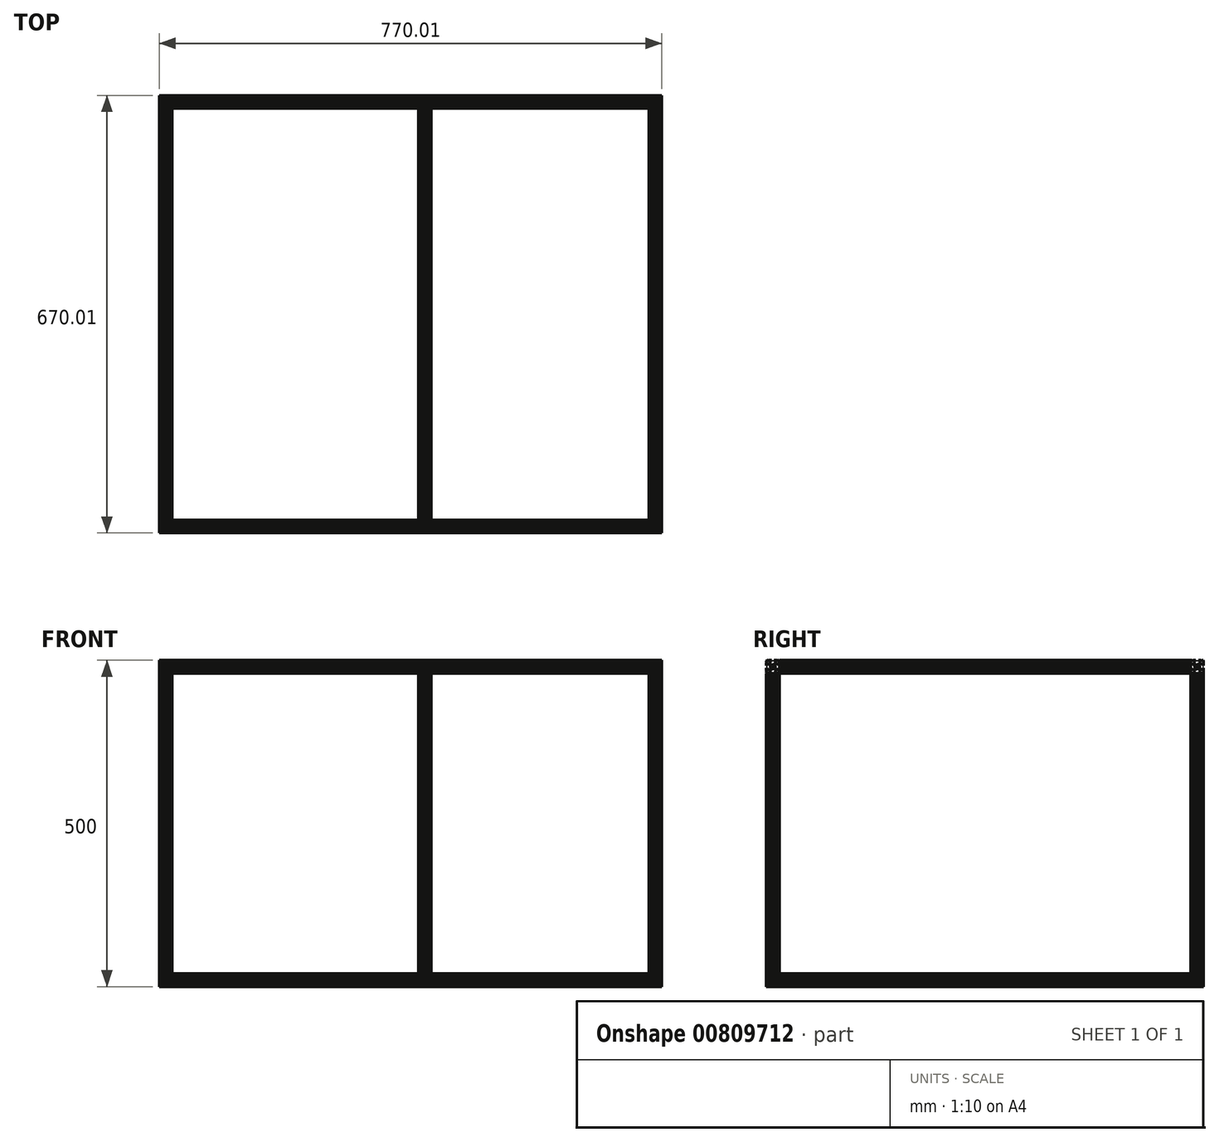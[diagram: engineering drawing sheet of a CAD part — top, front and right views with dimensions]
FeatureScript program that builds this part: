
annotation { "Feature Type Name" : "Feature", "Feature Type Description" : "" }
export const myFeature = defineFeature(function(context is Context, id is Id, definition is map)
    precondition{}
    {
        {
            var Q0;
            Q0=qCreatedBy(makeId("Top.planeOp"),FACE);
            var sketch = newSketch(context, id + "F0", { "sketchPlane" : qUnion([Q0])});
            skLineSegment(sketch, "E0", {"start": v(25.7, -17.22) * mm, "end": v(25.7, -25.12) * mm});
            skLineSegment(sketch, "E1", {"start": v(22.1, -21.63) * mm, "end": v(30.9, -21.63) * mm});
            skLineSegment(sketch, "E2", {"start": v(25.7, -40.02) * mm, "end": v(25.7, -32.12) * mm});
            skLineSegment(sketch, "E3", {"start": v(22.1, -35.63) * mm, "end": v(30.9, -35.63) * mm});
            skLineSegment(sketch, "E4", {"start": v(28.7, -30.77) * mm, "end": v(27.2, -30.77) * mm});
            skLineSegment(sketch, "E5", {"start": v(27.2, -32.77) * mm, "end": v(23.2, -32.77) * mm});
            skLineSegment(sketch, "E6", {"start": v(27.2, -32.77) * mm, "end": v(27.2, -30.77) * mm});
            skLineSegment(sketch, "E7", {"start": v(28.7, -26.48) * mm, "end": v(27.2, -26.48) * mm});
            skLineSegment(sketch, "E8", {"start": v(27.2, -24.48) * mm, "end": v(23.2, -24.48) * mm});
            skLineSegment(sketch, "E9", {"start": v(27.2, -24.48) * mm, "end": v(27.2, -26.48) * mm});
            skLineSegment(sketch, "E10", {"start": v(23.2, -24.48) * mm, "end": v(23.2, -26.12) * mm});
            skLineSegment(sketch, "E11", {"start": v(23.2, -26.12) * mm, "end": v(21.9, -26.12) * mm});
            skLineSegment(sketch, "E12", {"start": v(23.2, -32.77) * mm, "end": v(21.9, -26.12) * mm});
            skLineSegment(sketch, "E13", {"start": v(27.34, -20.94) * mm, "end": v(26.38, -19.97) * mm});
            skLineSegment(sketch, "E14", {"start": v(26.38, -19.97) * mm, "end": v(25, -19.97) * mm});
            skLineSegment(sketch, "E15", {"start": v(25, -19.97) * mm, "end": v(24.04, -20.94) * mm});
            skLineSegment(sketch, "E16", {"start": v(24.04, -20.94) * mm, "end": v(24.04, -22.3) * mm});
            skLineSegment(sketch, "E17", {"start": v(24.04, -22.3) * mm, "end": v(25, -23.28) * mm});
            skLineSegment(sketch, "E18", {"start": v(25, -23.28) * mm, "end": v(26.38, -23.28) * mm});
            skLineSegment(sketch, "E19", {"start": v(26.38, -23.28) * mm, "end": v(27.34, -22.3) * mm});
            skLineSegment(sketch, "E20", {"start": v(27.34, -22.3) * mm, "end": v(27.34, -20.94) * mm});
            skLineSegment(sketch, "E21", {"start": v(27.34, -34.94) * mm, "end": v(26.38, -33.98) * mm});
            skLineSegment(sketch, "E22", {"start": v(26.38, -33.98) * mm, "end": v(25, -33.98) * mm});
            skLineSegment(sketch, "E23", {"start": v(25, -33.98) * mm, "end": v(24.04, -34.94) * mm});
            skLineSegment(sketch, "E24", {"start": v(24.04, -34.94) * mm, "end": v(24.04, -36.3) * mm});
            skLineSegment(sketch, "E25", {"start": v(24.04, -36.3) * mm, "end": v(25, -37.28) * mm});
            skLineSegment(sketch, "E26", {"start": v(25, -37.28) * mm, "end": v(26.38, -37.28) * mm});
            skLineSegment(sketch, "E27", {"start": v(26.38, -37.28) * mm, "end": v(27.34, -36.3) * mm});
            skLineSegment(sketch, "E28", {"start": v(27.34, -36.3) * mm, "end": v(27.34, -34.94) * mm});
            skLineSegment(sketch, "E29", {"start": v(27.7, -18.62) * mm, "end": v(28.7, -19.62) * mm});
            skLineSegment(sketch, "E30", {"start": v(28.7, -37.62) * mm, "end": v(27.7, -38.62) * mm});
            skLineSegment(sketch, "E31", {"start": v(25.7, -18.83) * mm, "end": v(26.44, -18.83) * mm});
            skLineSegment(sketch, "E32", {"start": v(26.44, -18.83) * mm, "end": v(26.44, -18.62) * mm});
            skLineSegment(sketch, "E33", {"start": v(25.7, -18.83) * mm, "end": v(24.94, -18.83) * mm});
            skLineSegment(sketch, "E34", {"start": v(24.94, -18.83) * mm, "end": v(24.94, -18.62) * mm});
            skLineSegment(sketch, "E35", {"start": v(27.7, -18.62) * mm, "end": v(26.44, -18.62) * mm});
            skLineSegment(sketch, "E36", {"start": v(28.5, -21.63) * mm, "end": v(28.5, -22.38) * mm});
            skLineSegment(sketch, "E37", {"start": v(28.5, -22.38) * mm, "end": v(28.7, -22.38) * mm});
            skLineSegment(sketch, "E38", {"start": v(28.5, -21.63) * mm, "end": v(28.5, -20.88) * mm});
            skLineSegment(sketch, "E39", {"start": v(28.5, -20.88) * mm, "end": v(28.7, -20.88) * mm});
            skLineSegment(sketch, "E40", {"start": v(28.5, -35.63) * mm, "end": v(28.5, -34.88) * mm});
            skLineSegment(sketch, "E41", {"start": v(28.5, -34.88) * mm, "end": v(28.7, -34.88) * mm});
            skLineSegment(sketch, "E42", {"start": v(28.5, -35.63) * mm, "end": v(28.5, -36.38) * mm});
            skLineSegment(sketch, "E43", {"start": v(28.5, -36.38) * mm, "end": v(28.7, -36.38) * mm});
            skLineSegment(sketch, "E44", {"start": v(25.7, -38.43) * mm, "end": v(26.44, -38.43) * mm});
            skLineSegment(sketch, "E45", {"start": v(26.44, -38.43) * mm, "end": v(26.44, -38.62) * mm});
            skLineSegment(sketch, "E46", {"start": v(25.7, -38.43) * mm, "end": v(24.94, -38.43) * mm});
            skLineSegment(sketch, "E47", {"start": v(24.94, -38.43) * mm, "end": v(24.94, -38.62) * mm});
            skLineSegment(sketch, "E48", {"start": v(28.7, -19.62) * mm, "end": v(28.7, -20.88) * mm});
            skLineSegment(sketch, "E49", {"start": v(28.7, -22.38) * mm, "end": v(28.7, -26.48) * mm});
            skLineSegment(sketch, "E50", {"start": v(27.7, -38.62) * mm, "end": v(26.44, -38.62) * mm});
            skLineSegment(sketch, "E51", {"start": v(28.7, -37.62) * mm, "end": v(28.7, -36.38) * mm});
            skLineSegment(sketch, "E52", {"start": v(28.7, -34.88) * mm, "end": v(28.7, -30.77) * mm});
            skLineSegment(sketch, "E53", {"start": v(18.7, -13.92) * mm, "end": v(18.7, -42.92) * mm});
            skLineSegment(sketch, "E54", {"start": v(20.84, -18.62) * mm, "end": v(20.84, -20.12) * mm});
            skLineSegment(sketch, "E55", {"start": v(22.84, -20.12) * mm, "end": v(22.84, -24.12) * mm});
            skLineSegment(sketch, "E56", {"start": v(22.84, -20.12) * mm, "end": v(20.84, -20.12) * mm});
            skLineSegment(sketch, "E57", {"start": v(16.54, -18.62) * mm, "end": v(16.54, -20.12) * mm});
            skLineSegment(sketch, "E58", {"start": v(14.54, -20.12) * mm, "end": v(14.54, -24.12) * mm});
            skLineSegment(sketch, "E59", {"start": v(14.54, -20.12) * mm, "end": v(16.54, -20.12) * mm});
            skLineSegment(sketch, "E60", {"start": v(14.54, -24.12) * mm, "end": v(16.2, -24.12) * mm});
            skLineSegment(sketch, "E61", {"start": v(16.2, -24.12) * mm, "end": v(16.2, -25.42) * mm});
            skLineSegment(sketch, "E62", {"start": v(22.84, -24.12) * mm, "end": v(16.2, -25.42) * mm});
            skLineSegment(sketch, "E63", {"start": v(16.54, -38.62) * mm, "end": v(16.54, -37.12) * mm});
            skLineSegment(sketch, "E64", {"start": v(14.54, -37.12) * mm, "end": v(14.54, -33.12) * mm});
            skLineSegment(sketch, "E65", {"start": v(14.54, -37.12) * mm, "end": v(16.54, -37.12) * mm});
            skLineSegment(sketch, "E66", {"start": v(20.84, -38.62) * mm, "end": v(20.84, -37.12) * mm});
            skLineSegment(sketch, "E67", {"start": v(22.84, -37.12) * mm, "end": v(22.84, -33.12) * mm});
            skLineSegment(sketch, "E68", {"start": v(22.84, -37.12) * mm, "end": v(20.84, -37.12) * mm});
            skLineSegment(sketch, "E69", {"start": v(22.84, -33.12) * mm, "end": v(21.2, -33.12) * mm});
            skLineSegment(sketch, "E70", {"start": v(21.2, -33.12) * mm, "end": v(21.2, -31.83) * mm});
            skLineSegment(sketch, "E71", {"start": v(14.54, -33.12) * mm, "end": v(21.2, -31.83) * mm});
            skLineSegment(sketch, "E72", {"start": v(24.94, -18.62) * mm, "end": v(20.84, -18.62) * mm});
            skLineSegment(sketch, "E73", {"start": v(24.94, -38.62) * mm, "end": v(20.84, -38.62) * mm});
            skLineSegment(sketch, "E74", {"start": v(6.1, -28.62) * mm, "end": v(31.6, -28.62) * mm});
            skLineSegment(sketch, "E75", {"start": v(11.7, -17.22) * mm, "end": v(11.7, -25.12) * mm});
            skLineSegment(sketch, "E76", {"start": v(15.3, -21.63) * mm, "end": v(6.5, -21.63) * mm});
            skLineSegment(sketch, "E77", {"start": v(10.04, -20.94) * mm, "end": v(11, -19.97) * mm});
            skLineSegment(sketch, "E78", {"start": v(11, -19.97) * mm, "end": v(12.38, -19.97) * mm});
            skLineSegment(sketch, "E79", {"start": v(12.38, -19.97) * mm, "end": v(13.34, -20.94) * mm});
            skLineSegment(sketch, "E80", {"start": v(13.34, -20.94) * mm, "end": v(13.34, -22.3) * mm});
            skLineSegment(sketch, "E81", {"start": v(13.34, -22.3) * mm, "end": v(12.38, -23.28) * mm});
            skLineSegment(sketch, "E82", {"start": v(12.38, -23.28) * mm, "end": v(11, -23.28) * mm});
            skLineSegment(sketch, "E83", {"start": v(11, -23.28) * mm, "end": v(10.04, -22.3) * mm});
            skLineSegment(sketch, "E84", {"start": v(10.04, -22.3) * mm, "end": v(10.04, -20.94) * mm});
            skLineSegment(sketch, "E85", {"start": v(9.7, -18.62) * mm, "end": v(8.7, -19.62) * mm});
            skLineSegment(sketch, "E86", {"start": v(11.7, -18.83) * mm, "end": v(10.94, -18.83) * mm});
            skLineSegment(sketch, "E87", {"start": v(10.94, -18.83) * mm, "end": v(10.94, -18.62) * mm});
            skLineSegment(sketch, "E88", {"start": v(11.7, -18.83) * mm, "end": v(12.44, -18.83) * mm});
            skLineSegment(sketch, "E89", {"start": v(12.44, -18.83) * mm, "end": v(12.44, -18.62) * mm});
            skLineSegment(sketch, "E90", {"start": v(9.7, -18.62) * mm, "end": v(10.94, -18.62) * mm});
            skLineSegment(sketch, "E91", {"start": v(8.9, -21.63) * mm, "end": v(8.9, -22.38) * mm});
            skLineSegment(sketch, "E92", {"start": v(8.9, -22.38) * mm, "end": v(8.7, -22.38) * mm});
            skLineSegment(sketch, "E93", {"start": v(8.9, -21.63) * mm, "end": v(8.9, -20.88) * mm});
            skLineSegment(sketch, "E94", {"start": v(8.9, -20.88) * mm, "end": v(8.7, -20.88) * mm});
            skLineSegment(sketch, "E95", {"start": v(8.7, -19.62) * mm, "end": v(8.7, -20.88) * mm});
            skLineSegment(sketch, "E96", {"start": v(8.7, -22.38) * mm, "end": v(8.7, -26.48) * mm});
            skLineSegment(sketch, "E97", {"start": v(12.44, -18.62) * mm, "end": v(16.54, -18.62) * mm});
            skLineSegment(sketch, "E98", {"start": v(11.7, -40.02) * mm, "end": v(11.7, -32.12) * mm});
            skLineSegment(sketch, "E99", {"start": v(15.3, -35.63) * mm, "end": v(6.5, -35.63) * mm});
            skLineSegment(sketch, "E100", {"start": v(10.04, -34.94) * mm, "end": v(11, -33.98) * mm});
            skLineSegment(sketch, "E101", {"start": v(11, -33.98) * mm, "end": v(12.38, -33.98) * mm});
            skLineSegment(sketch, "E102", {"start": v(12.38, -33.98) * mm, "end": v(13.34, -34.94) * mm});
            skLineSegment(sketch, "E103", {"start": v(13.34, -34.94) * mm, "end": v(13.34, -36.3) * mm});
            skLineSegment(sketch, "E104", {"start": v(13.34, -36.3) * mm, "end": v(12.38, -37.28) * mm});
            skLineSegment(sketch, "E105", {"start": v(12.38, -37.28) * mm, "end": v(11, -37.28) * mm});
            skLineSegment(sketch, "E106", {"start": v(11, -37.28) * mm, "end": v(10.04, -36.3) * mm});
            skLineSegment(sketch, "E107", {"start": v(10.04, -36.3) * mm, "end": v(10.04, -34.94) * mm});
            skLineSegment(sketch, "E108", {"start": v(8.7, -37.62) * mm, "end": v(9.7, -38.62) * mm});
            skLineSegment(sketch, "E109", {"start": v(8.9, -35.63) * mm, "end": v(8.9, -34.88) * mm});
            skLineSegment(sketch, "E110", {"start": v(8.9, -34.88) * mm, "end": v(8.7, -34.88) * mm});
            skLineSegment(sketch, "E111", {"start": v(8.9, -35.63) * mm, "end": v(8.9, -36.38) * mm});
            skLineSegment(sketch, "E112", {"start": v(8.9, -36.38) * mm, "end": v(8.7, -36.38) * mm});
            skLineSegment(sketch, "E113", {"start": v(11.7, -38.43) * mm, "end": v(10.94, -38.43) * mm});
            skLineSegment(sketch, "E114", {"start": v(10.94, -38.43) * mm, "end": v(10.94, -38.62) * mm});
            skLineSegment(sketch, "E115", {"start": v(11.7, -38.43) * mm, "end": v(12.44, -38.43) * mm});
            skLineSegment(sketch, "E116", {"start": v(12.44, -38.43) * mm, "end": v(12.44, -38.62) * mm});
            skLineSegment(sketch, "E117", {"start": v(9.7, -38.62) * mm, "end": v(10.94, -38.62) * mm});
            skLineSegment(sketch, "E118", {"start": v(8.7, -37.62) * mm, "end": v(8.7, -36.38) * mm});
            skLineSegment(sketch, "E119", {"start": v(8.7, -34.88) * mm, "end": v(8.7, -30.77) * mm});
            skLineSegment(sketch, "E120", {"start": v(12.44, -38.62) * mm, "end": v(16.54, -38.62) * mm});
            skLineSegment(sketch, "E121", {"start": v(8.7, -26.48) * mm, "end": v(10.2, -26.48) * mm});
            skLineSegment(sketch, "E122", {"start": v(10.2, -24.48) * mm, "end": v(14.2, -24.48) * mm});
            skLineSegment(sketch, "E123", {"start": v(10.2, -24.48) * mm, "end": v(10.2, -26.48) * mm});
            skLineSegment(sketch, "E124", {"start": v(8.7, -30.77) * mm, "end": v(10.2, -30.77) * mm});
            skLineSegment(sketch, "E125", {"start": v(10.2, -32.77) * mm, "end": v(14.2, -32.77) * mm});
            skLineSegment(sketch, "E126", {"start": v(10.2, -32.77) * mm, "end": v(10.2, -30.77) * mm});
            skLineSegment(sketch, "E127", {"start": v(14.2, -32.77) * mm, "end": v(14.2, -31.12) * mm});
            skLineSegment(sketch, "E128", {"start": v(14.2, -31.12) * mm, "end": v(15.5, -31.12) * mm});
            skLineSegment(sketch, "E129", {"start": v(14.2, -24.48) * mm, "end": v(15.5, -31.12) * mm});
            skCircle(sketch, "E130", {"center": v(18.7, -28.62) * mm, "radius": 1.6 * mm});
            skSolve(sketch);
        }
        {
            var Q0;
            {var subQ21=sQuery(id+"F0.wireOp",EDGE,"E10");Q0=makeQuery(id+"F0.imprint","IMPRINT",FACE,{"disambiguationData":[TD([[makeQuery(id+"F0.imprint","IMPRINT",EDGE,{"derivedFrom":subQ21}),-1.0]])]});}
            var Q1;
            {var subQ9=sQuery(id+"F0.wireOp",EDGE,"E23");Q1=makeQuery(id+"F0.imprint","IMPRINT",FACE,{"disambiguationData":[TD([[makeQuery(id+"F0.imprint","IMPRINT",EDGE,{"derivedFrom":subQ9}),-1.0]])]});}
            var Q2;
            {var subQ21=sQuery(id+"F0.wireOp",EDGE,"E60");Q2=makeQuery(id+"F0.imprint","IMPRINT",FACE,{"disambiguationData":[TD([[makeQuery(id+"F0.imprint","IMPRINT",EDGE,{"derivedFrom":subQ21}),-1.0]])]});}
            var Q3;
            {var subQ1=sQuery(id+"F0.wireOp",EDGE,"E102");Q3=makeQuery(id+"F0.imprint","IMPRINT",FACE,{"disambiguationData":[TD([[makeQuery(id+"F0.imprint","IMPRINT",EDGE,{"derivedFrom":subQ1}),1.0]])]});}
            var Q4;
            {var subQ0=sQuery(id+"F0.wireOp",EDGE,"E74");var subQ1=sQuery(id+"F0.wireOp",EDGE,"E53");var subQ2=makeQuery(id+"F0.imprint","INTERSECT",VERTEX,{"derivedFrom":[subQ1,subQ0]});Q4=makeQuery(id+"F0.imprint","IMPRINT",FACE,{"disambiguationData":[TD([[makeQuery(id+"F0.imprint","IMPRINT",EDGE,{"disambiguationData":[TD([[subQ2,-1.0]])],"derivedFrom":subQ1}),-1.0]])]});}
            var Q5;
            {var subQ0=sQuery(id+"F0.wireOp",EDGE,"E74");var subQ1=sQuery(id+"F0.wireOp",EDGE,"E53");var subQ2=makeQuery(id+"F0.imprint","INTERSECT",VERTEX,{"derivedFrom":[subQ1,subQ0]});Q5=makeQuery(id+"F0.imprint","IMPRINT",FACE,{"disambiguationData":[TD([[makeQuery(id+"F0.imprint","IMPRINT",EDGE,{"disambiguationData":[TD([[subQ2,-1.0]])],"derivedFrom":subQ1}),1.0]])]});}
            var Q6;
            {var subQ0=sQuery(id+"F0.wireOp",EDGE,"E130");var subQ1=sQuery(id+"F0.wireOp",EDGE,"E53");var subQ2=makeQuery(id+"F0.imprint","INTERSECT",VERTEX,{"disambiguationData":[OD(0.0)],"derivedFrom":[subQ1,subQ0]});Q6=makeQuery(id+"F0.imprint","IMPRINT",FACE,{"disambiguationData":[TD([[makeQuery(id+"F0.imprint","IMPRINT",EDGE,{"disambiguationData":[TD([[subQ2,-1.0]])],"derivedFrom":subQ1}),1.0]])]});}
            var Q7;
            {var subQ0=sQuery(id+"F0.wireOp",EDGE,"E130");var subQ1=sQuery(id+"F0.wireOp",EDGE,"E53");var subQ2=makeQuery(id+"F0.imprint","INTERSECT",VERTEX,{"disambiguationData":[OD(0.0)],"derivedFrom":[subQ1,subQ0]});Q7=makeQuery(id+"F0.imprint","IMPRINT",FACE,{"disambiguationData":[TD([[makeQuery(id+"F0.imprint","IMPRINT",EDGE,{"disambiguationData":[TD([[subQ2,-1.0]])],"derivedFrom":subQ1}),-1.0]])]});}
            var Q8;
            {var subQ0=sQuery(id+"F0.wireOp",EDGE,"E102");Q8=makeQuery(id+"F0.imprint","IMPRINT",FACE,{"disambiguationData":[TD([[makeQuery(id+"F0.imprint","IMPRINT",EDGE,{"derivedFrom":subQ0}),-1.0]])]});}
            var Q9;
            {var subQ0=sQuery(id+"F0.wireOp",EDGE,"E104");Q9=makeQuery(id+"F0.imprint","IMPRINT",FACE,{"disambiguationData":[TD([[makeQuery(id+"F0.imprint","IMPRINT",EDGE,{"derivedFrom":subQ0}),-1.0]])]});}
            var Q10;
            {var subQ1=sQuery(id+"F0.wireOp",EDGE,"E100");Q10=makeQuery(id+"F0.imprint","IMPRINT",FACE,{"disambiguationData":[TD([[makeQuery(id+"F0.imprint","IMPRINT",EDGE,{"derivedFrom":subQ1}),-1.0]])]});}
            var Q11;
            {var subQ0=sQuery(id+"F0.wireOp",EDGE,"E106");Q11=makeQuery(id+"F0.imprint","IMPRINT",FACE,{"disambiguationData":[TD([[makeQuery(id+"F0.imprint","IMPRINT",EDGE,{"derivedFrom":subQ0}),-1.0]])]});}
            var Q12;
            Q12=makeQuery(id+"F0.imprint","IMPRINT",FACE,{"disambiguationData":[TD([[makeQuery(id+"F0.imprint","IMPRINT",EDGE,{"derivedFrom":sQuery(id+"F0.wireOp",EDGE,"E57")}),-1.0]])]});
            var Q13;
            Q13=makeQuery(id+"F0.imprint","IMPRINT",FACE,{"disambiguationData":[TD([[makeQuery(id+"F0.imprint","IMPRINT",EDGE,{"derivedFrom":sQuery(id+"F0.wireOp",EDGE,"E63")}),1.0]])]});
            var Q14;
            {var subQ0=sQuery(id+"F0.wireOp",EDGE,"E79");Q14=makeQuery(id+"F0.imprint","IMPRINT",FACE,{"disambiguationData":[TD([[makeQuery(id+"F0.imprint","IMPRINT",EDGE,{"derivedFrom":subQ0}),-1.0]])]});}
            var Q15;
            Q15=makeQuery(id+"F0.imprint","IMPRINT",FACE,{"disambiguationData":[TD([[makeQuery(id+"F0.imprint","IMPRINT",EDGE,{"derivedFrom":sQuery(id+"F0.wireOp",EDGE,"E4")}),1.0]])]});
            var Q16;
            {var subQ3=sQuery(id+"F0.wireOp",EDGE,"E15");Q16=makeQuery(id+"F0.imprint","IMPRINT",FACE,{"disambiguationData":[TD([[makeQuery(id+"F0.imprint","IMPRINT",EDGE,{"derivedFrom":subQ3}),-1.0]])]});}
            var Q17;
            {var subQ0=sQuery(id+"F0.wireOp",EDGE,"E15");Q17=makeQuery(id+"F0.imprint","IMPRINT",FACE,{"disambiguationData":[TD([[makeQuery(id+"F0.imprint","IMPRINT",EDGE,{"derivedFrom":subQ0}),1.0]])]});}
            var Q18;
            Q18=makeQuery(id+"F0.imprint","IMPRINT",FACE,{"disambiguationData":[TD([[makeQuery(id+"F0.imprint","IMPRINT",EDGE,{"derivedFrom":sQuery(id+"F0.wireOp",EDGE,"E7")}),-1.0]])]});
            var Q19;
            {var subQ5=sQuery(id+"F0.wireOp",EDGE,"E25");Q19=makeQuery(id+"F0.imprint","IMPRINT",FACE,{"disambiguationData":[TD([[makeQuery(id+"F0.imprint","IMPRINT",EDGE,{"derivedFrom":subQ5}),-1.0]])]});}
            var Q20;
            {var subQ0=sQuery(id+"F0.wireOp",EDGE,"E25");Q20=makeQuery(id+"F0.imprint","IMPRINT",FACE,{"disambiguationData":[TD([[makeQuery(id+"F0.imprint","IMPRINT",EDGE,{"derivedFrom":subQ0}),1.0]])]});}
            var Q21;
            {var subQ0=sQuery(id+"F0.wireOp",EDGE,"E27");Q21=makeQuery(id+"F0.imprint","IMPRINT",FACE,{"disambiguationData":[TD([[makeQuery(id+"F0.imprint","IMPRINT",EDGE,{"derivedFrom":subQ0}),1.0]])]});}
            var Q22;
            {var subQ1=sQuery(id+"F0.wireOp",EDGE,"E21");Q22=makeQuery(id+"F0.imprint","IMPRINT",FACE,{"disambiguationData":[TD([[makeQuery(id+"F0.imprint","IMPRINT",EDGE,{"derivedFrom":subQ1}),1.0]])]});}
            var Q23;
            {var subQ0=sQuery(id+"F0.wireOp",EDGE,"E83");Q23=makeQuery(id+"F0.imprint","IMPRINT",FACE,{"disambiguationData":[TD([[makeQuery(id+"F0.imprint","IMPRINT",EDGE,{"derivedFrom":subQ0}),-1.0]])]});}
            var Q24;
            {var subQ8=sQuery(id+"F0.wireOp",EDGE,"E100");Q24=makeQuery(id+"F0.imprint","IMPRINT",FACE,{"disambiguationData":[TD([[makeQuery(id+"F0.imprint","IMPRINT",EDGE,{"derivedFrom":subQ8}),1.0]])]});}
            var Q25;
            {var subQ8=sQuery(id+"F0.wireOp",EDGE,"E83");Q25=makeQuery(id+"F0.imprint","IMPRINT",FACE,{"disambiguationData":[TD([[makeQuery(id+"F0.imprint","IMPRINT",EDGE,{"derivedFrom":subQ8}),1.0]])]});}
            var Q26;
            {var subQ6=sQuery(id+"F0.wireOp",EDGE,"E106");Q26=makeQuery(id+"F0.imprint","IMPRINT",FACE,{"disambiguationData":[TD([[makeQuery(id+"F0.imprint","IMPRINT",EDGE,{"derivedFrom":subQ6}),1.0]])]});}
            var Q27;
            {var subQ8=sQuery(id+"F0.wireOp",EDGE,"E77");Q27=makeQuery(id+"F0.imprint","IMPRINT",FACE,{"disambiguationData":[TD([[makeQuery(id+"F0.imprint","IMPRINT",EDGE,{"derivedFrom":subQ8}),1.0]])]});}
            var Q28;
            {var subQ1=sQuery(id+"F0.wireOp",EDGE,"E77");Q28=makeQuery(id+"F0.imprint","IMPRINT",FACE,{"disambiguationData":[TD([[makeQuery(id+"F0.imprint","IMPRINT",EDGE,{"derivedFrom":subQ1}),-1.0]])]});}
            var Q29;
            {var subQ2=sQuery(id+"F0.wireOp",EDGE,"E13");Q29=makeQuery(id+"F0.imprint","IMPRINT",FACE,{"disambiguationData":[TD([[makeQuery(id+"F0.imprint","IMPRINT",EDGE,{"derivedFrom":subQ2}),-1.0]])]});}
            var Q30;
            {var subQ1=sQuery(id+"F0.wireOp",EDGE,"E13");Q30=makeQuery(id+"F0.imprint","IMPRINT",FACE,{"disambiguationData":[TD([[makeQuery(id+"F0.imprint","IMPRINT",EDGE,{"derivedFrom":subQ1}),1.0]])]});}
            var Q31;
            {var subQ0=sQuery(id+"F0.wireOp",EDGE,"E17");Q31=makeQuery(id+"F0.imprint","IMPRINT",FACE,{"disambiguationData":[TD([[makeQuery(id+"F0.imprint","IMPRINT",EDGE,{"derivedFrom":subQ0}),1.0]])]});}
            var Q32;
            {var subQ3=sQuery(id+"F0.wireOp",EDGE,"E27");Q32=makeQuery(id+"F0.imprint","IMPRINT",FACE,{"disambiguationData":[TD([[makeQuery(id+"F0.imprint","IMPRINT",EDGE,{"derivedFrom":subQ3}),-1.0]])]});}
            var Q33;
            {var subQ0=sQuery(id+"F0.wireOp",EDGE,"E23");Q33=makeQuery(id+"F0.imprint","IMPRINT",FACE,{"disambiguationData":[TD([[makeQuery(id+"F0.imprint","IMPRINT",EDGE,{"derivedFrom":subQ0}),1.0]])]});}
            var Q34;
            {var subQ0=sQuery(id+"F0.wireOp",EDGE,"E81");Q34=makeQuery(id+"F0.imprint","IMPRINT",FACE,{"disambiguationData":[TD([[makeQuery(id+"F0.imprint","IMPRINT",EDGE,{"derivedFrom":subQ0}),-1.0]])]});}
            var Q35;
            {var subQ0=sQuery(id+"F0.wireOp",EDGE,"E19");Q35=makeQuery(id+"F0.imprint","IMPRINT",FACE,{"disambiguationData":[TD([[makeQuery(id+"F0.imprint","IMPRINT",EDGE,{"derivedFrom":subQ0}),1.0]])]});}
            extrude(context, id + "F1", {"entities" : qUnion([Q0, Q1, Q2, Q3, Q4, Q5, Q6, Q7, Q8, Q9, Q10, Q11, Q12, Q13, Q14, Q15, Q16, Q17, Q18, Q19, Q20, Q21, Q22, Q23, Q24, Q25, Q26, Q27, Q28, Q29, Q30, Q31, Q32, Q33, Q34, Q35]), "depth" : 480 * mm, "offsetDistance" : 25 * mm});
        }
        {
            var Q0;
            Q0=makeQuery(id+"F1.opExtrude","SWEPT_BODY",BODY,{"disambiguationData":[OSD([sQuery(id+"F0.wireOp",EDGE,"E4"),sQuery(id+"F0.wireOp",EDGE,"E5"),sQuery(id+"F0.wireOp",EDGE,"E6"),sQuery(id+"F0.wireOp",EDGE,"E7"),sQuery(id+"F0.wireOp",EDGE,"E8"),sQuery(id+"F0.wireOp",EDGE,"E9"),sQuery(id+"F0.wireOp",EDGE,"E10"),sQuery(id+"F0.wireOp",EDGE,"E11"),sQuery(id+"F0.wireOp",EDGE,"E12"),sQuery(id+"F0.wireOp",EDGE,"E29"),sQuery(id+"F0.wireOp",EDGE,"E30"),sQuery(id+"F0.wireOp",EDGE,"E31"),sQuery(id+"F0.wireOp",EDGE,"E32"),sQuery(id+"F0.wireOp",EDGE,"E33"),sQuery(id+"F0.wireOp",EDGE,"E34"),sQuery(id+"F0.wireOp",EDGE,"E35"),sQuery(id+"F0.wireOp",EDGE,"E36"),sQuery(id+"F0.wireOp",EDGE,"E37"),sQuery(id+"F0.wireOp",EDGE,"E38"),sQuery(id+"F0.wireOp",EDGE,"E39"),sQuery(id+"F0.wireOp",EDGE,"E40"),sQuery(id+"F0.wireOp",EDGE,"E41"),sQuery(id+"F0.wireOp",EDGE,"E42"),sQuery(id+"F0.wireOp",EDGE,"E43"),sQuery(id+"F0.wireOp",EDGE,"E44"),sQuery(id+"F0.wireOp",EDGE,"E45"),sQuery(id+"F0.wireOp",EDGE,"E46"),sQuery(id+"F0.wireOp",EDGE,"E47"),sQuery(id+"F0.wireOp",EDGE,"E48"),sQuery(id+"F0.wireOp",EDGE,"E49"),sQuery(id+"F0.wireOp",EDGE,"E50"),sQuery(id+"F0.wireOp",EDGE,"E51"),sQuery(id+"F0.wireOp",EDGE,"E52"),sQuery(id+"F0.wireOp",EDGE,"E54"),sQuery(id+"F0.wireOp",EDGE,"E55"),sQuery(id+"F0.wireOp",EDGE,"E56"),sQuery(id+"F0.wireOp",EDGE,"E57"),sQuery(id+"F0.wireOp",EDGE,"E58"),sQuery(id+"F0.wireOp",EDGE,"E59"),sQuery(id+"F0.wireOp",EDGE,"E60"),sQuery(id+"F0.wireOp",EDGE,"E61"),sQuery(id+"F0.wireOp",EDGE,"E62"),sQuery(id+"F0.wireOp",EDGE,"E63"),sQuery(id+"F0.wireOp",EDGE,"E64"),sQuery(id+"F0.wireOp",EDGE,"E65"),sQuery(id+"F0.wireOp",EDGE,"E66"),sQuery(id+"F0.wireOp",EDGE,"E67"),sQuery(id+"F0.wireOp",EDGE,"E68"),sQuery(id+"F0.wireOp",EDGE,"E69"),sQuery(id+"F0.wireOp",EDGE,"E70"),sQuery(id+"F0.wireOp",EDGE,"E71"),sQuery(id+"F0.wireOp",EDGE,"E72"),sQuery(id+"F0.wireOp",EDGE,"E73"),sQuery(id+"F0.wireOp",EDGE,"E85"),sQuery(id+"F0.wireOp",EDGE,"E86"),sQuery(id+"F0.wireOp",EDGE,"E87"),sQuery(id+"F0.wireOp",EDGE,"E88"),sQuery(id+"F0.wireOp",EDGE,"E89"),sQuery(id+"F0.wireOp",EDGE,"E90"),sQuery(id+"F0.wireOp",EDGE,"E91"),sQuery(id+"F0.wireOp",EDGE,"E92"),sQuery(id+"F0.wireOp",EDGE,"E93"),sQuery(id+"F0.wireOp",EDGE,"E94"),sQuery(id+"F0.wireOp",EDGE,"E95"),sQuery(id+"F0.wireOp",EDGE,"E96"),sQuery(id+"F0.wireOp",EDGE,"E97"),sQuery(id+"F0.wireOp",EDGE,"E108"),sQuery(id+"F0.wireOp",EDGE,"E109"),sQuery(id+"F0.wireOp",EDGE,"E110"),sQuery(id+"F0.wireOp",EDGE,"E111"),sQuery(id+"F0.wireOp",EDGE,"E112"),sQuery(id+"F0.wireOp",EDGE,"E113"),sQuery(id+"F0.wireOp",EDGE,"E114"),sQuery(id+"F0.wireOp",EDGE,"E115"),sQuery(id+"F0.wireOp",EDGE,"E116"),sQuery(id+"F0.wireOp",EDGE,"E117"),sQuery(id+"F0.wireOp",EDGE,"E118"),sQuery(id+"F0.wireOp",EDGE,"E119"),sQuery(id+"F0.wireOp",EDGE,"E120"),sQuery(id+"F0.wireOp",EDGE,"E121"),sQuery(id+"F0.wireOp",EDGE,"E122"),sQuery(id+"F0.wireOp",EDGE,"E123"),sQuery(id+"F0.wireOp",EDGE,"E124"),sQuery(id+"F0.wireOp",EDGE,"E125"),sQuery(id+"F0.wireOp",EDGE,"E126"),sQuery(id+"F0.wireOp",EDGE,"E127"),sQuery(id+"F0.wireOp",EDGE,"E128"),sQuery(id+"F0.wireOp",EDGE,"E129")])]});
            transform(context, id + "F2", {"entities" : qUnion([Q0]), "transformType" : TransformType.TRANSLATION_3D, "dx" : 0 * mm, "dy" : 650 * mm, "dz" : 0 * mm, "makeCopy" : true});
        }
        {
            var Q0;
            Q0=makeQuery(id+"F1.opExtrude","SWEPT_BODY",BODY,{"disambiguationData":[OSD([sQuery(id+"F0.wireOp",EDGE,"E4"),sQuery(id+"F0.wireOp",EDGE,"E5"),sQuery(id+"F0.wireOp",EDGE,"E6"),sQuery(id+"F0.wireOp",EDGE,"E7"),sQuery(id+"F0.wireOp",EDGE,"E8"),sQuery(id+"F0.wireOp",EDGE,"E9"),sQuery(id+"F0.wireOp",EDGE,"E10"),sQuery(id+"F0.wireOp",EDGE,"E11"),sQuery(id+"F0.wireOp",EDGE,"E12"),sQuery(id+"F0.wireOp",EDGE,"E29"),sQuery(id+"F0.wireOp",EDGE,"E30"),sQuery(id+"F0.wireOp",EDGE,"E31"),sQuery(id+"F0.wireOp",EDGE,"E32"),sQuery(id+"F0.wireOp",EDGE,"E33"),sQuery(id+"F0.wireOp",EDGE,"E34"),sQuery(id+"F0.wireOp",EDGE,"E35"),sQuery(id+"F0.wireOp",EDGE,"E36"),sQuery(id+"F0.wireOp",EDGE,"E37"),sQuery(id+"F0.wireOp",EDGE,"E38"),sQuery(id+"F0.wireOp",EDGE,"E39"),sQuery(id+"F0.wireOp",EDGE,"E40"),sQuery(id+"F0.wireOp",EDGE,"E41"),sQuery(id+"F0.wireOp",EDGE,"E42"),sQuery(id+"F0.wireOp",EDGE,"E43"),sQuery(id+"F0.wireOp",EDGE,"E44"),sQuery(id+"F0.wireOp",EDGE,"E45"),sQuery(id+"F0.wireOp",EDGE,"E46"),sQuery(id+"F0.wireOp",EDGE,"E47"),sQuery(id+"F0.wireOp",EDGE,"E48"),sQuery(id+"F0.wireOp",EDGE,"E49"),sQuery(id+"F0.wireOp",EDGE,"E50"),sQuery(id+"F0.wireOp",EDGE,"E51"),sQuery(id+"F0.wireOp",EDGE,"E52"),sQuery(id+"F0.wireOp",EDGE,"E54"),sQuery(id+"F0.wireOp",EDGE,"E55"),sQuery(id+"F0.wireOp",EDGE,"E56"),sQuery(id+"F0.wireOp",EDGE,"E57"),sQuery(id+"F0.wireOp",EDGE,"E58"),sQuery(id+"F0.wireOp",EDGE,"E59"),sQuery(id+"F0.wireOp",EDGE,"E60"),sQuery(id+"F0.wireOp",EDGE,"E61"),sQuery(id+"F0.wireOp",EDGE,"E62"),sQuery(id+"F0.wireOp",EDGE,"E63"),sQuery(id+"F0.wireOp",EDGE,"E64"),sQuery(id+"F0.wireOp",EDGE,"E65"),sQuery(id+"F0.wireOp",EDGE,"E66"),sQuery(id+"F0.wireOp",EDGE,"E67"),sQuery(id+"F0.wireOp",EDGE,"E68"),sQuery(id+"F0.wireOp",EDGE,"E69"),sQuery(id+"F0.wireOp",EDGE,"E70"),sQuery(id+"F0.wireOp",EDGE,"E71"),sQuery(id+"F0.wireOp",EDGE,"E72"),sQuery(id+"F0.wireOp",EDGE,"E73"),sQuery(id+"F0.wireOp",EDGE,"E85"),sQuery(id+"F0.wireOp",EDGE,"E86"),sQuery(id+"F0.wireOp",EDGE,"E87"),sQuery(id+"F0.wireOp",EDGE,"E88"),sQuery(id+"F0.wireOp",EDGE,"E89"),sQuery(id+"F0.wireOp",EDGE,"E90"),sQuery(id+"F0.wireOp",EDGE,"E91"),sQuery(id+"F0.wireOp",EDGE,"E92"),sQuery(id+"F0.wireOp",EDGE,"E93"),sQuery(id+"F0.wireOp",EDGE,"E94"),sQuery(id+"F0.wireOp",EDGE,"E95"),sQuery(id+"F0.wireOp",EDGE,"E96"),sQuery(id+"F0.wireOp",EDGE,"E97"),sQuery(id+"F0.wireOp",EDGE,"E108"),sQuery(id+"F0.wireOp",EDGE,"E109"),sQuery(id+"F0.wireOp",EDGE,"E110"),sQuery(id+"F0.wireOp",EDGE,"E111"),sQuery(id+"F0.wireOp",EDGE,"E112"),sQuery(id+"F0.wireOp",EDGE,"E113"),sQuery(id+"F0.wireOp",EDGE,"E114"),sQuery(id+"F0.wireOp",EDGE,"E115"),sQuery(id+"F0.wireOp",EDGE,"E116"),sQuery(id+"F0.wireOp",EDGE,"E117"),sQuery(id+"F0.wireOp",EDGE,"E118"),sQuery(id+"F0.wireOp",EDGE,"E119"),sQuery(id+"F0.wireOp",EDGE,"E120"),sQuery(id+"F0.wireOp",EDGE,"E121"),sQuery(id+"F0.wireOp",EDGE,"E122"),sQuery(id+"F0.wireOp",EDGE,"E123"),sQuery(id+"F0.wireOp",EDGE,"E124"),sQuery(id+"F0.wireOp",EDGE,"E125"),sQuery(id+"F0.wireOp",EDGE,"E126"),sQuery(id+"F0.wireOp",EDGE,"E127"),sQuery(id+"F0.wireOp",EDGE,"E128"),sQuery(id+"F0.wireOp",EDGE,"E129")])]});
            var Q1;
            Q1=makeQuery(id+"F2.opPattern","COPY",BODY,{"derivedFrom":makeQuery(id+"F1.opExtrude","SWEPT_BODY",BODY,{"disambiguationData":[OSD([sQuery(id+"F0.wireOp",EDGE,"E4"),sQuery(id+"F0.wireOp",EDGE,"E5"),sQuery(id+"F0.wireOp",EDGE,"E6"),sQuery(id+"F0.wireOp",EDGE,"E7"),sQuery(id+"F0.wireOp",EDGE,"E8"),sQuery(id+"F0.wireOp",EDGE,"E9"),sQuery(id+"F0.wireOp",EDGE,"E10"),sQuery(id+"F0.wireOp",EDGE,"E11"),sQuery(id+"F0.wireOp",EDGE,"E12"),sQuery(id+"F0.wireOp",EDGE,"E29"),sQuery(id+"F0.wireOp",EDGE,"E30"),sQuery(id+"F0.wireOp",EDGE,"E31"),sQuery(id+"F0.wireOp",EDGE,"E32"),sQuery(id+"F0.wireOp",EDGE,"E33"),sQuery(id+"F0.wireOp",EDGE,"E34"),sQuery(id+"F0.wireOp",EDGE,"E35"),sQuery(id+"F0.wireOp",EDGE,"E36"),sQuery(id+"F0.wireOp",EDGE,"E37"),sQuery(id+"F0.wireOp",EDGE,"E38"),sQuery(id+"F0.wireOp",EDGE,"E39"),sQuery(id+"F0.wireOp",EDGE,"E40"),sQuery(id+"F0.wireOp",EDGE,"E41"),sQuery(id+"F0.wireOp",EDGE,"E42"),sQuery(id+"F0.wireOp",EDGE,"E43"),sQuery(id+"F0.wireOp",EDGE,"E44"),sQuery(id+"F0.wireOp",EDGE,"E45"),sQuery(id+"F0.wireOp",EDGE,"E46"),sQuery(id+"F0.wireOp",EDGE,"E47"),sQuery(id+"F0.wireOp",EDGE,"E48"),sQuery(id+"F0.wireOp",EDGE,"E49"),sQuery(id+"F0.wireOp",EDGE,"E50"),sQuery(id+"F0.wireOp",EDGE,"E51"),sQuery(id+"F0.wireOp",EDGE,"E52"),sQuery(id+"F0.wireOp",EDGE,"E54"),sQuery(id+"F0.wireOp",EDGE,"E55"),sQuery(id+"F0.wireOp",EDGE,"E56"),sQuery(id+"F0.wireOp",EDGE,"E57"),sQuery(id+"F0.wireOp",EDGE,"E58"),sQuery(id+"F0.wireOp",EDGE,"E59"),sQuery(id+"F0.wireOp",EDGE,"E60"),sQuery(id+"F0.wireOp",EDGE,"E61"),sQuery(id+"F0.wireOp",EDGE,"E62"),sQuery(id+"F0.wireOp",EDGE,"E63"),sQuery(id+"F0.wireOp",EDGE,"E64"),sQuery(id+"F0.wireOp",EDGE,"E65"),sQuery(id+"F0.wireOp",EDGE,"E66"),sQuery(id+"F0.wireOp",EDGE,"E67"),sQuery(id+"F0.wireOp",EDGE,"E68"),sQuery(id+"F0.wireOp",EDGE,"E69"),sQuery(id+"F0.wireOp",EDGE,"E70"),sQuery(id+"F0.wireOp",EDGE,"E71"),sQuery(id+"F0.wireOp",EDGE,"E72"),sQuery(id+"F0.wireOp",EDGE,"E73"),sQuery(id+"F0.wireOp",EDGE,"E85"),sQuery(id+"F0.wireOp",EDGE,"E86"),sQuery(id+"F0.wireOp",EDGE,"E87"),sQuery(id+"F0.wireOp",EDGE,"E88"),sQuery(id+"F0.wireOp",EDGE,"E89"),sQuery(id+"F0.wireOp",EDGE,"E90"),sQuery(id+"F0.wireOp",EDGE,"E91"),sQuery(id+"F0.wireOp",EDGE,"E92"),sQuery(id+"F0.wireOp",EDGE,"E93"),sQuery(id+"F0.wireOp",EDGE,"E94"),sQuery(id+"F0.wireOp",EDGE,"E95"),sQuery(id+"F0.wireOp",EDGE,"E96"),sQuery(id+"F0.wireOp",EDGE,"E97"),sQuery(id+"F0.wireOp",EDGE,"E108"),sQuery(id+"F0.wireOp",EDGE,"E109"),sQuery(id+"F0.wireOp",EDGE,"E110"),sQuery(id+"F0.wireOp",EDGE,"E111"),sQuery(id+"F0.wireOp",EDGE,"E112"),sQuery(id+"F0.wireOp",EDGE,"E113"),sQuery(id+"F0.wireOp",EDGE,"E114"),sQuery(id+"F0.wireOp",EDGE,"E115"),sQuery(id+"F0.wireOp",EDGE,"E116"),sQuery(id+"F0.wireOp",EDGE,"E117"),sQuery(id+"F0.wireOp",EDGE,"E118"),sQuery(id+"F0.wireOp",EDGE,"E119"),sQuery(id+"F0.wireOp",EDGE,"E120"),sQuery(id+"F0.wireOp",EDGE,"E121"),sQuery(id+"F0.wireOp",EDGE,"E122"),sQuery(id+"F0.wireOp",EDGE,"E123"),sQuery(id+"F0.wireOp",EDGE,"E124"),sQuery(id+"F0.wireOp",EDGE,"E125"),sQuery(id+"F0.wireOp",EDGE,"E126"),sQuery(id+"F0.wireOp",EDGE,"E127"),sQuery(id+"F0.wireOp",EDGE,"E128"),sQuery(id+"F0.wireOp",EDGE,"E129")])]}),"instanceName":"1"});
            transform(context, id + "F3", {"entities" : qUnion([Q0, Q1]), "transformType" : TransformType.TRANSLATION_3D, "dx" : -750 * mm, "dy" : 0 * mm, "dz" : 0 * mm, "makeCopy" : true});
        }
        {
            var Q0;
            Q0=qCreatedBy(makeId("Right.planeOp"),FACE);
            cPlane(context, id + "F4", {"entities" : qUnion([Q0]), "cplaneType" : CPlaneType.OFFSET, "offset" : 8.7 * mm, "width" : 150 * mm, "height" : 150 * mm});
        }
        {
            var Q0;
            Q0=qCreatedBy(id+"F4.planeOp",FACE);
            var sketch = newSketch(context, id + "F5", { "sketchPlane" : qUnion([Q0])});
            skLineSegment(sketch, "E131", {"start": v(25.7, -17.22) * mm, "end": v(25.7, -25.12) * mm});
            skLineSegment(sketch, "E132", {"start": v(22.1, -21.63) * mm, "end": v(30.9, -21.63) * mm});
            skLineSegment(sketch, "E133", {"start": v(25.7, -40.02) * mm, "end": v(25.7, -32.12) * mm});
            skLineSegment(sketch, "E134", {"start": v(22.1, -35.63) * mm, "end": v(30.9, -35.63) * mm});
            skLineSegment(sketch, "E135", {"start": v(28.7, -30.77) * mm, "end": v(27.2, -30.77) * mm});
            skLineSegment(sketch, "E136", {"start": v(27.2, -32.77) * mm, "end": v(23.2, -32.77) * mm});
            skLineSegment(sketch, "E137", {"start": v(27.2, -32.77) * mm, "end": v(27.2, -30.77) * mm});
            skLineSegment(sketch, "E138", {"start": v(28.7, -26.48) * mm, "end": v(27.2, -26.48) * mm});
            skLineSegment(sketch, "E139", {"start": v(27.2, -24.48) * mm, "end": v(23.2, -24.48) * mm});
            skLineSegment(sketch, "E140", {"start": v(27.2, -24.48) * mm, "end": v(27.2, -26.48) * mm});
            skLineSegment(sketch, "E141", {"start": v(23.2, -24.48) * mm, "end": v(23.2, -26.12) * mm});
            skLineSegment(sketch, "E142", {"start": v(23.2, -26.12) * mm, "end": v(21.9, -26.12) * mm});
            skLineSegment(sketch, "E143", {"start": v(23.2, -32.77) * mm, "end": v(21.9, -26.12) * mm});
            skLineSegment(sketch, "E144", {"start": v(27.34, -20.94) * mm, "end": v(26.38, -19.97) * mm});
            skLineSegment(sketch, "E145", {"start": v(26.38, -19.97) * mm, "end": v(25, -19.97) * mm});
            skLineSegment(sketch, "E146", {"start": v(25, -19.97) * mm, "end": v(24.04, -20.94) * mm});
            skLineSegment(sketch, "E147", {"start": v(24.04, -20.94) * mm, "end": v(24.04, -22.3) * mm});
            skLineSegment(sketch, "E148", {"start": v(24.04, -22.3) * mm, "end": v(25, -23.28) * mm});
            skLineSegment(sketch, "E149", {"start": v(25, -23.28) * mm, "end": v(26.38, -23.28) * mm});
            skLineSegment(sketch, "E150", {"start": v(26.38, -23.28) * mm, "end": v(27.34, -22.3) * mm});
            skLineSegment(sketch, "E151", {"start": v(27.34, -22.3) * mm, "end": v(27.34, -20.94) * mm});
            skLineSegment(sketch, "E152", {"start": v(27.34, -34.94) * mm, "end": v(26.38, -33.98) * mm});
            skLineSegment(sketch, "E153", {"start": v(26.38, -33.98) * mm, "end": v(25, -33.98) * mm});
            skLineSegment(sketch, "E154", {"start": v(25, -33.98) * mm, "end": v(24.04, -34.94) * mm});
            skLineSegment(sketch, "E155", {"start": v(24.04, -34.94) * mm, "end": v(24.04, -36.3) * mm});
            skLineSegment(sketch, "E156", {"start": v(24.04, -36.3) * mm, "end": v(25, -37.28) * mm});
            skLineSegment(sketch, "E157", {"start": v(25, -37.28) * mm, "end": v(26.38, -37.28) * mm});
            skLineSegment(sketch, "E158", {"start": v(26.38, -37.28) * mm, "end": v(27.34, -36.3) * mm});
            skLineSegment(sketch, "E159", {"start": v(27.34, -36.3) * mm, "end": v(27.34, -34.94) * mm});
            skLineSegment(sketch, "E160", {"start": v(27.7, -18.62) * mm, "end": v(28.7, -19.62) * mm});
            skLineSegment(sketch, "E161", {"start": v(28.7, -37.62) * mm, "end": v(27.7, -38.62) * mm});
            skLineSegment(sketch, "E162", {"start": v(25.7, -18.83) * mm, "end": v(26.44, -18.83) * mm});
            skLineSegment(sketch, "E163", {"start": v(26.44, -18.83) * mm, "end": v(26.44, -18.62) * mm});
            skLineSegment(sketch, "E164", {"start": v(25.7, -18.83) * mm, "end": v(24.94, -18.83) * mm});
            skLineSegment(sketch, "E165", {"start": v(24.94, -18.83) * mm, "end": v(24.94, -18.62) * mm});
            skLineSegment(sketch, "E166", {"start": v(27.7, -18.62) * mm, "end": v(26.44, -18.62) * mm});
            skLineSegment(sketch, "E167", {"start": v(28.5, -21.63) * mm, "end": v(28.5, -22.38) * mm});
            skLineSegment(sketch, "E168", {"start": v(28.5, -22.38) * mm, "end": v(28.7, -22.38) * mm});
            skLineSegment(sketch, "E169", {"start": v(28.5, -21.63) * mm, "end": v(28.5, -20.88) * mm});
            skLineSegment(sketch, "E170", {"start": v(28.5, -20.88) * mm, "end": v(28.7, -20.88) * mm});
            skLineSegment(sketch, "E171", {"start": v(28.5, -35.63) * mm, "end": v(28.5, -34.88) * mm});
            skLineSegment(sketch, "E172", {"start": v(28.5, -34.88) * mm, "end": v(28.7, -34.88) * mm});
            skLineSegment(sketch, "E173", {"start": v(28.5, -35.63) * mm, "end": v(28.5, -36.38) * mm});
            skLineSegment(sketch, "E174", {"start": v(28.5, -36.38) * mm, "end": v(28.7, -36.38) * mm});
            skLineSegment(sketch, "E175", {"start": v(25.7, -38.43) * mm, "end": v(26.44, -38.43) * mm});
            skLineSegment(sketch, "E176", {"start": v(26.44, -38.43) * mm, "end": v(26.44, -38.62) * mm});
            skLineSegment(sketch, "E177", {"start": v(25.7, -38.43) * mm, "end": v(24.94, -38.43) * mm});
            skLineSegment(sketch, "E178", {"start": v(24.94, -38.43) * mm, "end": v(24.94, -38.62) * mm});
            skLineSegment(sketch, "E179", {"start": v(28.7, -19.62) * mm, "end": v(28.7, -20.88) * mm});
            skLineSegment(sketch, "E180", {"start": v(28.7, -22.38) * mm, "end": v(28.7, -26.48) * mm});
            skLineSegment(sketch, "E181", {"start": v(27.7, -38.62) * mm, "end": v(26.44, -38.62) * mm});
            skLineSegment(sketch, "E182", {"start": v(28.7, -37.62) * mm, "end": v(28.7, -36.38) * mm});
            skLineSegment(sketch, "E183", {"start": v(28.7, -34.88) * mm, "end": v(28.7, -30.77) * mm});
            skLineSegment(sketch, "E184", {"start": v(18.7, -13.92) * mm, "end": v(18.7, -42.92) * mm});
            skLineSegment(sketch, "E185", {"start": v(20.84, -18.62) * mm, "end": v(20.84, -20.12) * mm});
            skLineSegment(sketch, "E186", {"start": v(22.84, -20.12) * mm, "end": v(22.84, -24.12) * mm});
            skLineSegment(sketch, "E187", {"start": v(22.84, -20.12) * mm, "end": v(20.84, -20.12) * mm});
            skLineSegment(sketch, "E188", {"start": v(16.54, -18.62) * mm, "end": v(16.54, -20.12) * mm});
            skLineSegment(sketch, "E189", {"start": v(14.54, -20.12) * mm, "end": v(14.54, -24.12) * mm});
            skLineSegment(sketch, "E190", {"start": v(14.54, -20.12) * mm, "end": v(16.54, -20.12) * mm});
            skLineSegment(sketch, "E191", {"start": v(14.54, -24.12) * mm, "end": v(16.2, -24.12) * mm});
            skLineSegment(sketch, "E192", {"start": v(16.2, -24.12) * mm, "end": v(16.2, -25.42) * mm});
            skLineSegment(sketch, "E193", {"start": v(22.84, -24.12) * mm, "end": v(16.2, -25.42) * mm});
            skLineSegment(sketch, "E194", {"start": v(16.54, -38.62) * mm, "end": v(16.54, -37.12) * mm});
            skLineSegment(sketch, "E195", {"start": v(14.54, -37.12) * mm, "end": v(14.54, -33.12) * mm});
            skLineSegment(sketch, "E196", {"start": v(14.54, -37.12) * mm, "end": v(16.54, -37.12) * mm});
            skLineSegment(sketch, "E197", {"start": v(20.84, -38.62) * mm, "end": v(20.84, -37.12) * mm});
            skLineSegment(sketch, "E198", {"start": v(22.84, -37.12) * mm, "end": v(22.84, -33.12) * mm});
            skLineSegment(sketch, "E199", {"start": v(22.84, -37.12) * mm, "end": v(20.84, -37.12) * mm});
            skLineSegment(sketch, "E200", {"start": v(22.84, -33.12) * mm, "end": v(21.2, -33.12) * mm});
            skLineSegment(sketch, "E201", {"start": v(21.2, -33.12) * mm, "end": v(21.2, -31.83) * mm});
            skLineSegment(sketch, "E202", {"start": v(14.54, -33.12) * mm, "end": v(21.2, -31.83) * mm});
            skLineSegment(sketch, "E203", {"start": v(24.94, -18.62) * mm, "end": v(20.84, -18.62) * mm});
            skLineSegment(sketch, "E204", {"start": v(24.94, -38.62) * mm, "end": v(20.84, -38.62) * mm});
            skLineSegment(sketch, "E205", {"start": v(6.1, -28.62) * mm, "end": v(31.6, -28.62) * mm});
            skLineSegment(sketch, "E206", {"start": v(11.7, -17.22) * mm, "end": v(11.7, -25.12) * mm});
            skLineSegment(sketch, "E207", {"start": v(15.3, -21.63) * mm, "end": v(6.5, -21.63) * mm});
            skLineSegment(sketch, "E208", {"start": v(10.04, -20.94) * mm, "end": v(11, -19.97) * mm});
            skLineSegment(sketch, "E209", {"start": v(11, -19.97) * mm, "end": v(12.38, -19.97) * mm});
            skLineSegment(sketch, "E210", {"start": v(12.38, -19.97) * mm, "end": v(13.34, -20.94) * mm});
            skLineSegment(sketch, "E211", {"start": v(13.34, -20.94) * mm, "end": v(13.34, -22.3) * mm});
            skLineSegment(sketch, "E212", {"start": v(13.34, -22.3) * mm, "end": v(12.38, -23.28) * mm});
            skLineSegment(sketch, "E213", {"start": v(12.38, -23.28) * mm, "end": v(11, -23.28) * mm});
            skLineSegment(sketch, "E214", {"start": v(11, -23.28) * mm, "end": v(10.04, -22.3) * mm});
            skLineSegment(sketch, "E215", {"start": v(10.04, -22.3) * mm, "end": v(10.04, -20.94) * mm});
            skLineSegment(sketch, "E216", {"start": v(9.7, -18.62) * mm, "end": v(8.7, -19.62) * mm});
            skLineSegment(sketch, "E217", {"start": v(11.7, -18.83) * mm, "end": v(10.94, -18.83) * mm});
            skLineSegment(sketch, "E218", {"start": v(10.94, -18.83) * mm, "end": v(10.94, -18.62) * mm});
            skLineSegment(sketch, "E219", {"start": v(11.7, -18.83) * mm, "end": v(12.44, -18.83) * mm});
            skLineSegment(sketch, "E220", {"start": v(12.44, -18.83) * mm, "end": v(12.44, -18.62) * mm});
            skLineSegment(sketch, "E221", {"start": v(9.7, -18.62) * mm, "end": v(10.94, -18.62) * mm});
            skLineSegment(sketch, "E222", {"start": v(8.9, -21.63) * mm, "end": v(8.9, -22.38) * mm});
            skLineSegment(sketch, "E223", {"start": v(8.9, -22.38) * mm, "end": v(8.7, -22.38) * mm});
            skLineSegment(sketch, "E224", {"start": v(8.9, -21.63) * mm, "end": v(8.9, -20.88) * mm});
            skLineSegment(sketch, "E225", {"start": v(8.9, -20.88) * mm, "end": v(8.7, -20.88) * mm});
            skLineSegment(sketch, "E226", {"start": v(8.7, -19.62) * mm, "end": v(8.7, -20.88) * mm});
            skLineSegment(sketch, "E227", {"start": v(8.7, -22.38) * mm, "end": v(8.7, -26.48) * mm});
            skLineSegment(sketch, "E228", {"start": v(12.44, -18.62) * mm, "end": v(16.54, -18.62) * mm});
            skLineSegment(sketch, "E229", {"start": v(11.7, -40.02) * mm, "end": v(11.7, -32.12) * mm});
            skLineSegment(sketch, "E230", {"start": v(15.3, -35.63) * mm, "end": v(6.5, -35.63) * mm});
            skLineSegment(sketch, "E231", {"start": v(10.04, -34.94) * mm, "end": v(11, -33.98) * mm});
            skLineSegment(sketch, "E232", {"start": v(11, -33.98) * mm, "end": v(12.38, -33.98) * mm});
            skLineSegment(sketch, "E233", {"start": v(12.38, -33.98) * mm, "end": v(13.34, -34.94) * mm});
            skLineSegment(sketch, "E234", {"start": v(13.34, -34.94) * mm, "end": v(13.34, -36.3) * mm});
            skLineSegment(sketch, "E235", {"start": v(13.34, -36.3) * mm, "end": v(12.38, -37.28) * mm});
            skLineSegment(sketch, "E236", {"start": v(12.38, -37.28) * mm, "end": v(11, -37.28) * mm});
            skLineSegment(sketch, "E237", {"start": v(11, -37.28) * mm, "end": v(10.04, -36.3) * mm});
            skLineSegment(sketch, "E238", {"start": v(10.04, -36.3) * mm, "end": v(10.04, -34.94) * mm});
            skLineSegment(sketch, "E239", {"start": v(8.7, -37.62) * mm, "end": v(9.7, -38.62) * mm});
            skLineSegment(sketch, "E240", {"start": v(8.9, -35.63) * mm, "end": v(8.9, -34.88) * mm});
            skLineSegment(sketch, "E241", {"start": v(8.9, -34.88) * mm, "end": v(8.7, -34.88) * mm});
            skLineSegment(sketch, "E242", {"start": v(8.9, -35.63) * mm, "end": v(8.9, -36.38) * mm});
            skLineSegment(sketch, "E243", {"start": v(8.9, -36.38) * mm, "end": v(8.7, -36.38) * mm});
            skLineSegment(sketch, "E244", {"start": v(11.7, -38.43) * mm, "end": v(10.94, -38.43) * mm});
            skLineSegment(sketch, "E245", {"start": v(10.94, -38.43) * mm, "end": v(10.94, -38.62) * mm});
            skLineSegment(sketch, "E246", {"start": v(11.7, -38.43) * mm, "end": v(12.44, -38.43) * mm});
            skLineSegment(sketch, "E247", {"start": v(12.44, -38.43) * mm, "end": v(12.44, -38.62) * mm});
            skLineSegment(sketch, "E248", {"start": v(9.7, -38.62) * mm, "end": v(10.94, -38.62) * mm});
            skLineSegment(sketch, "E249", {"start": v(8.7, -37.62) * mm, "end": v(8.7, -36.38) * mm});
            skLineSegment(sketch, "E250", {"start": v(8.7, -34.88) * mm, "end": v(8.7, -30.77) * mm});
            skLineSegment(sketch, "E251", {"start": v(12.44, -38.62) * mm, "end": v(16.54, -38.62) * mm});
            skLineSegment(sketch, "E252", {"start": v(8.7, -26.48) * mm, "end": v(10.2, -26.48) * mm});
            skLineSegment(sketch, "E253", {"start": v(10.2, -24.48) * mm, "end": v(14.2, -24.48) * mm});
            skLineSegment(sketch, "E254", {"start": v(10.2, -24.48) * mm, "end": v(10.2, -26.48) * mm});
            skLineSegment(sketch, "E255", {"start": v(8.7, -30.77) * mm, "end": v(10.2, -30.77) * mm});
            skLineSegment(sketch, "E256", {"start": v(10.2, -32.77) * mm, "end": v(14.2, -32.77) * mm});
            skLineSegment(sketch, "E257", {"start": v(10.2, -32.77) * mm, "end": v(10.2, -30.77) * mm});
            skLineSegment(sketch, "E258", {"start": v(14.2, -32.77) * mm, "end": v(14.2, -31.12) * mm});
            skLineSegment(sketch, "E259", {"start": v(14.2, -31.12) * mm, "end": v(15.5, -31.12) * mm});
            skLineSegment(sketch, "E260", {"start": v(14.2, -24.48) * mm, "end": v(15.5, -31.12) * mm});
            skCircle(sketch, "E261", {"center": v(18.7, -28.62) * mm, "radius": 1.6 * mm});
            skSolve(sketch);
        }
        {
            var Q0;
            {var subQ21=sQuery(id+"F5.wireOp",EDGE,"E141");Q0=makeQuery(id+"F5.imprint","IMPRINT",FACE,{"disambiguationData":[TD([[makeQuery(id+"F5.imprint","IMPRINT",EDGE,{"derivedFrom":subQ21}),-1.0]])]});}
            var Q1;
            {var subQ9=sQuery(id+"F5.wireOp",EDGE,"E154");Q1=makeQuery(id+"F5.imprint","IMPRINT",FACE,{"disambiguationData":[TD([[makeQuery(id+"F5.imprint","IMPRINT",EDGE,{"derivedFrom":subQ9}),-1.0]])]});}
            var Q2;
            {var subQ21=sQuery(id+"F5.wireOp",EDGE,"E191");Q2=makeQuery(id+"F5.imprint","IMPRINT",FACE,{"disambiguationData":[TD([[makeQuery(id+"F5.imprint","IMPRINT",EDGE,{"derivedFrom":subQ21}),-1.0]])]});}
            var Q3;
            {var subQ1=sQuery(id+"F5.wireOp",EDGE,"E233");Q3=makeQuery(id+"F5.imprint","IMPRINT",FACE,{"disambiguationData":[TD([[makeQuery(id+"F5.imprint","IMPRINT",EDGE,{"derivedFrom":subQ1}),1.0]])]});}
            var Q4;
            Q4=makeQuery(id+"F5.imprint","IMPRINT",FACE,{"disambiguationData":[TD([[makeQuery(id+"F5.imprint","IMPRINT",EDGE,{"derivedFrom":sQuery(id+"F5.wireOp",EDGE,"E194")}),1.0]])]});
            var Q5;
            {var subQ0=sQuery(id+"F5.wireOp",EDGE,"E261");var subQ1=sQuery(id+"F5.wireOp",EDGE,"E184");var subQ2=makeQuery(id+"F5.imprint","INTERSECT",VERTEX,{"disambiguationData":[OD(0.0)],"derivedFrom":[subQ1,subQ0]});Q5=makeQuery(id+"F5.imprint","IMPRINT",FACE,{"disambiguationData":[TD([[makeQuery(id+"F5.imprint","IMPRINT",EDGE,{"disambiguationData":[TD([[subQ2,-1.0]])],"derivedFrom":subQ1}),1.0]])]});}
            var Q6;
            {var subQ0=sQuery(id+"F5.wireOp",EDGE,"E205");var subQ1=sQuery(id+"F5.wireOp",EDGE,"E184");var subQ2=makeQuery(id+"F5.imprint","INTERSECT",VERTEX,{"derivedFrom":[subQ1,subQ0]});Q6=makeQuery(id+"F5.imprint","IMPRINT",FACE,{"disambiguationData":[TD([[makeQuery(id+"F5.imprint","IMPRINT",EDGE,{"disambiguationData":[TD([[subQ2,-1.0]])],"derivedFrom":subQ1}),-1.0]])]});}
            var Q7;
            {var subQ0=sQuery(id+"F5.wireOp",EDGE,"E205");var subQ1=sQuery(id+"F5.wireOp",EDGE,"E184");var subQ2=makeQuery(id+"F5.imprint","INTERSECT",VERTEX,{"derivedFrom":[subQ1,subQ0]});Q7=makeQuery(id+"F5.imprint","IMPRINT",FACE,{"disambiguationData":[TD([[makeQuery(id+"F5.imprint","IMPRINT",EDGE,{"disambiguationData":[TD([[subQ2,-1.0]])],"derivedFrom":subQ1}),1.0]])]});}
            var Q8;
            Q8=makeQuery(id+"F5.imprint","IMPRINT",FACE,{"disambiguationData":[TD([[makeQuery(id+"F5.imprint","IMPRINT",EDGE,{"derivedFrom":sQuery(id+"F5.wireOp",EDGE,"E188")}),-1.0]])]});
            var Q9;
            {var subQ0=sQuery(id+"F5.wireOp",EDGE,"E261");var subQ1=sQuery(id+"F5.wireOp",EDGE,"E184");var subQ2=makeQuery(id+"F5.imprint","INTERSECT",VERTEX,{"disambiguationData":[OD(0.0)],"derivedFrom":[subQ1,subQ0]});Q9=makeQuery(id+"F5.imprint","IMPRINT",FACE,{"disambiguationData":[TD([[makeQuery(id+"F5.imprint","IMPRINT",EDGE,{"disambiguationData":[TD([[subQ2,-1.0]])],"derivedFrom":subQ1}),-1.0]])]});}
            var Q10;
            {var subQ3=sQuery(id+"F5.wireOp",EDGE,"E146");Q10=makeQuery(id+"F5.imprint","IMPRINT",FACE,{"disambiguationData":[TD([[makeQuery(id+"F5.imprint","IMPRINT",EDGE,{"derivedFrom":subQ3}),-1.0]])]});}
            var Q11;
            {var subQ5=sQuery(id+"F5.wireOp",EDGE,"E156");Q11=makeQuery(id+"F5.imprint","IMPRINT",FACE,{"disambiguationData":[TD([[makeQuery(id+"F5.imprint","IMPRINT",EDGE,{"derivedFrom":subQ5}),-1.0]])]});}
            var Q12;
            {var subQ8=sQuery(id+"F5.wireOp",EDGE,"E208");Q12=makeQuery(id+"F5.imprint","IMPRINT",FACE,{"disambiguationData":[TD([[makeQuery(id+"F5.imprint","IMPRINT",EDGE,{"derivedFrom":subQ8}),1.0]])]});}
            var Q13;
            {var subQ0=sQuery(id+"F5.wireOp",EDGE,"E210");Q13=makeQuery(id+"F5.imprint","IMPRINT",FACE,{"disambiguationData":[TD([[makeQuery(id+"F5.imprint","IMPRINT",EDGE,{"derivedFrom":subQ0}),-1.0]])]});}
            var Q14;
            {var subQ1=sQuery(id+"F5.wireOp",EDGE,"E208");Q14=makeQuery(id+"F5.imprint","IMPRINT",FACE,{"disambiguationData":[TD([[makeQuery(id+"F5.imprint","IMPRINT",EDGE,{"derivedFrom":subQ1}),-1.0]])]});}
            var Q15;
            {var subQ0=sQuery(id+"F5.wireOp",EDGE,"E212");Q15=makeQuery(id+"F5.imprint","IMPRINT",FACE,{"disambiguationData":[TD([[makeQuery(id+"F5.imprint","IMPRINT",EDGE,{"derivedFrom":subQ0}),-1.0]])]});}
            var Q16;
            {var subQ0=sQuery(id+"F5.wireOp",EDGE,"E214");Q16=makeQuery(id+"F5.imprint","IMPRINT",FACE,{"disambiguationData":[TD([[makeQuery(id+"F5.imprint","IMPRINT",EDGE,{"derivedFrom":subQ0}),-1.0]])]});}
            var Q17;
            {var subQ8=sQuery(id+"F5.wireOp",EDGE,"E214");Q17=makeQuery(id+"F5.imprint","IMPRINT",FACE,{"disambiguationData":[TD([[makeQuery(id+"F5.imprint","IMPRINT",EDGE,{"derivedFrom":subQ8}),1.0]])]});}
            var Q18;
            {var subQ8=sQuery(id+"F5.wireOp",EDGE,"E231");Q18=makeQuery(id+"F5.imprint","IMPRINT",FACE,{"disambiguationData":[TD([[makeQuery(id+"F5.imprint","IMPRINT",EDGE,{"derivedFrom":subQ8}),1.0]])]});}
            var Q19;
            {var subQ0=sQuery(id+"F5.wireOp",EDGE,"E233");Q19=makeQuery(id+"F5.imprint","IMPRINT",FACE,{"disambiguationData":[TD([[makeQuery(id+"F5.imprint","IMPRINT",EDGE,{"derivedFrom":subQ0}),-1.0]])]});}
            var Q20;
            Q20=makeQuery(id+"F5.imprint","IMPRINT",FACE,{"disambiguationData":[TD([[makeQuery(id+"F5.imprint","IMPRINT",EDGE,{"derivedFrom":sQuery(id+"F5.wireOp",EDGE,"E135")}),1.0]])]});
            var Q21;
            {var subQ2=sQuery(id+"F5.wireOp",EDGE,"E144");Q21=makeQuery(id+"F5.imprint","IMPRINT",FACE,{"disambiguationData":[TD([[makeQuery(id+"F5.imprint","IMPRINT",EDGE,{"derivedFrom":subQ2}),-1.0]])]});}
            var Q22;
            {var subQ0=sQuery(id+"F5.wireOp",EDGE,"E146");Q22=makeQuery(id+"F5.imprint","IMPRINT",FACE,{"disambiguationData":[TD([[makeQuery(id+"F5.imprint","IMPRINT",EDGE,{"derivedFrom":subQ0}),1.0]])]});}
            var Q23;
            {var subQ0=sQuery(id+"F5.wireOp",EDGE,"E235");Q23=makeQuery(id+"F5.imprint","IMPRINT",FACE,{"disambiguationData":[TD([[makeQuery(id+"F5.imprint","IMPRINT",EDGE,{"derivedFrom":subQ0}),-1.0]])]});}
            var Q24;
            {var subQ1=sQuery(id+"F5.wireOp",EDGE,"E144");Q24=makeQuery(id+"F5.imprint","IMPRINT",FACE,{"disambiguationData":[TD([[makeQuery(id+"F5.imprint","IMPRINT",EDGE,{"derivedFrom":subQ1}),1.0]])]});}
            var Q25;
            {var subQ0=sQuery(id+"F5.wireOp",EDGE,"E148");Q25=makeQuery(id+"F5.imprint","IMPRINT",FACE,{"disambiguationData":[TD([[makeQuery(id+"F5.imprint","IMPRINT",EDGE,{"derivedFrom":subQ0}),1.0]])]});}
            var Q26;
            {var subQ0=sQuery(id+"F5.wireOp",EDGE,"E150");Q26=makeQuery(id+"F5.imprint","IMPRINT",FACE,{"disambiguationData":[TD([[makeQuery(id+"F5.imprint","IMPRINT",EDGE,{"derivedFrom":subQ0}),1.0]])]});}
            var Q27;
            Q27=makeQuery(id+"F5.imprint","IMPRINT",FACE,{"disambiguationData":[TD([[makeQuery(id+"F5.imprint","IMPRINT",EDGE,{"derivedFrom":sQuery(id+"F5.wireOp",EDGE,"E138")}),-1.0]])]});
            var Q28;
            {var subQ3=sQuery(id+"F5.wireOp",EDGE,"E158");Q28=makeQuery(id+"F5.imprint","IMPRINT",FACE,{"disambiguationData":[TD([[makeQuery(id+"F5.imprint","IMPRINT",EDGE,{"derivedFrom":subQ3}),-1.0]])]});}
            var Q29;
            {var subQ0=sQuery(id+"F5.wireOp",EDGE,"E156");Q29=makeQuery(id+"F5.imprint","IMPRINT",FACE,{"disambiguationData":[TD([[makeQuery(id+"F5.imprint","IMPRINT",EDGE,{"derivedFrom":subQ0}),1.0]])]});}
            var Q30;
            {var subQ1=sQuery(id+"F5.wireOp",EDGE,"E231");Q30=makeQuery(id+"F5.imprint","IMPRINT",FACE,{"disambiguationData":[TD([[makeQuery(id+"F5.imprint","IMPRINT",EDGE,{"derivedFrom":subQ1}),-1.0]])]});}
            var Q31;
            {var subQ0=sQuery(id+"F5.wireOp",EDGE,"E158");Q31=makeQuery(id+"F5.imprint","IMPRINT",FACE,{"disambiguationData":[TD([[makeQuery(id+"F5.imprint","IMPRINT",EDGE,{"derivedFrom":subQ0}),1.0]])]});}
            var Q32;
            {var subQ0=sQuery(id+"F5.wireOp",EDGE,"E154");Q32=makeQuery(id+"F5.imprint","IMPRINT",FACE,{"disambiguationData":[TD([[makeQuery(id+"F5.imprint","IMPRINT",EDGE,{"derivedFrom":subQ0}),1.0]])]});}
            var Q33;
            {var subQ1=sQuery(id+"F5.wireOp",EDGE,"E152");Q33=makeQuery(id+"F5.imprint","IMPRINT",FACE,{"disambiguationData":[TD([[makeQuery(id+"F5.imprint","IMPRINT",EDGE,{"derivedFrom":subQ1}),1.0]])]});}
            var Q34;
            {var subQ0=sQuery(id+"F5.wireOp",EDGE,"E237");Q34=makeQuery(id+"F5.imprint","IMPRINT",FACE,{"disambiguationData":[TD([[makeQuery(id+"F5.imprint","IMPRINT",EDGE,{"derivedFrom":subQ0}),-1.0]])]});}
            var Q35;
            {var subQ6=sQuery(id+"F5.wireOp",EDGE,"E237");Q35=makeQuery(id+"F5.imprint","IMPRINT",FACE,{"disambiguationData":[TD([[makeQuery(id+"F5.imprint","IMPRINT",EDGE,{"derivedFrom":subQ6}),1.0]])]});}
            extrude(context, id + "F6", {"entities" : qUnion([Q0, Q1, Q2, Q3, Q4, Q5, Q6, Q7, Q8, Q9, Q10, Q11, Q12, Q13, Q14, Q15, Q16, Q17, Q18, Q19, Q20, Q21, Q22, Q23, Q24, Q25, Q26, Q27, Q28, Q29, Q30, Q31, Q32, Q33, Q34, Q35]), "oppositeDirection" : true, "depth" : 730 * mm, "offsetDistance" : 25 * mm});
        }
        {
            var Q0;
            Q0=makeQuery(id+"F6.opExtrude","SWEPT_BODY",BODY,{"disambiguationData":[OSD([sQuery(id+"F5.wireOp",EDGE,"E135"),sQuery(id+"F5.wireOp",EDGE,"E136"),sQuery(id+"F5.wireOp",EDGE,"E137"),sQuery(id+"F5.wireOp",EDGE,"E138"),sQuery(id+"F5.wireOp",EDGE,"E139"),sQuery(id+"F5.wireOp",EDGE,"E140"),sQuery(id+"F5.wireOp",EDGE,"E141"),sQuery(id+"F5.wireOp",EDGE,"E142"),sQuery(id+"F5.wireOp",EDGE,"E143"),sQuery(id+"F5.wireOp",EDGE,"E160"),sQuery(id+"F5.wireOp",EDGE,"E161"),sQuery(id+"F5.wireOp",EDGE,"E162"),sQuery(id+"F5.wireOp",EDGE,"E163"),sQuery(id+"F5.wireOp",EDGE,"E164"),sQuery(id+"F5.wireOp",EDGE,"E165"),sQuery(id+"F5.wireOp",EDGE,"E166"),sQuery(id+"F5.wireOp",EDGE,"E167"),sQuery(id+"F5.wireOp",EDGE,"E168"),sQuery(id+"F5.wireOp",EDGE,"E169"),sQuery(id+"F5.wireOp",EDGE,"E170"),sQuery(id+"F5.wireOp",EDGE,"E171"),sQuery(id+"F5.wireOp",EDGE,"E172"),sQuery(id+"F5.wireOp",EDGE,"E173"),sQuery(id+"F5.wireOp",EDGE,"E174"),sQuery(id+"F5.wireOp",EDGE,"E175"),sQuery(id+"F5.wireOp",EDGE,"E176"),sQuery(id+"F5.wireOp",EDGE,"E177"),sQuery(id+"F5.wireOp",EDGE,"E178"),sQuery(id+"F5.wireOp",EDGE,"E179"),sQuery(id+"F5.wireOp",EDGE,"E180"),sQuery(id+"F5.wireOp",EDGE,"E181"),sQuery(id+"F5.wireOp",EDGE,"E182"),sQuery(id+"F5.wireOp",EDGE,"E183"),sQuery(id+"F5.wireOp",EDGE,"E185"),sQuery(id+"F5.wireOp",EDGE,"E186"),sQuery(id+"F5.wireOp",EDGE,"E187"),sQuery(id+"F5.wireOp",EDGE,"E188"),sQuery(id+"F5.wireOp",EDGE,"E189"),sQuery(id+"F5.wireOp",EDGE,"E190"),sQuery(id+"F5.wireOp",EDGE,"E191"),sQuery(id+"F5.wireOp",EDGE,"E192"),sQuery(id+"F5.wireOp",EDGE,"E193"),sQuery(id+"F5.wireOp",EDGE,"E194"),sQuery(id+"F5.wireOp",EDGE,"E195"),sQuery(id+"F5.wireOp",EDGE,"E196"),sQuery(id+"F5.wireOp",EDGE,"E197"),sQuery(id+"F5.wireOp",EDGE,"E198"),sQuery(id+"F5.wireOp",EDGE,"E199"),sQuery(id+"F5.wireOp",EDGE,"E200"),sQuery(id+"F5.wireOp",EDGE,"E201"),sQuery(id+"F5.wireOp",EDGE,"E202"),sQuery(id+"F5.wireOp",EDGE,"E203"),sQuery(id+"F5.wireOp",EDGE,"E204"),sQuery(id+"F5.wireOp",EDGE,"E216"),sQuery(id+"F5.wireOp",EDGE,"E217"),sQuery(id+"F5.wireOp",EDGE,"E218"),sQuery(id+"F5.wireOp",EDGE,"E219"),sQuery(id+"F5.wireOp",EDGE,"E220"),sQuery(id+"F5.wireOp",EDGE,"E221"),sQuery(id+"F5.wireOp",EDGE,"E222"),sQuery(id+"F5.wireOp",EDGE,"E223"),sQuery(id+"F5.wireOp",EDGE,"E224"),sQuery(id+"F5.wireOp",EDGE,"E225"),sQuery(id+"F5.wireOp",EDGE,"E226"),sQuery(id+"F5.wireOp",EDGE,"E227"),sQuery(id+"F5.wireOp",EDGE,"E228"),sQuery(id+"F5.wireOp",EDGE,"E239"),sQuery(id+"F5.wireOp",EDGE,"E240"),sQuery(id+"F5.wireOp",EDGE,"E241"),sQuery(id+"F5.wireOp",EDGE,"E242"),sQuery(id+"F5.wireOp",EDGE,"E243"),sQuery(id+"F5.wireOp",EDGE,"E244"),sQuery(id+"F5.wireOp",EDGE,"E245"),sQuery(id+"F5.wireOp",EDGE,"E246"),sQuery(id+"F5.wireOp",EDGE,"E247"),sQuery(id+"F5.wireOp",EDGE,"E248"),sQuery(id+"F5.wireOp",EDGE,"E249"),sQuery(id+"F5.wireOp",EDGE,"E250"),sQuery(id+"F5.wireOp",EDGE,"E251"),sQuery(id+"F5.wireOp",EDGE,"E252"),sQuery(id+"F5.wireOp",EDGE,"E253"),sQuery(id+"F5.wireOp",EDGE,"E254"),sQuery(id+"F5.wireOp",EDGE,"E255"),sQuery(id+"F5.wireOp",EDGE,"E256"),sQuery(id+"F5.wireOp",EDGE,"E257"),sQuery(id+"F5.wireOp",EDGE,"E258"),sQuery(id+"F5.wireOp",EDGE,"E259"),sQuery(id+"F5.wireOp",EDGE,"E260")])]});
            transform(context, id + "F7", {"entities" : qUnion([Q0]), "transformType" : TransformType.TRANSLATION_3D, "dx" : 0 * mm, "dy" : -47.3 * mm, "dz" : 38.65 * mm, "makeCopy" : false});
        }
        {
            var Q0;
            Q0=makeQuery(id+"F6.opExtrude","SWEPT_BODY",BODY,{"disambiguationData":[OSD([sQuery(id+"F5.wireOp",EDGE,"E135"),sQuery(id+"F5.wireOp",EDGE,"E136"),sQuery(id+"F5.wireOp",EDGE,"E137"),sQuery(id+"F5.wireOp",EDGE,"E138"),sQuery(id+"F5.wireOp",EDGE,"E139"),sQuery(id+"F5.wireOp",EDGE,"E140"),sQuery(id+"F5.wireOp",EDGE,"E141"),sQuery(id+"F5.wireOp",EDGE,"E142"),sQuery(id+"F5.wireOp",EDGE,"E143"),sQuery(id+"F5.wireOp",EDGE,"E160"),sQuery(id+"F5.wireOp",EDGE,"E161"),sQuery(id+"F5.wireOp",EDGE,"E162"),sQuery(id+"F5.wireOp",EDGE,"E163"),sQuery(id+"F5.wireOp",EDGE,"E164"),sQuery(id+"F5.wireOp",EDGE,"E165"),sQuery(id+"F5.wireOp",EDGE,"E166"),sQuery(id+"F5.wireOp",EDGE,"E167"),sQuery(id+"F5.wireOp",EDGE,"E168"),sQuery(id+"F5.wireOp",EDGE,"E169"),sQuery(id+"F5.wireOp",EDGE,"E170"),sQuery(id+"F5.wireOp",EDGE,"E171"),sQuery(id+"F5.wireOp",EDGE,"E172"),sQuery(id+"F5.wireOp",EDGE,"E173"),sQuery(id+"F5.wireOp",EDGE,"E174"),sQuery(id+"F5.wireOp",EDGE,"E175"),sQuery(id+"F5.wireOp",EDGE,"E176"),sQuery(id+"F5.wireOp",EDGE,"E177"),sQuery(id+"F5.wireOp",EDGE,"E178"),sQuery(id+"F5.wireOp",EDGE,"E179"),sQuery(id+"F5.wireOp",EDGE,"E180"),sQuery(id+"F5.wireOp",EDGE,"E181"),sQuery(id+"F5.wireOp",EDGE,"E182"),sQuery(id+"F5.wireOp",EDGE,"E183"),sQuery(id+"F5.wireOp",EDGE,"E185"),sQuery(id+"F5.wireOp",EDGE,"E186"),sQuery(id+"F5.wireOp",EDGE,"E187"),sQuery(id+"F5.wireOp",EDGE,"E188"),sQuery(id+"F5.wireOp",EDGE,"E189"),sQuery(id+"F5.wireOp",EDGE,"E190"),sQuery(id+"F5.wireOp",EDGE,"E191"),sQuery(id+"F5.wireOp",EDGE,"E192"),sQuery(id+"F5.wireOp",EDGE,"E193"),sQuery(id+"F5.wireOp",EDGE,"E194"),sQuery(id+"F5.wireOp",EDGE,"E195"),sQuery(id+"F5.wireOp",EDGE,"E196"),sQuery(id+"F5.wireOp",EDGE,"E197"),sQuery(id+"F5.wireOp",EDGE,"E198"),sQuery(id+"F5.wireOp",EDGE,"E199"),sQuery(id+"F5.wireOp",EDGE,"E200"),sQuery(id+"F5.wireOp",EDGE,"E201"),sQuery(id+"F5.wireOp",EDGE,"E202"),sQuery(id+"F5.wireOp",EDGE,"E203"),sQuery(id+"F5.wireOp",EDGE,"E204"),sQuery(id+"F5.wireOp",EDGE,"E216"),sQuery(id+"F5.wireOp",EDGE,"E217"),sQuery(id+"F5.wireOp",EDGE,"E218"),sQuery(id+"F5.wireOp",EDGE,"E219"),sQuery(id+"F5.wireOp",EDGE,"E220"),sQuery(id+"F5.wireOp",EDGE,"E221"),sQuery(id+"F5.wireOp",EDGE,"E222"),sQuery(id+"F5.wireOp",EDGE,"E223"),sQuery(id+"F5.wireOp",EDGE,"E224"),sQuery(id+"F5.wireOp",EDGE,"E225"),sQuery(id+"F5.wireOp",EDGE,"E226"),sQuery(id+"F5.wireOp",EDGE,"E227"),sQuery(id+"F5.wireOp",EDGE,"E228"),sQuery(id+"F5.wireOp",EDGE,"E239"),sQuery(id+"F5.wireOp",EDGE,"E240"),sQuery(id+"F5.wireOp",EDGE,"E241"),sQuery(id+"F5.wireOp",EDGE,"E242"),sQuery(id+"F5.wireOp",EDGE,"E243"),sQuery(id+"F5.wireOp",EDGE,"E244"),sQuery(id+"F5.wireOp",EDGE,"E245"),sQuery(id+"F5.wireOp",EDGE,"E246"),sQuery(id+"F5.wireOp",EDGE,"E247"),sQuery(id+"F5.wireOp",EDGE,"E248"),sQuery(id+"F5.wireOp",EDGE,"E249"),sQuery(id+"F5.wireOp",EDGE,"E250"),sQuery(id+"F5.wireOp",EDGE,"E251"),sQuery(id+"F5.wireOp",EDGE,"E252"),sQuery(id+"F5.wireOp",EDGE,"E253"),sQuery(id+"F5.wireOp",EDGE,"E254"),sQuery(id+"F5.wireOp",EDGE,"E255"),sQuery(id+"F5.wireOp",EDGE,"E256"),sQuery(id+"F5.wireOp",EDGE,"E257"),sQuery(id+"F5.wireOp",EDGE,"E258"),sQuery(id+"F5.wireOp",EDGE,"E259"),sQuery(id+"F5.wireOp",EDGE,"E260")])]});
            transform(context, id + "F8", {"entities" : qUnion([Q0]), "transformType" : TransformType.TRANSLATION_3D, "dx" : 0 * mm, "dy" : 650 * mm, "dz" : 0 * mm, "makeCopy" : true});
        }
        {
            var Q0;
            Q0=qCreatedBy(id+"F4.planeOp",FACE);
            var sketch = newSketch(context, id + "F9", { "sketchPlane" : qUnion([Q0])});
            skLineSegment(sketch, "E262", {"start": v(25.7, -17.22) * mm, "end": v(25.7, -25.12) * mm});
            skLineSegment(sketch, "E263", {"start": v(22.1, -21.63) * mm, "end": v(30.9, -21.63) * mm});
            skLineSegment(sketch, "E264", {"start": v(25.7, -40.02) * mm, "end": v(25.7, -32.12) * mm});
            skLineSegment(sketch, "E265", {"start": v(22.1, -35.63) * mm, "end": v(30.9, -35.63) * mm});
            skLineSegment(sketch, "E266", {"start": v(28.7, -30.77) * mm, "end": v(27.2, -30.77) * mm});
            skLineSegment(sketch, "E267", {"start": v(27.2, -32.77) * mm, "end": v(23.2, -32.77) * mm});
            skLineSegment(sketch, "E268", {"start": v(27.2, -32.77) * mm, "end": v(27.2, -30.77) * mm});
            skLineSegment(sketch, "E269", {"start": v(28.7, -26.48) * mm, "end": v(27.2, -26.48) * mm});
            skLineSegment(sketch, "E270", {"start": v(27.2, -24.48) * mm, "end": v(23.2, -24.48) * mm});
            skLineSegment(sketch, "E271", {"start": v(27.2, -24.48) * mm, "end": v(27.2, -26.48) * mm});
            skLineSegment(sketch, "E272", {"start": v(23.2, -24.48) * mm, "end": v(23.2, -26.12) * mm});
            skLineSegment(sketch, "E273", {"start": v(23.2, -26.12) * mm, "end": v(21.9, -26.12) * mm});
            skLineSegment(sketch, "E274", {"start": v(23.2, -32.77) * mm, "end": v(21.9, -26.12) * mm});
            skLineSegment(sketch, "E275", {"start": v(27.34, -20.94) * mm, "end": v(26.38, -19.97) * mm});
            skLineSegment(sketch, "E276", {"start": v(26.38, -19.97) * mm, "end": v(25, -19.97) * mm});
            skLineSegment(sketch, "E277", {"start": v(25, -19.97) * mm, "end": v(24.04, -20.94) * mm});
            skLineSegment(sketch, "E278", {"start": v(24.04, -20.94) * mm, "end": v(24.04, -22.3) * mm});
            skLineSegment(sketch, "E279", {"start": v(24.04, -22.3) * mm, "end": v(25, -23.28) * mm});
            skLineSegment(sketch, "E280", {"start": v(25, -23.28) * mm, "end": v(26.38, -23.28) * mm});
            skLineSegment(sketch, "E281", {"start": v(26.38, -23.28) * mm, "end": v(27.34, -22.3) * mm});
            skLineSegment(sketch, "E282", {"start": v(27.34, -22.3) * mm, "end": v(27.34, -20.94) * mm});
            skLineSegment(sketch, "E283", {"start": v(27.34, -34.94) * mm, "end": v(26.38, -33.98) * mm});
            skLineSegment(sketch, "E284", {"start": v(26.38, -33.98) * mm, "end": v(25, -33.98) * mm});
            skLineSegment(sketch, "E285", {"start": v(25, -33.98) * mm, "end": v(24.04, -34.94) * mm});
            skLineSegment(sketch, "E286", {"start": v(24.04, -34.94) * mm, "end": v(24.04, -36.3) * mm});
            skLineSegment(sketch, "E287", {"start": v(24.04, -36.3) * mm, "end": v(25, -37.28) * mm});
            skLineSegment(sketch, "E288", {"start": v(25, -37.28) * mm, "end": v(26.38, -37.28) * mm});
            skLineSegment(sketch, "E289", {"start": v(26.38, -37.28) * mm, "end": v(27.34, -36.3) * mm});
            skLineSegment(sketch, "E290", {"start": v(27.34, -36.3) * mm, "end": v(27.34, -34.94) * mm});
            skLineSegment(sketch, "E291", {"start": v(27.7, -18.62) * mm, "end": v(28.7, -19.62) * mm});
            skLineSegment(sketch, "E292", {"start": v(28.7, -37.62) * mm, "end": v(27.7, -38.62) * mm});
            skLineSegment(sketch, "E293", {"start": v(25.7, -18.83) * mm, "end": v(26.44, -18.83) * mm});
            skLineSegment(sketch, "E294", {"start": v(26.44, -18.83) * mm, "end": v(26.44, -18.62) * mm});
            skLineSegment(sketch, "E295", {"start": v(25.7, -18.83) * mm, "end": v(24.94, -18.83) * mm});
            skLineSegment(sketch, "E296", {"start": v(24.94, -18.83) * mm, "end": v(24.94, -18.62) * mm});
            skLineSegment(sketch, "E297", {"start": v(27.7, -18.62) * mm, "end": v(26.44, -18.62) * mm});
            skLineSegment(sketch, "E298", {"start": v(28.5, -21.63) * mm, "end": v(28.5, -22.38) * mm});
            skLineSegment(sketch, "E299", {"start": v(28.5, -22.38) * mm, "end": v(28.7, -22.38) * mm});
            skLineSegment(sketch, "E300", {"start": v(28.5, -21.63) * mm, "end": v(28.5, -20.88) * mm});
            skLineSegment(sketch, "E301", {"start": v(28.5, -20.88) * mm, "end": v(28.7, -20.88) * mm});
            skLineSegment(sketch, "E302", {"start": v(28.5, -35.63) * mm, "end": v(28.5, -34.88) * mm});
            skLineSegment(sketch, "E303", {"start": v(28.5, -34.88) * mm, "end": v(28.7, -34.88) * mm});
            skLineSegment(sketch, "E304", {"start": v(28.5, -35.63) * mm, "end": v(28.5, -36.38) * mm});
            skLineSegment(sketch, "E305", {"start": v(28.5, -36.38) * mm, "end": v(28.7, -36.38) * mm});
            skLineSegment(sketch, "E306", {"start": v(25.7, -38.43) * mm, "end": v(26.44, -38.43) * mm});
            skLineSegment(sketch, "E307", {"start": v(26.44, -38.43) * mm, "end": v(26.44, -38.62) * mm});
            skLineSegment(sketch, "E308", {"start": v(25.7, -38.43) * mm, "end": v(24.94, -38.43) * mm});
            skLineSegment(sketch, "E309", {"start": v(24.94, -38.43) * mm, "end": v(24.94, -38.62) * mm});
            skLineSegment(sketch, "E310", {"start": v(28.7, -19.62) * mm, "end": v(28.7, -20.88) * mm});
            skLineSegment(sketch, "E311", {"start": v(28.7, -22.38) * mm, "end": v(28.7, -26.48) * mm});
            skLineSegment(sketch, "E312", {"start": v(27.7, -38.62) * mm, "end": v(26.44, -38.62) * mm});
            skLineSegment(sketch, "E313", {"start": v(28.7, -37.62) * mm, "end": v(28.7, -36.38) * mm});
            skLineSegment(sketch, "E314", {"start": v(28.7, -34.88) * mm, "end": v(28.7, -30.77) * mm});
            skLineSegment(sketch, "E315", {"start": v(18.7, -13.92) * mm, "end": v(18.7, -42.92) * mm});
            skLineSegment(sketch, "E316", {"start": v(20.84, -18.62) * mm, "end": v(20.84, -20.12) * mm});
            skLineSegment(sketch, "E317", {"start": v(22.84, -20.12) * mm, "end": v(22.84, -24.12) * mm});
            skLineSegment(sketch, "E318", {"start": v(22.84, -20.12) * mm, "end": v(20.84, -20.12) * mm});
            skLineSegment(sketch, "E319", {"start": v(16.54, -18.62) * mm, "end": v(16.54, -20.12) * mm});
            skLineSegment(sketch, "E320", {"start": v(14.54, -20.12) * mm, "end": v(14.54, -24.12) * mm});
            skLineSegment(sketch, "E321", {"start": v(14.54, -20.12) * mm, "end": v(16.54, -20.12) * mm});
            skLineSegment(sketch, "E322", {"start": v(14.54, -24.12) * mm, "end": v(16.2, -24.12) * mm});
            skLineSegment(sketch, "E323", {"start": v(16.2, -24.12) * mm, "end": v(16.2, -25.42) * mm});
            skLineSegment(sketch, "E324", {"start": v(22.84, -24.12) * mm, "end": v(16.2, -25.42) * mm});
            skLineSegment(sketch, "E325", {"start": v(16.54, -38.62) * mm, "end": v(16.54, -37.12) * mm});
            skLineSegment(sketch, "E326", {"start": v(14.54, -37.12) * mm, "end": v(14.54, -33.12) * mm});
            skLineSegment(sketch, "E327", {"start": v(14.54, -37.12) * mm, "end": v(16.54, -37.12) * mm});
            skLineSegment(sketch, "E328", {"start": v(20.84, -38.62) * mm, "end": v(20.84, -37.12) * mm});
            skLineSegment(sketch, "E329", {"start": v(22.84, -37.12) * mm, "end": v(22.84, -33.12) * mm});
            skLineSegment(sketch, "E330", {"start": v(22.84, -37.12) * mm, "end": v(20.84, -37.12) * mm});
            skLineSegment(sketch, "E331", {"start": v(22.84, -33.12) * mm, "end": v(21.2, -33.12) * mm});
            skLineSegment(sketch, "E332", {"start": v(21.2, -33.12) * mm, "end": v(21.2, -31.83) * mm});
            skLineSegment(sketch, "E333", {"start": v(14.54, -33.12) * mm, "end": v(21.2, -31.83) * mm});
            skLineSegment(sketch, "E334", {"start": v(24.94, -18.62) * mm, "end": v(20.84, -18.62) * mm});
            skLineSegment(sketch, "E335", {"start": v(24.94, -38.62) * mm, "end": v(20.84, -38.62) * mm});
            skLineSegment(sketch, "E336", {"start": v(6.1, -28.62) * mm, "end": v(31.6, -28.62) * mm});
            skLineSegment(sketch, "E337", {"start": v(11.7, -17.22) * mm, "end": v(11.7, -25.12) * mm});
            skLineSegment(sketch, "E338", {"start": v(15.3, -21.63) * mm, "end": v(6.5, -21.63) * mm});
            skLineSegment(sketch, "E339", {"start": v(10.04, -20.94) * mm, "end": v(11, -19.97) * mm});
            skLineSegment(sketch, "E340", {"start": v(11, -19.97) * mm, "end": v(12.38, -19.97) * mm});
            skLineSegment(sketch, "E341", {"start": v(12.38, -19.97) * mm, "end": v(13.34, -20.94) * mm});
            skLineSegment(sketch, "E342", {"start": v(13.34, -20.94) * mm, "end": v(13.34, -22.3) * mm});
            skLineSegment(sketch, "E343", {"start": v(13.34, -22.3) * mm, "end": v(12.38, -23.28) * mm});
            skLineSegment(sketch, "E344", {"start": v(12.38, -23.28) * mm, "end": v(11, -23.28) * mm});
            skLineSegment(sketch, "E345", {"start": v(11, -23.28) * mm, "end": v(10.04, -22.3) * mm});
            skLineSegment(sketch, "E346", {"start": v(10.04, -22.3) * mm, "end": v(10.04, -20.94) * mm});
            skLineSegment(sketch, "E347", {"start": v(9.7, -18.62) * mm, "end": v(8.7, -19.62) * mm});
            skLineSegment(sketch, "E348", {"start": v(11.7, -18.83) * mm, "end": v(10.94, -18.83) * mm});
            skLineSegment(sketch, "E349", {"start": v(10.94, -18.83) * mm, "end": v(10.94, -18.62) * mm});
            skLineSegment(sketch, "E350", {"start": v(11.7, -18.83) * mm, "end": v(12.44, -18.83) * mm});
            skLineSegment(sketch, "E351", {"start": v(12.44, -18.83) * mm, "end": v(12.44, -18.62) * mm});
            skLineSegment(sketch, "E352", {"start": v(9.7, -18.62) * mm, "end": v(10.94, -18.62) * mm});
            skLineSegment(sketch, "E353", {"start": v(8.9, -21.63) * mm, "end": v(8.9, -22.38) * mm});
            skLineSegment(sketch, "E354", {"start": v(8.9, -22.38) * mm, "end": v(8.7, -22.38) * mm});
            skLineSegment(sketch, "E355", {"start": v(8.9, -21.63) * mm, "end": v(8.9, -20.88) * mm});
            skLineSegment(sketch, "E356", {"start": v(8.9, -20.88) * mm, "end": v(8.7, -20.88) * mm});
            skLineSegment(sketch, "E357", {"start": v(8.7, -19.62) * mm, "end": v(8.7, -20.88) * mm});
            skLineSegment(sketch, "E358", {"start": v(8.7, -22.38) * mm, "end": v(8.7, -26.48) * mm});
            skLineSegment(sketch, "E359", {"start": v(12.44, -18.62) * mm, "end": v(16.54, -18.62) * mm});
            skLineSegment(sketch, "E360", {"start": v(11.7, -40.02) * mm, "end": v(11.7, -32.12) * mm});
            skLineSegment(sketch, "E361", {"start": v(15.3, -35.63) * mm, "end": v(6.5, -35.63) * mm});
            skLineSegment(sketch, "E362", {"start": v(10.04, -34.94) * mm, "end": v(11, -33.98) * mm});
            skLineSegment(sketch, "E363", {"start": v(11, -33.98) * mm, "end": v(12.38, -33.98) * mm});
            skLineSegment(sketch, "E364", {"start": v(12.38, -33.98) * mm, "end": v(13.34, -34.94) * mm});
            skLineSegment(sketch, "E365", {"start": v(13.34, -34.94) * mm, "end": v(13.34, -36.3) * mm});
            skLineSegment(sketch, "E366", {"start": v(13.34, -36.3) * mm, "end": v(12.38, -37.28) * mm});
            skLineSegment(sketch, "E367", {"start": v(12.38, -37.28) * mm, "end": v(11, -37.28) * mm});
            skLineSegment(sketch, "E368", {"start": v(11, -37.28) * mm, "end": v(10.04, -36.3) * mm});
            skLineSegment(sketch, "E369", {"start": v(10.04, -36.3) * mm, "end": v(10.04, -34.94) * mm});
            skLineSegment(sketch, "E370", {"start": v(8.7, -37.62) * mm, "end": v(9.7, -38.62) * mm});
            skLineSegment(sketch, "E371", {"start": v(8.9, -35.63) * mm, "end": v(8.9, -34.88) * mm});
            skLineSegment(sketch, "E372", {"start": v(8.9, -34.88) * mm, "end": v(8.7, -34.88) * mm});
            skLineSegment(sketch, "E373", {"start": v(8.9, -35.63) * mm, "end": v(8.9, -36.38) * mm});
            skLineSegment(sketch, "E374", {"start": v(8.9, -36.38) * mm, "end": v(8.7, -36.38) * mm});
            skLineSegment(sketch, "E375", {"start": v(11.7, -38.43) * mm, "end": v(10.94, -38.43) * mm});
            skLineSegment(sketch, "E376", {"start": v(10.94, -38.43) * mm, "end": v(10.94, -38.62) * mm});
            skLineSegment(sketch, "E377", {"start": v(11.7, -38.43) * mm, "end": v(12.44, -38.43) * mm});
            skLineSegment(sketch, "E378", {"start": v(12.44, -38.43) * mm, "end": v(12.44, -38.62) * mm});
            skLineSegment(sketch, "E379", {"start": v(9.7, -38.62) * mm, "end": v(10.94, -38.62) * mm});
            skLineSegment(sketch, "E380", {"start": v(8.7, -37.62) * mm, "end": v(8.7, -36.38) * mm});
            skLineSegment(sketch, "E381", {"start": v(8.7, -34.88) * mm, "end": v(8.7, -30.77) * mm});
            skLineSegment(sketch, "E382", {"start": v(12.44, -38.62) * mm, "end": v(16.54, -38.62) * mm});
            skLineSegment(sketch, "E383", {"start": v(8.7, -26.48) * mm, "end": v(10.2, -26.48) * mm});
            skLineSegment(sketch, "E384", {"start": v(10.2, -24.48) * mm, "end": v(14.2, -24.48) * mm});
            skLineSegment(sketch, "E385", {"start": v(10.2, -24.48) * mm, "end": v(10.2, -26.48) * mm});
            skLineSegment(sketch, "E386", {"start": v(8.7, -30.77) * mm, "end": v(10.2, -30.77) * mm});
            skLineSegment(sketch, "E387", {"start": v(10.2, -32.77) * mm, "end": v(14.2, -32.77) * mm});
            skLineSegment(sketch, "E388", {"start": v(10.2, -32.77) * mm, "end": v(10.2, -30.77) * mm});
            skLineSegment(sketch, "E389", {"start": v(14.2, -32.77) * mm, "end": v(14.2, -31.12) * mm});
            skLineSegment(sketch, "E390", {"start": v(14.2, -31.12) * mm, "end": v(15.5, -31.12) * mm});
            skLineSegment(sketch, "E391", {"start": v(14.2, -24.48) * mm, "end": v(15.5, -31.12) * mm});
            skCircle(sketch, "E392", {"center": v(18.7, -28.62) * mm, "radius": 1.6 * mm});
            skSolve(sketch);
        }
        {
            var Q0;
            {var subQ21=sQuery(id+"F9.wireOp",EDGE,"E272");Q0=makeQuery(id+"F9.imprint","IMPRINT",FACE,{"disambiguationData":[TD([[makeQuery(id+"F9.imprint","IMPRINT",EDGE,{"derivedFrom":subQ21}),-1.0]])]});}
            var Q1;
            {var subQ9=sQuery(id+"F9.wireOp",EDGE,"E285");Q1=makeQuery(id+"F9.imprint","IMPRINT",FACE,{"disambiguationData":[TD([[makeQuery(id+"F9.imprint","IMPRINT",EDGE,{"derivedFrom":subQ9}),-1.0]])]});}
            var Q2;
            {var subQ21=sQuery(id+"F9.wireOp",EDGE,"E322");Q2=makeQuery(id+"F9.imprint","IMPRINT",FACE,{"disambiguationData":[TD([[makeQuery(id+"F9.imprint","IMPRINT",EDGE,{"derivedFrom":subQ21}),-1.0]])]});}
            var Q3;
            {var subQ1=sQuery(id+"F9.wireOp",EDGE,"E364");Q3=makeQuery(id+"F9.imprint","IMPRINT",FACE,{"disambiguationData":[TD([[makeQuery(id+"F9.imprint","IMPRINT",EDGE,{"derivedFrom":subQ1}),1.0]])]});}
            var Q4;
            {var subQ0=sQuery(id+"F9.wireOp",EDGE,"E336");var subQ1=sQuery(id+"F9.wireOp",EDGE,"E315");var subQ2=makeQuery(id+"F9.imprint","INTERSECT",VERTEX,{"derivedFrom":[subQ1,subQ0]});Q4=makeQuery(id+"F9.imprint","IMPRINT",FACE,{"disambiguationData":[TD([[makeQuery(id+"F9.imprint","IMPRINT",EDGE,{"disambiguationData":[TD([[subQ2,-1.0]])],"derivedFrom":subQ1}),-1.0]])]});}
            var Q5;
            {var subQ0=sQuery(id+"F9.wireOp",EDGE,"E336");var subQ1=sQuery(id+"F9.wireOp",EDGE,"E315");var subQ2=makeQuery(id+"F9.imprint","INTERSECT",VERTEX,{"derivedFrom":[subQ1,subQ0]});Q5=makeQuery(id+"F9.imprint","IMPRINT",FACE,{"disambiguationData":[TD([[makeQuery(id+"F9.imprint","IMPRINT",EDGE,{"disambiguationData":[TD([[subQ2,-1.0]])],"derivedFrom":subQ1}),1.0]])]});}
            var Q6;
            {var subQ0=sQuery(id+"F9.wireOp",EDGE,"E392");var subQ1=sQuery(id+"F9.wireOp",EDGE,"E315");var subQ2=makeQuery(id+"F9.imprint","INTERSECT",VERTEX,{"disambiguationData":[OD(0.0)],"derivedFrom":[subQ1,subQ0]});Q6=makeQuery(id+"F9.imprint","IMPRINT",FACE,{"disambiguationData":[TD([[makeQuery(id+"F9.imprint","IMPRINT",EDGE,{"disambiguationData":[TD([[subQ2,-1.0]])],"derivedFrom":subQ1}),1.0]])]});}
            var Q7;
            {var subQ0=sQuery(id+"F9.wireOp",EDGE,"E392");var subQ1=sQuery(id+"F9.wireOp",EDGE,"E315");var subQ2=makeQuery(id+"F9.imprint","INTERSECT",VERTEX,{"disambiguationData":[OD(0.0)],"derivedFrom":[subQ1,subQ0]});Q7=makeQuery(id+"F9.imprint","IMPRINT",FACE,{"disambiguationData":[TD([[makeQuery(id+"F9.imprint","IMPRINT",EDGE,{"disambiguationData":[TD([[subQ2,-1.0]])],"derivedFrom":subQ1}),-1.0]])]});}
            var Q8;
            {var subQ5=sQuery(id+"F9.wireOp",EDGE,"E287");Q8=makeQuery(id+"F9.imprint","IMPRINT",FACE,{"disambiguationData":[TD([[makeQuery(id+"F9.imprint","IMPRINT",EDGE,{"derivedFrom":subQ5}),-1.0]])]});}
            var Q9;
            {var subQ8=sQuery(id+"F9.wireOp",EDGE,"E362");Q9=makeQuery(id+"F9.imprint","IMPRINT",FACE,{"disambiguationData":[TD([[makeQuery(id+"F9.imprint","IMPRINT",EDGE,{"derivedFrom":subQ8}),1.0]])]});}
            var Q10;
            {var subQ0=sQuery(id+"F9.wireOp",EDGE,"E364");Q10=makeQuery(id+"F9.imprint","IMPRINT",FACE,{"disambiguationData":[TD([[makeQuery(id+"F9.imprint","IMPRINT",EDGE,{"derivedFrom":subQ0}),-1.0]])]});}
            var Q11;
            Q11=makeQuery(id+"F9.imprint","IMPRINT",FACE,{"disambiguationData":[TD([[makeQuery(id+"F9.imprint","IMPRINT",EDGE,{"derivedFrom":sQuery(id+"F9.wireOp",EDGE,"E319")}),-1.0]])]});
            var Q12;
            Q12=makeQuery(id+"F9.imprint","IMPRINT",FACE,{"disambiguationData":[TD([[makeQuery(id+"F9.imprint","IMPRINT",EDGE,{"derivedFrom":sQuery(id+"F9.wireOp",EDGE,"E325")}),1.0]])]});
            var Q13;
            {var subQ1=sQuery(id+"F9.wireOp",EDGE,"E275");Q13=makeQuery(id+"F9.imprint","IMPRINT",FACE,{"disambiguationData":[TD([[makeQuery(id+"F9.imprint","IMPRINT",EDGE,{"derivedFrom":subQ1}),1.0]])]});}
            var Q14;
            Q14=makeQuery(id+"F9.imprint","IMPRINT",FACE,{"disambiguationData":[TD([[makeQuery(id+"F9.imprint","IMPRINT",EDGE,{"derivedFrom":sQuery(id+"F9.wireOp",EDGE,"E269")}),-1.0]])]});
            var Q15;
            {var subQ8=sQuery(id+"F9.wireOp",EDGE,"E345");Q15=makeQuery(id+"F9.imprint","IMPRINT",FACE,{"disambiguationData":[TD([[makeQuery(id+"F9.imprint","IMPRINT",EDGE,{"derivedFrom":subQ8}),1.0]])]});}
            var Q16;
            {var subQ0=sQuery(id+"F9.wireOp",EDGE,"E366");Q16=makeQuery(id+"F9.imprint","IMPRINT",FACE,{"disambiguationData":[TD([[makeQuery(id+"F9.imprint","IMPRINT",EDGE,{"derivedFrom":subQ0}),-1.0]])]});}
            var Q17;
            {var subQ8=sQuery(id+"F9.wireOp",EDGE,"E339");Q17=makeQuery(id+"F9.imprint","IMPRINT",FACE,{"disambiguationData":[TD([[makeQuery(id+"F9.imprint","IMPRINT",EDGE,{"derivedFrom":subQ8}),1.0]])]});}
            var Q18;
            {var subQ1=sQuery(id+"F9.wireOp",EDGE,"E339");Q18=makeQuery(id+"F9.imprint","IMPRINT",FACE,{"disambiguationData":[TD([[makeQuery(id+"F9.imprint","IMPRINT",EDGE,{"derivedFrom":subQ1}),-1.0]])]});}
            var Q19;
            Q19=makeQuery(id+"F9.imprint","IMPRINT",FACE,{"disambiguationData":[TD([[makeQuery(id+"F9.imprint","IMPRINT",EDGE,{"derivedFrom":sQuery(id+"F9.wireOp",EDGE,"E266")}),1.0]])]});
            var Q20;
            {var subQ3=sQuery(id+"F9.wireOp",EDGE,"E277");Q20=makeQuery(id+"F9.imprint","IMPRINT",FACE,{"disambiguationData":[TD([[makeQuery(id+"F9.imprint","IMPRINT",EDGE,{"derivedFrom":subQ3}),-1.0]])]});}
            var Q21;
            {var subQ0=sQuery(id+"F9.wireOp",EDGE,"E343");Q21=makeQuery(id+"F9.imprint","IMPRINT",FACE,{"disambiguationData":[TD([[makeQuery(id+"F9.imprint","IMPRINT",EDGE,{"derivedFrom":subQ0}),-1.0]])]});}
            var Q22;
            {var subQ0=sQuery(id+"F9.wireOp",EDGE,"E279");Q22=makeQuery(id+"F9.imprint","IMPRINT",FACE,{"disambiguationData":[TD([[makeQuery(id+"F9.imprint","IMPRINT",EDGE,{"derivedFrom":subQ0}),1.0]])]});}
            var Q23;
            {var subQ0=sQuery(id+"F9.wireOp",EDGE,"E281");Q23=makeQuery(id+"F9.imprint","IMPRINT",FACE,{"disambiguationData":[TD([[makeQuery(id+"F9.imprint","IMPRINT",EDGE,{"derivedFrom":subQ0}),1.0]])]});}
            var Q24;
            {var subQ3=sQuery(id+"F9.wireOp",EDGE,"E289");Q24=makeQuery(id+"F9.imprint","IMPRINT",FACE,{"disambiguationData":[TD([[makeQuery(id+"F9.imprint","IMPRINT",EDGE,{"derivedFrom":subQ3}),-1.0]])]});}
            var Q25;
            {var subQ0=sQuery(id+"F9.wireOp",EDGE,"E287");Q25=makeQuery(id+"F9.imprint","IMPRINT",FACE,{"disambiguationData":[TD([[makeQuery(id+"F9.imprint","IMPRINT",EDGE,{"derivedFrom":subQ0}),1.0]])]});}
            var Q26;
            {var subQ0=sQuery(id+"F9.wireOp",EDGE,"E285");Q26=makeQuery(id+"F9.imprint","IMPRINT",FACE,{"disambiguationData":[TD([[makeQuery(id+"F9.imprint","IMPRINT",EDGE,{"derivedFrom":subQ0}),1.0]])]});}
            var Q27;
            {var subQ0=sQuery(id+"F9.wireOp",EDGE,"E345");Q27=makeQuery(id+"F9.imprint","IMPRINT",FACE,{"disambiguationData":[TD([[makeQuery(id+"F9.imprint","IMPRINT",EDGE,{"derivedFrom":subQ0}),-1.0]])]});}
            var Q28;
            {var subQ1=sQuery(id+"F9.wireOp",EDGE,"E362");Q28=makeQuery(id+"F9.imprint","IMPRINT",FACE,{"disambiguationData":[TD([[makeQuery(id+"F9.imprint","IMPRINT",EDGE,{"derivedFrom":subQ1}),-1.0]])]});}
            var Q29;
            {var subQ0=sQuery(id+"F9.wireOp",EDGE,"E341");Q29=makeQuery(id+"F9.imprint","IMPRINT",FACE,{"disambiguationData":[TD([[makeQuery(id+"F9.imprint","IMPRINT",EDGE,{"derivedFrom":subQ0}),-1.0]])]});}
            var Q30;
            {var subQ2=sQuery(id+"F9.wireOp",EDGE,"E275");Q30=makeQuery(id+"F9.imprint","IMPRINT",FACE,{"disambiguationData":[TD([[makeQuery(id+"F9.imprint","IMPRINT",EDGE,{"derivedFrom":subQ2}),-1.0]])]});}
            var Q31;
            {var subQ0=sQuery(id+"F9.wireOp",EDGE,"E277");Q31=makeQuery(id+"F9.imprint","IMPRINT",FACE,{"disambiguationData":[TD([[makeQuery(id+"F9.imprint","IMPRINT",EDGE,{"derivedFrom":subQ0}),1.0]])]});}
            var Q32;
            {var subQ0=sQuery(id+"F9.wireOp",EDGE,"E289");Q32=makeQuery(id+"F9.imprint","IMPRINT",FACE,{"disambiguationData":[TD([[makeQuery(id+"F9.imprint","IMPRINT",EDGE,{"derivedFrom":subQ0}),1.0]])]});}
            var Q33;
            {var subQ1=sQuery(id+"F9.wireOp",EDGE,"E283");Q33=makeQuery(id+"F9.imprint","IMPRINT",FACE,{"disambiguationData":[TD([[makeQuery(id+"F9.imprint","IMPRINT",EDGE,{"derivedFrom":subQ1}),1.0]])]});}
            var Q34;
            {var subQ6=sQuery(id+"F9.wireOp",EDGE,"E368");Q34=makeQuery(id+"F9.imprint","IMPRINT",FACE,{"disambiguationData":[TD([[makeQuery(id+"F9.imprint","IMPRINT",EDGE,{"derivedFrom":subQ6}),1.0]])]});}
            var Q35;
            {var subQ0=sQuery(id+"F9.wireOp",EDGE,"E368");Q35=makeQuery(id+"F9.imprint","IMPRINT",FACE,{"disambiguationData":[TD([[makeQuery(id+"F9.imprint","IMPRINT",EDGE,{"derivedFrom":subQ0}),-1.0]])]});}
            extrude(context, id + "F10", {"entities" : qUnion([Q0, Q1, Q2, Q3, Q4, Q5, Q6, Q7, Q8, Q9, Q10, Q11, Q12, Q13, Q14, Q15, Q16, Q17, Q18, Q19, Q20, Q21, Q22, Q23, Q24, Q25, Q26, Q27, Q28, Q29, Q30, Q31, Q32, Q33, Q34, Q35]), "depth" : 20 * mm, "offsetDistance" : 25 * mm, "hasSecondDirection" : true, "secondDirectionOppositeDirection" : true, "secondDirectionDepth" : 750 * mm});
        }
        {
            var Q0;
            Q0=makeQuery(id+"F10.opExtrude","SWEPT_BODY",BODY,{"disambiguationData":[OSD([sQuery(id+"F9.wireOp",EDGE,"E266"),sQuery(id+"F9.wireOp",EDGE,"E267"),sQuery(id+"F9.wireOp",EDGE,"E268"),sQuery(id+"F9.wireOp",EDGE,"E269"),sQuery(id+"F9.wireOp",EDGE,"E270"),sQuery(id+"F9.wireOp",EDGE,"E271"),sQuery(id+"F9.wireOp",EDGE,"E272"),sQuery(id+"F9.wireOp",EDGE,"E273"),sQuery(id+"F9.wireOp",EDGE,"E274"),sQuery(id+"F9.wireOp",EDGE,"E291"),sQuery(id+"F9.wireOp",EDGE,"E292"),sQuery(id+"F9.wireOp",EDGE,"E293"),sQuery(id+"F9.wireOp",EDGE,"E294"),sQuery(id+"F9.wireOp",EDGE,"E295"),sQuery(id+"F9.wireOp",EDGE,"E296"),sQuery(id+"F9.wireOp",EDGE,"E297"),sQuery(id+"F9.wireOp",EDGE,"E298"),sQuery(id+"F9.wireOp",EDGE,"E299"),sQuery(id+"F9.wireOp",EDGE,"E300"),sQuery(id+"F9.wireOp",EDGE,"E301"),sQuery(id+"F9.wireOp",EDGE,"E302"),sQuery(id+"F9.wireOp",EDGE,"E303"),sQuery(id+"F9.wireOp",EDGE,"E304"),sQuery(id+"F9.wireOp",EDGE,"E305"),sQuery(id+"F9.wireOp",EDGE,"E306"),sQuery(id+"F9.wireOp",EDGE,"E307"),sQuery(id+"F9.wireOp",EDGE,"E308"),sQuery(id+"F9.wireOp",EDGE,"E309"),sQuery(id+"F9.wireOp",EDGE,"E310"),sQuery(id+"F9.wireOp",EDGE,"E311"),sQuery(id+"F9.wireOp",EDGE,"E312"),sQuery(id+"F9.wireOp",EDGE,"E313"),sQuery(id+"F9.wireOp",EDGE,"E314"),sQuery(id+"F9.wireOp",EDGE,"E316"),sQuery(id+"F9.wireOp",EDGE,"E317"),sQuery(id+"F9.wireOp",EDGE,"E318"),sQuery(id+"F9.wireOp",EDGE,"E319"),sQuery(id+"F9.wireOp",EDGE,"E320"),sQuery(id+"F9.wireOp",EDGE,"E321"),sQuery(id+"F9.wireOp",EDGE,"E322"),sQuery(id+"F9.wireOp",EDGE,"E323"),sQuery(id+"F9.wireOp",EDGE,"E324"),sQuery(id+"F9.wireOp",EDGE,"E325"),sQuery(id+"F9.wireOp",EDGE,"E326"),sQuery(id+"F9.wireOp",EDGE,"E327"),sQuery(id+"F9.wireOp",EDGE,"E328"),sQuery(id+"F9.wireOp",EDGE,"E329"),sQuery(id+"F9.wireOp",EDGE,"E330"),sQuery(id+"F9.wireOp",EDGE,"E331"),sQuery(id+"F9.wireOp",EDGE,"E332"),sQuery(id+"F9.wireOp",EDGE,"E333"),sQuery(id+"F9.wireOp",EDGE,"E334"),sQuery(id+"F9.wireOp",EDGE,"E335"),sQuery(id+"F9.wireOp",EDGE,"E347"),sQuery(id+"F9.wireOp",EDGE,"E348"),sQuery(id+"F9.wireOp",EDGE,"E349"),sQuery(id+"F9.wireOp",EDGE,"E350"),sQuery(id+"F9.wireOp",EDGE,"E351"),sQuery(id+"F9.wireOp",EDGE,"E352"),sQuery(id+"F9.wireOp",EDGE,"E353"),sQuery(id+"F9.wireOp",EDGE,"E354"),sQuery(id+"F9.wireOp",EDGE,"E355"),sQuery(id+"F9.wireOp",EDGE,"E356"),sQuery(id+"F9.wireOp",EDGE,"E357"),sQuery(id+"F9.wireOp",EDGE,"E358"),sQuery(id+"F9.wireOp",EDGE,"E359"),sQuery(id+"F9.wireOp",EDGE,"E370"),sQuery(id+"F9.wireOp",EDGE,"E371"),sQuery(id+"F9.wireOp",EDGE,"E372"),sQuery(id+"F9.wireOp",EDGE,"E373"),sQuery(id+"F9.wireOp",EDGE,"E374"),sQuery(id+"F9.wireOp",EDGE,"E375"),sQuery(id+"F9.wireOp",EDGE,"E376"),sQuery(id+"F9.wireOp",EDGE,"E377"),sQuery(id+"F9.wireOp",EDGE,"E378"),sQuery(id+"F9.wireOp",EDGE,"E379"),sQuery(id+"F9.wireOp",EDGE,"E380"),sQuery(id+"F9.wireOp",EDGE,"E381"),sQuery(id+"F9.wireOp",EDGE,"E382"),sQuery(id+"F9.wireOp",EDGE,"E383"),sQuery(id+"F9.wireOp",EDGE,"E384"),sQuery(id+"F9.wireOp",EDGE,"E385"),sQuery(id+"F9.wireOp",EDGE,"E386"),sQuery(id+"F9.wireOp",EDGE,"E387"),sQuery(id+"F9.wireOp",EDGE,"E388"),sQuery(id+"F9.wireOp",EDGE,"E389"),sQuery(id+"F9.wireOp",EDGE,"E390"),sQuery(id+"F9.wireOp",EDGE,"E391")])]});
            transform(context, id + "F11", {"entities" : qUnion([Q0]), "transformType" : TransformType.TRANSLATION_3D, "dx" : 0 * mm, "dy" : -47.3 * mm, "dz" : 518.6 * mm, "makeCopy" : false});
        }
        {
            var Q0;
            Q0=makeQuery(id+"F10.opExtrude","SWEPT_BODY",BODY,{"disambiguationData":[OSD([sQuery(id+"F9.wireOp",EDGE,"E266"),sQuery(id+"F9.wireOp",EDGE,"E267"),sQuery(id+"F9.wireOp",EDGE,"E268"),sQuery(id+"F9.wireOp",EDGE,"E269"),sQuery(id+"F9.wireOp",EDGE,"E270"),sQuery(id+"F9.wireOp",EDGE,"E271"),sQuery(id+"F9.wireOp",EDGE,"E272"),sQuery(id+"F9.wireOp",EDGE,"E273"),sQuery(id+"F9.wireOp",EDGE,"E274"),sQuery(id+"F9.wireOp",EDGE,"E291"),sQuery(id+"F9.wireOp",EDGE,"E292"),sQuery(id+"F9.wireOp",EDGE,"E293"),sQuery(id+"F9.wireOp",EDGE,"E294"),sQuery(id+"F9.wireOp",EDGE,"E295"),sQuery(id+"F9.wireOp",EDGE,"E296"),sQuery(id+"F9.wireOp",EDGE,"E297"),sQuery(id+"F9.wireOp",EDGE,"E298"),sQuery(id+"F9.wireOp",EDGE,"E299"),sQuery(id+"F9.wireOp",EDGE,"E300"),sQuery(id+"F9.wireOp",EDGE,"E301"),sQuery(id+"F9.wireOp",EDGE,"E302"),sQuery(id+"F9.wireOp",EDGE,"E303"),sQuery(id+"F9.wireOp",EDGE,"E304"),sQuery(id+"F9.wireOp",EDGE,"E305"),sQuery(id+"F9.wireOp",EDGE,"E306"),sQuery(id+"F9.wireOp",EDGE,"E307"),sQuery(id+"F9.wireOp",EDGE,"E308"),sQuery(id+"F9.wireOp",EDGE,"E309"),sQuery(id+"F9.wireOp",EDGE,"E310"),sQuery(id+"F9.wireOp",EDGE,"E311"),sQuery(id+"F9.wireOp",EDGE,"E312"),sQuery(id+"F9.wireOp",EDGE,"E313"),sQuery(id+"F9.wireOp",EDGE,"E314"),sQuery(id+"F9.wireOp",EDGE,"E316"),sQuery(id+"F9.wireOp",EDGE,"E317"),sQuery(id+"F9.wireOp",EDGE,"E318"),sQuery(id+"F9.wireOp",EDGE,"E319"),sQuery(id+"F9.wireOp",EDGE,"E320"),sQuery(id+"F9.wireOp",EDGE,"E321"),sQuery(id+"F9.wireOp",EDGE,"E322"),sQuery(id+"F9.wireOp",EDGE,"E323"),sQuery(id+"F9.wireOp",EDGE,"E324"),sQuery(id+"F9.wireOp",EDGE,"E325"),sQuery(id+"F9.wireOp",EDGE,"E326"),sQuery(id+"F9.wireOp",EDGE,"E327"),sQuery(id+"F9.wireOp",EDGE,"E328"),sQuery(id+"F9.wireOp",EDGE,"E329"),sQuery(id+"F9.wireOp",EDGE,"E330"),sQuery(id+"F9.wireOp",EDGE,"E331"),sQuery(id+"F9.wireOp",EDGE,"E332"),sQuery(id+"F9.wireOp",EDGE,"E333"),sQuery(id+"F9.wireOp",EDGE,"E334"),sQuery(id+"F9.wireOp",EDGE,"E335"),sQuery(id+"F9.wireOp",EDGE,"E347"),sQuery(id+"F9.wireOp",EDGE,"E348"),sQuery(id+"F9.wireOp",EDGE,"E349"),sQuery(id+"F9.wireOp",EDGE,"E350"),sQuery(id+"F9.wireOp",EDGE,"E351"),sQuery(id+"F9.wireOp",EDGE,"E352"),sQuery(id+"F9.wireOp",EDGE,"E353"),sQuery(id+"F9.wireOp",EDGE,"E354"),sQuery(id+"F9.wireOp",EDGE,"E355"),sQuery(id+"F9.wireOp",EDGE,"E356"),sQuery(id+"F9.wireOp",EDGE,"E357"),sQuery(id+"F9.wireOp",EDGE,"E358"),sQuery(id+"F9.wireOp",EDGE,"E359"),sQuery(id+"F9.wireOp",EDGE,"E370"),sQuery(id+"F9.wireOp",EDGE,"E371"),sQuery(id+"F9.wireOp",EDGE,"E372"),sQuery(id+"F9.wireOp",EDGE,"E373"),sQuery(id+"F9.wireOp",EDGE,"E374"),sQuery(id+"F9.wireOp",EDGE,"E375"),sQuery(id+"F9.wireOp",EDGE,"E376"),sQuery(id+"F9.wireOp",EDGE,"E377"),sQuery(id+"F9.wireOp",EDGE,"E378"),sQuery(id+"F9.wireOp",EDGE,"E379"),sQuery(id+"F9.wireOp",EDGE,"E380"),sQuery(id+"F9.wireOp",EDGE,"E381"),sQuery(id+"F9.wireOp",EDGE,"E382"),sQuery(id+"F9.wireOp",EDGE,"E383"),sQuery(id+"F9.wireOp",EDGE,"E384"),sQuery(id+"F9.wireOp",EDGE,"E385"),sQuery(id+"F9.wireOp",EDGE,"E386"),sQuery(id+"F9.wireOp",EDGE,"E387"),sQuery(id+"F9.wireOp",EDGE,"E388"),sQuery(id+"F9.wireOp",EDGE,"E389"),sQuery(id+"F9.wireOp",EDGE,"E390"),sQuery(id+"F9.wireOp",EDGE,"E391")])]});
            transform(context, id + "F12", {"entities" : qUnion([Q0]), "transformType" : TransformType.TRANSLATION_3D, "dx" : 0 * mm, "dy" : 650 * mm, "dz" : 0 * mm, "makeCopy" : true});
        }
        {
            var Q0;
            Q0=qCreatedBy(makeId("Front.planeOp"),FACE);
            cPlane(context, id + "F13", {"entities" : qUnion([Q0]), "cplaneType" : CPlaneType.OFFSET, "offset" : 18.6 * mm, "width" : 150 * mm, "height" : 150 * mm});
        }
        {
            var Q0;
            Q0=qCreatedBy(id+"F13.planeOp",FACE);
            var sketch = newSketch(context, id + "F14", { "sketchPlane" : qUnion([Q0])});
            skLineSegment(sketch, "E393", {"start": v(25.7, -17.22) * mm, "end": v(25.7, -25.12) * mm});
            skLineSegment(sketch, "E394", {"start": v(22.1, -21.63) * mm, "end": v(30.9, -21.63) * mm});
            skLineSegment(sketch, "E395", {"start": v(25.7, -40.02) * mm, "end": v(25.7, -32.12) * mm});
            skLineSegment(sketch, "E396", {"start": v(22.1, -35.63) * mm, "end": v(30.9, -35.63) * mm});
            skLineSegment(sketch, "E397", {"start": v(28.7, -30.77) * mm, "end": v(27.2, -30.77) * mm});
            skLineSegment(sketch, "E398", {"start": v(27.2, -32.77) * mm, "end": v(23.2, -32.77) * mm});
            skLineSegment(sketch, "E399", {"start": v(27.2, -32.77) * mm, "end": v(27.2, -30.77) * mm});
            skLineSegment(sketch, "E400", {"start": v(28.7, -26.48) * mm, "end": v(27.2, -26.48) * mm});
            skLineSegment(sketch, "E401", {"start": v(27.2, -24.48) * mm, "end": v(23.2, -24.48) * mm});
            skLineSegment(sketch, "E402", {"start": v(27.2, -24.48) * mm, "end": v(27.2, -26.48) * mm});
            skLineSegment(sketch, "E403", {"start": v(23.2, -24.48) * mm, "end": v(23.2, -26.12) * mm});
            skLineSegment(sketch, "E404", {"start": v(23.2, -26.12) * mm, "end": v(21.9, -26.12) * mm});
            skLineSegment(sketch, "E405", {"start": v(23.2, -32.77) * mm, "end": v(21.9, -26.12) * mm});
            skLineSegment(sketch, "E406", {"start": v(27.34, -20.94) * mm, "end": v(26.38, -19.97) * mm});
            skLineSegment(sketch, "E407", {"start": v(26.38, -19.97) * mm, "end": v(25, -19.97) * mm});
            skLineSegment(sketch, "E408", {"start": v(25, -19.97) * mm, "end": v(24.04, -20.94) * mm});
            skLineSegment(sketch, "E409", {"start": v(24.04, -20.94) * mm, "end": v(24.04, -22.3) * mm});
            skLineSegment(sketch, "E410", {"start": v(24.04, -22.3) * mm, "end": v(25, -23.28) * mm});
            skLineSegment(sketch, "E411", {"start": v(25, -23.28) * mm, "end": v(26.38, -23.28) * mm});
            skLineSegment(sketch, "E412", {"start": v(26.38, -23.28) * mm, "end": v(27.34, -22.3) * mm});
            skLineSegment(sketch, "E413", {"start": v(27.34, -22.3) * mm, "end": v(27.34, -20.94) * mm});
            skLineSegment(sketch, "E414", {"start": v(27.34, -34.94) * mm, "end": v(26.38, -33.98) * mm});
            skLineSegment(sketch, "E415", {"start": v(26.38, -33.98) * mm, "end": v(25, -33.98) * mm});
            skLineSegment(sketch, "E416", {"start": v(25, -33.98) * mm, "end": v(24.04, -34.94) * mm});
            skLineSegment(sketch, "E417", {"start": v(24.04, -34.94) * mm, "end": v(24.04, -36.3) * mm});
            skLineSegment(sketch, "E418", {"start": v(24.04, -36.3) * mm, "end": v(25, -37.28) * mm});
            skLineSegment(sketch, "E419", {"start": v(25, -37.28) * mm, "end": v(26.38, -37.28) * mm});
            skLineSegment(sketch, "E420", {"start": v(26.38, -37.28) * mm, "end": v(27.34, -36.3) * mm});
            skLineSegment(sketch, "E421", {"start": v(27.34, -36.3) * mm, "end": v(27.34, -34.94) * mm});
            skLineSegment(sketch, "E422", {"start": v(27.7, -18.62) * mm, "end": v(28.7, -19.62) * mm});
            skLineSegment(sketch, "E423", {"start": v(28.7, -37.62) * mm, "end": v(27.7, -38.62) * mm});
            skLineSegment(sketch, "E424", {"start": v(25.7, -18.83) * mm, "end": v(26.44, -18.83) * mm});
            skLineSegment(sketch, "E425", {"start": v(26.44, -18.83) * mm, "end": v(26.44, -18.62) * mm});
            skLineSegment(sketch, "E426", {"start": v(25.7, -18.83) * mm, "end": v(24.94, -18.83) * mm});
            skLineSegment(sketch, "E427", {"start": v(24.94, -18.83) * mm, "end": v(24.94, -18.62) * mm});
            skLineSegment(sketch, "E428", {"start": v(27.7, -18.62) * mm, "end": v(26.44, -18.62) * mm});
            skLineSegment(sketch, "E429", {"start": v(28.5, -21.63) * mm, "end": v(28.5, -22.38) * mm});
            skLineSegment(sketch, "E430", {"start": v(28.5, -22.38) * mm, "end": v(28.7, -22.38) * mm});
            skLineSegment(sketch, "E431", {"start": v(28.5, -21.63) * mm, "end": v(28.5, -20.88) * mm});
            skLineSegment(sketch, "E432", {"start": v(28.5, -20.88) * mm, "end": v(28.7, -20.88) * mm});
            skLineSegment(sketch, "E433", {"start": v(28.5, -35.63) * mm, "end": v(28.5, -34.88) * mm});
            skLineSegment(sketch, "E434", {"start": v(28.5, -34.88) * mm, "end": v(28.7, -34.88) * mm});
            skLineSegment(sketch, "E435", {"start": v(28.5, -35.63) * mm, "end": v(28.5, -36.38) * mm});
            skLineSegment(sketch, "E436", {"start": v(28.5, -36.38) * mm, "end": v(28.7, -36.38) * mm});
            skLineSegment(sketch, "E437", {"start": v(25.7, -38.43) * mm, "end": v(26.44, -38.43) * mm});
            skLineSegment(sketch, "E438", {"start": v(26.44, -38.43) * mm, "end": v(26.44, -38.62) * mm});
            skLineSegment(sketch, "E439", {"start": v(25.7, -38.43) * mm, "end": v(24.94, -38.43) * mm});
            skLineSegment(sketch, "E440", {"start": v(24.94, -38.43) * mm, "end": v(24.94, -38.62) * mm});
            skLineSegment(sketch, "E441", {"start": v(28.7, -19.62) * mm, "end": v(28.7, -20.88) * mm});
            skLineSegment(sketch, "E442", {"start": v(28.7, -22.38) * mm, "end": v(28.7, -26.48) * mm});
            skLineSegment(sketch, "E443", {"start": v(27.7, -38.62) * mm, "end": v(26.44, -38.62) * mm});
            skLineSegment(sketch, "E444", {"start": v(28.7, -37.62) * mm, "end": v(28.7, -36.38) * mm});
            skLineSegment(sketch, "E445", {"start": v(28.7, -34.88) * mm, "end": v(28.7, -30.77) * mm});
            skLineSegment(sketch, "E446", {"start": v(18.7, -13.92) * mm, "end": v(18.7, -42.92) * mm});
            skLineSegment(sketch, "E447", {"start": v(20.84, -18.62) * mm, "end": v(20.84, -20.12) * mm});
            skLineSegment(sketch, "E448", {"start": v(22.84, -20.12) * mm, "end": v(22.84, -24.12) * mm});
            skLineSegment(sketch, "E449", {"start": v(22.84, -20.12) * mm, "end": v(20.84, -20.12) * mm});
            skLineSegment(sketch, "E450", {"start": v(16.54, -18.62) * mm, "end": v(16.54, -20.12) * mm});
            skLineSegment(sketch, "E451", {"start": v(14.54, -20.12) * mm, "end": v(14.54, -24.12) * mm});
            skLineSegment(sketch, "E452", {"start": v(14.54, -20.12) * mm, "end": v(16.54, -20.12) * mm});
            skLineSegment(sketch, "E453", {"start": v(14.54, -24.12) * mm, "end": v(16.2, -24.12) * mm});
            skLineSegment(sketch, "E454", {"start": v(16.2, -24.12) * mm, "end": v(16.2, -25.42) * mm});
            skLineSegment(sketch, "E455", {"start": v(22.84, -24.12) * mm, "end": v(16.2, -25.42) * mm});
            skLineSegment(sketch, "E456", {"start": v(16.54, -38.62) * mm, "end": v(16.54, -37.12) * mm});
            skLineSegment(sketch, "E457", {"start": v(14.54, -37.12) * mm, "end": v(14.54, -33.12) * mm});
            skLineSegment(sketch, "E458", {"start": v(14.54, -37.12) * mm, "end": v(16.54, -37.12) * mm});
            skLineSegment(sketch, "E459", {"start": v(20.84, -38.62) * mm, "end": v(20.84, -37.12) * mm});
            skLineSegment(sketch, "E460", {"start": v(22.84, -37.12) * mm, "end": v(22.84, -33.12) * mm});
            skLineSegment(sketch, "E461", {"start": v(22.84, -37.12) * mm, "end": v(20.84, -37.12) * mm});
            skLineSegment(sketch, "E462", {"start": v(22.84, -33.12) * mm, "end": v(21.2, -33.12) * mm});
            skLineSegment(sketch, "E463", {"start": v(21.2, -33.12) * mm, "end": v(21.2, -31.83) * mm});
            skLineSegment(sketch, "E464", {"start": v(14.54, -33.12) * mm, "end": v(21.2, -31.83) * mm});
            skLineSegment(sketch, "E465", {"start": v(24.94, -18.62) * mm, "end": v(20.84, -18.62) * mm});
            skLineSegment(sketch, "E466", {"start": v(24.94, -38.62) * mm, "end": v(20.84, -38.62) * mm});
            skLineSegment(sketch, "E467", {"start": v(6.1, -28.62) * mm, "end": v(31.6, -28.62) * mm});
            skLineSegment(sketch, "E468", {"start": v(11.7, -17.22) * mm, "end": v(11.7, -25.12) * mm});
            skLineSegment(sketch, "E469", {"start": v(15.3, -21.63) * mm, "end": v(6.5, -21.63) * mm});
            skLineSegment(sketch, "E470", {"start": v(10.04, -20.94) * mm, "end": v(11, -19.97) * mm});
            skLineSegment(sketch, "E471", {"start": v(11, -19.97) * mm, "end": v(12.38, -19.97) * mm});
            skLineSegment(sketch, "E472", {"start": v(12.38, -19.97) * mm, "end": v(13.34, -20.94) * mm});
            skLineSegment(sketch, "E473", {"start": v(13.34, -20.94) * mm, "end": v(13.34, -22.3) * mm});
            skLineSegment(sketch, "E474", {"start": v(13.34, -22.3) * mm, "end": v(12.38, -23.28) * mm});
            skLineSegment(sketch, "E475", {"start": v(12.38, -23.28) * mm, "end": v(11, -23.28) * mm});
            skLineSegment(sketch, "E476", {"start": v(11, -23.28) * mm, "end": v(10.04, -22.3) * mm});
            skLineSegment(sketch, "E477", {"start": v(10.04, -22.3) * mm, "end": v(10.04, -20.94) * mm});
            skLineSegment(sketch, "E478", {"start": v(9.7, -18.62) * mm, "end": v(8.7, -19.62) * mm});
            skLineSegment(sketch, "E479", {"start": v(11.7, -18.83) * mm, "end": v(10.94, -18.83) * mm});
            skLineSegment(sketch, "E480", {"start": v(10.94, -18.83) * mm, "end": v(10.94, -18.62) * mm});
            skLineSegment(sketch, "E481", {"start": v(11.7, -18.83) * mm, "end": v(12.44, -18.83) * mm});
            skLineSegment(sketch, "E482", {"start": v(12.44, -18.83) * mm, "end": v(12.44, -18.62) * mm});
            skLineSegment(sketch, "E483", {"start": v(9.7, -18.62) * mm, "end": v(10.94, -18.62) * mm});
            skLineSegment(sketch, "E484", {"start": v(8.9, -21.63) * mm, "end": v(8.9, -22.38) * mm});
            skLineSegment(sketch, "E485", {"start": v(8.9, -22.38) * mm, "end": v(8.7, -22.38) * mm});
            skLineSegment(sketch, "E486", {"start": v(8.9, -21.63) * mm, "end": v(8.9, -20.88) * mm});
            skLineSegment(sketch, "E487", {"start": v(8.9, -20.88) * mm, "end": v(8.7, -20.88) * mm});
            skLineSegment(sketch, "E488", {"start": v(8.7, -19.62) * mm, "end": v(8.7, -20.88) * mm});
            skLineSegment(sketch, "E489", {"start": v(8.7, -22.38) * mm, "end": v(8.7, -26.48) * mm});
            skLineSegment(sketch, "E490", {"start": v(12.44, -18.62) * mm, "end": v(16.54, -18.62) * mm});
            skLineSegment(sketch, "E491", {"start": v(11.7, -40.02) * mm, "end": v(11.7, -32.12) * mm});
            skLineSegment(sketch, "E492", {"start": v(15.3, -35.63) * mm, "end": v(6.5, -35.63) * mm});
            skLineSegment(sketch, "E493", {"start": v(10.04, -34.94) * mm, "end": v(11, -33.98) * mm});
            skLineSegment(sketch, "E494", {"start": v(11, -33.98) * mm, "end": v(12.38, -33.98) * mm});
            skLineSegment(sketch, "E495", {"start": v(12.38, -33.98) * mm, "end": v(13.34, -34.94) * mm});
            skLineSegment(sketch, "E496", {"start": v(13.34, -34.94) * mm, "end": v(13.34, -36.3) * mm});
            skLineSegment(sketch, "E497", {"start": v(13.34, -36.3) * mm, "end": v(12.38, -37.28) * mm});
            skLineSegment(sketch, "E498", {"start": v(12.38, -37.28) * mm, "end": v(11, -37.28) * mm});
            skLineSegment(sketch, "E499", {"start": v(11, -37.28) * mm, "end": v(10.04, -36.3) * mm});
            skLineSegment(sketch, "E500", {"start": v(10.04, -36.3) * mm, "end": v(10.04, -34.94) * mm});
            skLineSegment(sketch, "E501", {"start": v(8.7, -37.62) * mm, "end": v(9.7, -38.62) * mm});
            skLineSegment(sketch, "E502", {"start": v(8.9, -35.63) * mm, "end": v(8.9, -34.88) * mm});
            skLineSegment(sketch, "E503", {"start": v(8.9, -34.88) * mm, "end": v(8.7, -34.88) * mm});
            skLineSegment(sketch, "E504", {"start": v(8.9, -35.63) * mm, "end": v(8.9, -36.38) * mm});
            skLineSegment(sketch, "E505", {"start": v(8.9, -36.38) * mm, "end": v(8.7, -36.38) * mm});
            skLineSegment(sketch, "E506", {"start": v(11.7, -38.43) * mm, "end": v(10.94, -38.43) * mm});
            skLineSegment(sketch, "E507", {"start": v(10.94, -38.43) * mm, "end": v(10.94, -38.62) * mm});
            skLineSegment(sketch, "E508", {"start": v(11.7, -38.43) * mm, "end": v(12.44, -38.43) * mm});
            skLineSegment(sketch, "E509", {"start": v(12.44, -38.43) * mm, "end": v(12.44, -38.62) * mm});
            skLineSegment(sketch, "E510", {"start": v(9.7, -38.62) * mm, "end": v(10.94, -38.62) * mm});
            skLineSegment(sketch, "E511", {"start": v(8.7, -37.62) * mm, "end": v(8.7, -36.38) * mm});
            skLineSegment(sketch, "E512", {"start": v(8.7, -34.88) * mm, "end": v(8.7, -30.77) * mm});
            skLineSegment(sketch, "E513", {"start": v(12.44, -38.62) * mm, "end": v(16.54, -38.62) * mm});
            skLineSegment(sketch, "E514", {"start": v(8.7, -26.48) * mm, "end": v(10.2, -26.48) * mm});
            skLineSegment(sketch, "E515", {"start": v(10.2, -24.48) * mm, "end": v(14.2, -24.48) * mm});
            skLineSegment(sketch, "E516", {"start": v(10.2, -24.48) * mm, "end": v(10.2, -26.48) * mm});
            skLineSegment(sketch, "E517", {"start": v(8.7, -30.77) * mm, "end": v(10.2, -30.77) * mm});
            skLineSegment(sketch, "E518", {"start": v(10.2, -32.77) * mm, "end": v(14.2, -32.77) * mm});
            skLineSegment(sketch, "E519", {"start": v(10.2, -32.77) * mm, "end": v(10.2, -30.77) * mm});
            skLineSegment(sketch, "E520", {"start": v(14.2, -32.77) * mm, "end": v(14.2, -31.12) * mm});
            skLineSegment(sketch, "E521", {"start": v(14.2, -31.12) * mm, "end": v(15.5, -31.12) * mm});
            skLineSegment(sketch, "E522", {"start": v(14.2, -24.48) * mm, "end": v(15.5, -31.12) * mm});
            skCircle(sketch, "E523", {"center": v(18.7, -28.62) * mm, "radius": 1.6 * mm});
            skSolve(sketch);
        }
        {
            var Q0;
            {var subQ21=sQuery(id+"F14.wireOp",EDGE,"E403");Q0=makeQuery(id+"F14.imprint","IMPRINT",FACE,{"disambiguationData":[TD([[makeQuery(id+"F14.imprint","IMPRINT",EDGE,{"derivedFrom":subQ21}),-1.0]])]});}
            var Q1;
            {var subQ9=sQuery(id+"F14.wireOp",EDGE,"E416");Q1=makeQuery(id+"F14.imprint","IMPRINT",FACE,{"disambiguationData":[TD([[makeQuery(id+"F14.imprint","IMPRINT",EDGE,{"derivedFrom":subQ9}),-1.0]])]});}
            var Q2;
            {var subQ21=sQuery(id+"F14.wireOp",EDGE,"E453");Q2=makeQuery(id+"F14.imprint","IMPRINT",FACE,{"disambiguationData":[TD([[makeQuery(id+"F14.imprint","IMPRINT",EDGE,{"derivedFrom":subQ21}),-1.0]])]});}
            var Q3;
            {var subQ1=sQuery(id+"F14.wireOp",EDGE,"E495");Q3=makeQuery(id+"F14.imprint","IMPRINT",FACE,{"disambiguationData":[TD([[makeQuery(id+"F14.imprint","IMPRINT",EDGE,{"derivedFrom":subQ1}),1.0]])]});}
            var Q4;
            {var subQ0=sQuery(id+"F14.wireOp",EDGE,"E523");var subQ1=sQuery(id+"F14.wireOp",EDGE,"E446");var subQ2=makeQuery(id+"F14.imprint","INTERSECT",VERTEX,{"disambiguationData":[OD(0.0)],"derivedFrom":[subQ1,subQ0]});Q4=makeQuery(id+"F14.imprint","IMPRINT",FACE,{"disambiguationData":[TD([[makeQuery(id+"F14.imprint","IMPRINT",EDGE,{"disambiguationData":[TD([[subQ2,-1.0]])],"derivedFrom":subQ1}),1.0]])]});}
            var Q5;
            {var subQ0=sQuery(id+"F14.wireOp",EDGE,"E523");var subQ1=sQuery(id+"F14.wireOp",EDGE,"E446");var subQ2=makeQuery(id+"F14.imprint","INTERSECT",VERTEX,{"disambiguationData":[OD(0.0)],"derivedFrom":[subQ1,subQ0]});Q5=makeQuery(id+"F14.imprint","IMPRINT",FACE,{"disambiguationData":[TD([[makeQuery(id+"F14.imprint","IMPRINT",EDGE,{"disambiguationData":[TD([[subQ2,-1.0]])],"derivedFrom":subQ1}),-1.0]])]});}
            var Q6;
            {var subQ0=sQuery(id+"F14.wireOp",EDGE,"E467");var subQ1=sQuery(id+"F14.wireOp",EDGE,"E446");var subQ2=makeQuery(id+"F14.imprint","INTERSECT",VERTEX,{"derivedFrom":[subQ1,subQ0]});Q6=makeQuery(id+"F14.imprint","IMPRINT",FACE,{"disambiguationData":[TD([[makeQuery(id+"F14.imprint","IMPRINT",EDGE,{"disambiguationData":[TD([[subQ2,-1.0]])],"derivedFrom":subQ1}),-1.0]])]});}
            var Q7;
            {var subQ0=sQuery(id+"F14.wireOp",EDGE,"E467");var subQ1=sQuery(id+"F14.wireOp",EDGE,"E446");var subQ2=makeQuery(id+"F14.imprint","INTERSECT",VERTEX,{"derivedFrom":[subQ1,subQ0]});Q7=makeQuery(id+"F14.imprint","IMPRINT",FACE,{"disambiguationData":[TD([[makeQuery(id+"F14.imprint","IMPRINT",EDGE,{"disambiguationData":[TD([[subQ2,-1.0]])],"derivedFrom":subQ1}),1.0]])]});}
            var Q8;
            Q8=makeQuery(id+"F14.imprint","IMPRINT",FACE,{"disambiguationData":[TD([[makeQuery(id+"F14.imprint","IMPRINT",EDGE,{"derivedFrom":sQuery(id+"F14.wireOp",EDGE,"E397")}),1.0]])]});
            var Q9;
            {var subQ3=sQuery(id+"F14.wireOp",EDGE,"E408");Q9=makeQuery(id+"F14.imprint","IMPRINT",FACE,{"disambiguationData":[TD([[makeQuery(id+"F14.imprint","IMPRINT",EDGE,{"derivedFrom":subQ3}),-1.0]])]});}
            var Q10;
            Q10=makeQuery(id+"F14.imprint","IMPRINT",FACE,{"disambiguationData":[TD([[makeQuery(id+"F14.imprint","IMPRINT",EDGE,{"derivedFrom":sQuery(id+"F14.wireOp",EDGE,"E400")}),-1.0]])]});
            var Q11;
            {var subQ5=sQuery(id+"F14.wireOp",EDGE,"E418");Q11=makeQuery(id+"F14.imprint","IMPRINT",FACE,{"disambiguationData":[TD([[makeQuery(id+"F14.imprint","IMPRINT",EDGE,{"derivedFrom":subQ5}),-1.0]])]});}
            var Q12;
            {var subQ0=sQuery(id+"F14.wireOp",EDGE,"E416");Q12=makeQuery(id+"F14.imprint","IMPRINT",FACE,{"disambiguationData":[TD([[makeQuery(id+"F14.imprint","IMPRINT",EDGE,{"derivedFrom":subQ0}),1.0]])]});}
            var Q13;
            Q13=makeQuery(id+"F14.imprint","IMPRINT",FACE,{"disambiguationData":[TD([[makeQuery(id+"F14.imprint","IMPRINT",EDGE,{"derivedFrom":sQuery(id+"F14.wireOp",EDGE,"E450")}),-1.0]])]});
            var Q14;
            Q14=makeQuery(id+"F14.imprint","IMPRINT",FACE,{"disambiguationData":[TD([[makeQuery(id+"F14.imprint","IMPRINT",EDGE,{"derivedFrom":sQuery(id+"F14.wireOp",EDGE,"E456")}),1.0]])]});
            var Q15;
            {var subQ8=sQuery(id+"F14.wireOp",EDGE,"E476");Q15=makeQuery(id+"F14.imprint","IMPRINT",FACE,{"disambiguationData":[TD([[makeQuery(id+"F14.imprint","IMPRINT",EDGE,{"derivedFrom":subQ8}),1.0]])]});}
            var Q16;
            {var subQ8=sQuery(id+"F14.wireOp",EDGE,"E493");Q16=makeQuery(id+"F14.imprint","IMPRINT",FACE,{"disambiguationData":[TD([[makeQuery(id+"F14.imprint","IMPRINT",EDGE,{"derivedFrom":subQ8}),1.0]])]});}
            var Q17;
            {var subQ0=sQuery(id+"F14.wireOp",EDGE,"E497");Q17=makeQuery(id+"F14.imprint","IMPRINT",FACE,{"disambiguationData":[TD([[makeQuery(id+"F14.imprint","IMPRINT",EDGE,{"derivedFrom":subQ0}),-1.0]])]});}
            var Q18;
            {var subQ0=sQuery(id+"F14.wireOp",EDGE,"E408");Q18=makeQuery(id+"F14.imprint","IMPRINT",FACE,{"disambiguationData":[TD([[makeQuery(id+"F14.imprint","IMPRINT",EDGE,{"derivedFrom":subQ0}),1.0]])]});}
            var Q19;
            {var subQ0=sQuery(id+"F14.wireOp",EDGE,"E418");Q19=makeQuery(id+"F14.imprint","IMPRINT",FACE,{"disambiguationData":[TD([[makeQuery(id+"F14.imprint","IMPRINT",EDGE,{"derivedFrom":subQ0}),1.0]])]});}
            var Q20;
            {var subQ1=sQuery(id+"F14.wireOp",EDGE,"E414");Q20=makeQuery(id+"F14.imprint","IMPRINT",FACE,{"disambiguationData":[TD([[makeQuery(id+"F14.imprint","IMPRINT",EDGE,{"derivedFrom":subQ1}),1.0]])]});}
            var Q21;
            {var subQ8=sQuery(id+"F14.wireOp",EDGE,"E470");Q21=makeQuery(id+"F14.imprint","IMPRINT",FACE,{"disambiguationData":[TD([[makeQuery(id+"F14.imprint","IMPRINT",EDGE,{"derivedFrom":subQ8}),1.0]])]});}
            var Q22;
            {var subQ1=sQuery(id+"F14.wireOp",EDGE,"E470");Q22=makeQuery(id+"F14.imprint","IMPRINT",FACE,{"disambiguationData":[TD([[makeQuery(id+"F14.imprint","IMPRINT",EDGE,{"derivedFrom":subQ1}),-1.0]])]});}
            var Q23;
            {var subQ6=sQuery(id+"F14.wireOp",EDGE,"E499");Q23=makeQuery(id+"F14.imprint","IMPRINT",FACE,{"disambiguationData":[TD([[makeQuery(id+"F14.imprint","IMPRINT",EDGE,{"derivedFrom":subQ6}),1.0]])]});}
            var Q24;
            {var subQ0=sQuery(id+"F14.wireOp",EDGE,"E495");Q24=makeQuery(id+"F14.imprint","IMPRINT",FACE,{"disambiguationData":[TD([[makeQuery(id+"F14.imprint","IMPRINT",EDGE,{"derivedFrom":subQ0}),-1.0]])]});}
            var Q25;
            {var subQ2=sQuery(id+"F14.wireOp",EDGE,"E406");Q25=makeQuery(id+"F14.imprint","IMPRINT",FACE,{"disambiguationData":[TD([[makeQuery(id+"F14.imprint","IMPRINT",EDGE,{"derivedFrom":subQ2}),-1.0]])]});}
            var Q26;
            {var subQ1=sQuery(id+"F14.wireOp",EDGE,"E406");Q26=makeQuery(id+"F14.imprint","IMPRINT",FACE,{"disambiguationData":[TD([[makeQuery(id+"F14.imprint","IMPRINT",EDGE,{"derivedFrom":subQ1}),1.0]])]});}
            var Q27;
            {var subQ0=sQuery(id+"F14.wireOp",EDGE,"E410");Q27=makeQuery(id+"F14.imprint","IMPRINT",FACE,{"disambiguationData":[TD([[makeQuery(id+"F14.imprint","IMPRINT",EDGE,{"derivedFrom":subQ0}),1.0]])]});}
            var Q28;
            {var subQ0=sQuery(id+"F14.wireOp",EDGE,"E412");Q28=makeQuery(id+"F14.imprint","IMPRINT",FACE,{"disambiguationData":[TD([[makeQuery(id+"F14.imprint","IMPRINT",EDGE,{"derivedFrom":subQ0}),1.0]])]});}
            var Q29;
            {var subQ1=sQuery(id+"F14.wireOp",EDGE,"E493");Q29=makeQuery(id+"F14.imprint","IMPRINT",FACE,{"disambiguationData":[TD([[makeQuery(id+"F14.imprint","IMPRINT",EDGE,{"derivedFrom":subQ1}),-1.0]])]});}
            var Q30;
            {var subQ3=sQuery(id+"F14.wireOp",EDGE,"E420");Q30=makeQuery(id+"F14.imprint","IMPRINT",FACE,{"disambiguationData":[TD([[makeQuery(id+"F14.imprint","IMPRINT",EDGE,{"derivedFrom":subQ3}),-1.0]])]});}
            var Q31;
            {var subQ0=sQuery(id+"F14.wireOp",EDGE,"E420");Q31=makeQuery(id+"F14.imprint","IMPRINT",FACE,{"disambiguationData":[TD([[makeQuery(id+"F14.imprint","IMPRINT",EDGE,{"derivedFrom":subQ0}),1.0]])]});}
            var Q32;
            {var subQ0=sQuery(id+"F14.wireOp",EDGE,"E499");Q32=makeQuery(id+"F14.imprint","IMPRINT",FACE,{"disambiguationData":[TD([[makeQuery(id+"F14.imprint","IMPRINT",EDGE,{"derivedFrom":subQ0}),-1.0]])]});}
            var Q33;
            {var subQ0=sQuery(id+"F14.wireOp",EDGE,"E472");Q33=makeQuery(id+"F14.imprint","IMPRINT",FACE,{"disambiguationData":[TD([[makeQuery(id+"F14.imprint","IMPRINT",EDGE,{"derivedFrom":subQ0}),-1.0]])]});}
            var Q34;
            {var subQ0=sQuery(id+"F14.wireOp",EDGE,"E474");Q34=makeQuery(id+"F14.imprint","IMPRINT",FACE,{"disambiguationData":[TD([[makeQuery(id+"F14.imprint","IMPRINT",EDGE,{"derivedFrom":subQ0}),-1.0]])]});}
            var Q35;
            {var subQ0=sQuery(id+"F14.wireOp",EDGE,"E476");Q35=makeQuery(id+"F14.imprint","IMPRINT",FACE,{"disambiguationData":[TD([[makeQuery(id+"F14.imprint","IMPRINT",EDGE,{"derivedFrom":subQ0}),-1.0]])]});}
            extrude(context, id + "F15", {"entities" : qUnion([Q0, Q1, Q2, Q3, Q4, Q5, Q6, Q7, Q8, Q9, Q10, Q11, Q12, Q13, Q14, Q15, Q16, Q17, Q18, Q19, Q20, Q21, Q22, Q23, Q24, Q25, Q26, Q27, Q28, Q29, Q30, Q31, Q32, Q33, Q34, Q35]), "oppositeDirection" : true, "depth" : 630 * mm, "offsetDistance" : 25 * mm});
        }
        {
            var Q0;
            Q0=makeQuery(id+"F15.opExtrude","SWEPT_BODY",BODY,{"disambiguationData":[OSD([sQuery(id+"F14.wireOp",EDGE,"E397"),sQuery(id+"F14.wireOp",EDGE,"E398"),sQuery(id+"F14.wireOp",EDGE,"E399"),sQuery(id+"F14.wireOp",EDGE,"E400"),sQuery(id+"F14.wireOp",EDGE,"E401"),sQuery(id+"F14.wireOp",EDGE,"E402"),sQuery(id+"F14.wireOp",EDGE,"E403"),sQuery(id+"F14.wireOp",EDGE,"E404"),sQuery(id+"F14.wireOp",EDGE,"E405"),sQuery(id+"F14.wireOp",EDGE,"E422"),sQuery(id+"F14.wireOp",EDGE,"E423"),sQuery(id+"F14.wireOp",EDGE,"E424"),sQuery(id+"F14.wireOp",EDGE,"E425"),sQuery(id+"F14.wireOp",EDGE,"E426"),sQuery(id+"F14.wireOp",EDGE,"E427"),sQuery(id+"F14.wireOp",EDGE,"E428"),sQuery(id+"F14.wireOp",EDGE,"E429"),sQuery(id+"F14.wireOp",EDGE,"E430"),sQuery(id+"F14.wireOp",EDGE,"E431"),sQuery(id+"F14.wireOp",EDGE,"E432"),sQuery(id+"F14.wireOp",EDGE,"E433"),sQuery(id+"F14.wireOp",EDGE,"E434"),sQuery(id+"F14.wireOp",EDGE,"E435"),sQuery(id+"F14.wireOp",EDGE,"E436"),sQuery(id+"F14.wireOp",EDGE,"E437"),sQuery(id+"F14.wireOp",EDGE,"E438"),sQuery(id+"F14.wireOp",EDGE,"E439"),sQuery(id+"F14.wireOp",EDGE,"E440"),sQuery(id+"F14.wireOp",EDGE,"E441"),sQuery(id+"F14.wireOp",EDGE,"E442"),sQuery(id+"F14.wireOp",EDGE,"E443"),sQuery(id+"F14.wireOp",EDGE,"E444"),sQuery(id+"F14.wireOp",EDGE,"E445"),sQuery(id+"F14.wireOp",EDGE,"E447"),sQuery(id+"F14.wireOp",EDGE,"E448"),sQuery(id+"F14.wireOp",EDGE,"E449"),sQuery(id+"F14.wireOp",EDGE,"E450"),sQuery(id+"F14.wireOp",EDGE,"E451"),sQuery(id+"F14.wireOp",EDGE,"E452"),sQuery(id+"F14.wireOp",EDGE,"E453"),sQuery(id+"F14.wireOp",EDGE,"E454"),sQuery(id+"F14.wireOp",EDGE,"E455"),sQuery(id+"F14.wireOp",EDGE,"E456"),sQuery(id+"F14.wireOp",EDGE,"E457"),sQuery(id+"F14.wireOp",EDGE,"E458"),sQuery(id+"F14.wireOp",EDGE,"E459"),sQuery(id+"F14.wireOp",EDGE,"E460"),sQuery(id+"F14.wireOp",EDGE,"E461"),sQuery(id+"F14.wireOp",EDGE,"E462"),sQuery(id+"F14.wireOp",EDGE,"E463"),sQuery(id+"F14.wireOp",EDGE,"E464"),sQuery(id+"F14.wireOp",EDGE,"E465"),sQuery(id+"F14.wireOp",EDGE,"E466"),sQuery(id+"F14.wireOp",EDGE,"E478"),sQuery(id+"F14.wireOp",EDGE,"E479"),sQuery(id+"F14.wireOp",EDGE,"E480"),sQuery(id+"F14.wireOp",EDGE,"E481"),sQuery(id+"F14.wireOp",EDGE,"E482"),sQuery(id+"F14.wireOp",EDGE,"E483"),sQuery(id+"F14.wireOp",EDGE,"E484"),sQuery(id+"F14.wireOp",EDGE,"E485"),sQuery(id+"F14.wireOp",EDGE,"E486"),sQuery(id+"F14.wireOp",EDGE,"E487"),sQuery(id+"F14.wireOp",EDGE,"E488"),sQuery(id+"F14.wireOp",EDGE,"E489"),sQuery(id+"F14.wireOp",EDGE,"E490"),sQuery(id+"F14.wireOp",EDGE,"E501"),sQuery(id+"F14.wireOp",EDGE,"E502"),sQuery(id+"F14.wireOp",EDGE,"E503"),sQuery(id+"F14.wireOp",EDGE,"E504"),sQuery(id+"F14.wireOp",EDGE,"E505"),sQuery(id+"F14.wireOp",EDGE,"E506"),sQuery(id+"F14.wireOp",EDGE,"E507"),sQuery(id+"F14.wireOp",EDGE,"E508"),sQuery(id+"F14.wireOp",EDGE,"E509"),sQuery(id+"F14.wireOp",EDGE,"E510"),sQuery(id+"F14.wireOp",EDGE,"E511"),sQuery(id+"F14.wireOp",EDGE,"E512"),sQuery(id+"F14.wireOp",EDGE,"E513"),sQuery(id+"F14.wireOp",EDGE,"E514"),sQuery(id+"F14.wireOp",EDGE,"E515"),sQuery(id+"F14.wireOp",EDGE,"E516"),sQuery(id+"F14.wireOp",EDGE,"E517"),sQuery(id+"F14.wireOp",EDGE,"E518"),sQuery(id+"F14.wireOp",EDGE,"E519"),sQuery(id+"F14.wireOp",EDGE,"E520"),sQuery(id+"F14.wireOp",EDGE,"E521"),sQuery(id+"F14.wireOp",EDGE,"E522")])]});
            transform(context, id + "F16", {"entities" : qUnion([Q0]), "transformType" : TransformType.TRANSLATION_3D, "dx" : 0 * mm, "dy" : 0 * mm, "dz" : 38.6 * mm, "makeCopy" : false});
        }
        {
            var Q0;
            Q0=makeQuery(id+"F15.opExtrude","SWEPT_BODY",BODY,{"disambiguationData":[OSD([sQuery(id+"F14.wireOp",EDGE,"E397"),sQuery(id+"F14.wireOp",EDGE,"E398"),sQuery(id+"F14.wireOp",EDGE,"E399"),sQuery(id+"F14.wireOp",EDGE,"E400"),sQuery(id+"F14.wireOp",EDGE,"E401"),sQuery(id+"F14.wireOp",EDGE,"E402"),sQuery(id+"F14.wireOp",EDGE,"E403"),sQuery(id+"F14.wireOp",EDGE,"E404"),sQuery(id+"F14.wireOp",EDGE,"E405"),sQuery(id+"F14.wireOp",EDGE,"E422"),sQuery(id+"F14.wireOp",EDGE,"E423"),sQuery(id+"F14.wireOp",EDGE,"E424"),sQuery(id+"F14.wireOp",EDGE,"E425"),sQuery(id+"F14.wireOp",EDGE,"E426"),sQuery(id+"F14.wireOp",EDGE,"E427"),sQuery(id+"F14.wireOp",EDGE,"E428"),sQuery(id+"F14.wireOp",EDGE,"E429"),sQuery(id+"F14.wireOp",EDGE,"E430"),sQuery(id+"F14.wireOp",EDGE,"E431"),sQuery(id+"F14.wireOp",EDGE,"E432"),sQuery(id+"F14.wireOp",EDGE,"E433"),sQuery(id+"F14.wireOp",EDGE,"E434"),sQuery(id+"F14.wireOp",EDGE,"E435"),sQuery(id+"F14.wireOp",EDGE,"E436"),sQuery(id+"F14.wireOp",EDGE,"E437"),sQuery(id+"F14.wireOp",EDGE,"E438"),sQuery(id+"F14.wireOp",EDGE,"E439"),sQuery(id+"F14.wireOp",EDGE,"E440"),sQuery(id+"F14.wireOp",EDGE,"E441"),sQuery(id+"F14.wireOp",EDGE,"E442"),sQuery(id+"F14.wireOp",EDGE,"E443"),sQuery(id+"F14.wireOp",EDGE,"E444"),sQuery(id+"F14.wireOp",EDGE,"E445"),sQuery(id+"F14.wireOp",EDGE,"E447"),sQuery(id+"F14.wireOp",EDGE,"E448"),sQuery(id+"F14.wireOp",EDGE,"E449"),sQuery(id+"F14.wireOp",EDGE,"E450"),sQuery(id+"F14.wireOp",EDGE,"E451"),sQuery(id+"F14.wireOp",EDGE,"E452"),sQuery(id+"F14.wireOp",EDGE,"E453"),sQuery(id+"F14.wireOp",EDGE,"E454"),sQuery(id+"F14.wireOp",EDGE,"E455"),sQuery(id+"F14.wireOp",EDGE,"E456"),sQuery(id+"F14.wireOp",EDGE,"E457"),sQuery(id+"F14.wireOp",EDGE,"E458"),sQuery(id+"F14.wireOp",EDGE,"E459"),sQuery(id+"F14.wireOp",EDGE,"E460"),sQuery(id+"F14.wireOp",EDGE,"E461"),sQuery(id+"F14.wireOp",EDGE,"E462"),sQuery(id+"F14.wireOp",EDGE,"E463"),sQuery(id+"F14.wireOp",EDGE,"E464"),sQuery(id+"F14.wireOp",EDGE,"E465"),sQuery(id+"F14.wireOp",EDGE,"E466"),sQuery(id+"F14.wireOp",EDGE,"E478"),sQuery(id+"F14.wireOp",EDGE,"E479"),sQuery(id+"F14.wireOp",EDGE,"E480"),sQuery(id+"F14.wireOp",EDGE,"E481"),sQuery(id+"F14.wireOp",EDGE,"E482"),sQuery(id+"F14.wireOp",EDGE,"E483"),sQuery(id+"F14.wireOp",EDGE,"E484"),sQuery(id+"F14.wireOp",EDGE,"E485"),sQuery(id+"F14.wireOp",EDGE,"E486"),sQuery(id+"F14.wireOp",EDGE,"E487"),sQuery(id+"F14.wireOp",EDGE,"E488"),sQuery(id+"F14.wireOp",EDGE,"E489"),sQuery(id+"F14.wireOp",EDGE,"E490"),sQuery(id+"F14.wireOp",EDGE,"E501"),sQuery(id+"F14.wireOp",EDGE,"E502"),sQuery(id+"F14.wireOp",EDGE,"E503"),sQuery(id+"F14.wireOp",EDGE,"E504"),sQuery(id+"F14.wireOp",EDGE,"E505"),sQuery(id+"F14.wireOp",EDGE,"E506"),sQuery(id+"F14.wireOp",EDGE,"E507"),sQuery(id+"F14.wireOp",EDGE,"E508"),sQuery(id+"F14.wireOp",EDGE,"E509"),sQuery(id+"F14.wireOp",EDGE,"E510"),sQuery(id+"F14.wireOp",EDGE,"E511"),sQuery(id+"F14.wireOp",EDGE,"E512"),sQuery(id+"F14.wireOp",EDGE,"E513"),sQuery(id+"F14.wireOp",EDGE,"E514"),sQuery(id+"F14.wireOp",EDGE,"E515"),sQuery(id+"F14.wireOp",EDGE,"E516"),sQuery(id+"F14.wireOp",EDGE,"E517"),sQuery(id+"F14.wireOp",EDGE,"E518"),sQuery(id+"F14.wireOp",EDGE,"E519"),sQuery(id+"F14.wireOp",EDGE,"E520"),sQuery(id+"F14.wireOp",EDGE,"E521"),sQuery(id+"F14.wireOp",EDGE,"E522")])]});
            transform(context, id + "F17", {"entities" : qUnion([Q0]), "transformType" : TransformType.TRANSLATION_3D, "dx" : 0 * mm, "dy" : 0 * mm, "dz" : 480 * mm, "makeCopy" : true});
        }
        {
            var Q0;
            Q0=makeQuery(id+"F15.opExtrude","SWEPT_BODY",BODY,{"disambiguationData":[OSD([sQuery(id+"F14.wireOp",EDGE,"E397"),sQuery(id+"F14.wireOp",EDGE,"E398"),sQuery(id+"F14.wireOp",EDGE,"E399"),sQuery(id+"F14.wireOp",EDGE,"E400"),sQuery(id+"F14.wireOp",EDGE,"E401"),sQuery(id+"F14.wireOp",EDGE,"E402"),sQuery(id+"F14.wireOp",EDGE,"E403"),sQuery(id+"F14.wireOp",EDGE,"E404"),sQuery(id+"F14.wireOp",EDGE,"E405"),sQuery(id+"F14.wireOp",EDGE,"E422"),sQuery(id+"F14.wireOp",EDGE,"E423"),sQuery(id+"F14.wireOp",EDGE,"E424"),sQuery(id+"F14.wireOp",EDGE,"E425"),sQuery(id+"F14.wireOp",EDGE,"E426"),sQuery(id+"F14.wireOp",EDGE,"E427"),sQuery(id+"F14.wireOp",EDGE,"E428"),sQuery(id+"F14.wireOp",EDGE,"E429"),sQuery(id+"F14.wireOp",EDGE,"E430"),sQuery(id+"F14.wireOp",EDGE,"E431"),sQuery(id+"F14.wireOp",EDGE,"E432"),sQuery(id+"F14.wireOp",EDGE,"E433"),sQuery(id+"F14.wireOp",EDGE,"E434"),sQuery(id+"F14.wireOp",EDGE,"E435"),sQuery(id+"F14.wireOp",EDGE,"E436"),sQuery(id+"F14.wireOp",EDGE,"E437"),sQuery(id+"F14.wireOp",EDGE,"E438"),sQuery(id+"F14.wireOp",EDGE,"E439"),sQuery(id+"F14.wireOp",EDGE,"E440"),sQuery(id+"F14.wireOp",EDGE,"E441"),sQuery(id+"F14.wireOp",EDGE,"E442"),sQuery(id+"F14.wireOp",EDGE,"E443"),sQuery(id+"F14.wireOp",EDGE,"E444"),sQuery(id+"F14.wireOp",EDGE,"E445"),sQuery(id+"F14.wireOp",EDGE,"E447"),sQuery(id+"F14.wireOp",EDGE,"E448"),sQuery(id+"F14.wireOp",EDGE,"E449"),sQuery(id+"F14.wireOp",EDGE,"E450"),sQuery(id+"F14.wireOp",EDGE,"E451"),sQuery(id+"F14.wireOp",EDGE,"E452"),sQuery(id+"F14.wireOp",EDGE,"E453"),sQuery(id+"F14.wireOp",EDGE,"E454"),sQuery(id+"F14.wireOp",EDGE,"E455"),sQuery(id+"F14.wireOp",EDGE,"E456"),sQuery(id+"F14.wireOp",EDGE,"E457"),sQuery(id+"F14.wireOp",EDGE,"E458"),sQuery(id+"F14.wireOp",EDGE,"E459"),sQuery(id+"F14.wireOp",EDGE,"E460"),sQuery(id+"F14.wireOp",EDGE,"E461"),sQuery(id+"F14.wireOp",EDGE,"E462"),sQuery(id+"F14.wireOp",EDGE,"E463"),sQuery(id+"F14.wireOp",EDGE,"E464"),sQuery(id+"F14.wireOp",EDGE,"E465"),sQuery(id+"F14.wireOp",EDGE,"E466"),sQuery(id+"F14.wireOp",EDGE,"E478"),sQuery(id+"F14.wireOp",EDGE,"E479"),sQuery(id+"F14.wireOp",EDGE,"E480"),sQuery(id+"F14.wireOp",EDGE,"E481"),sQuery(id+"F14.wireOp",EDGE,"E482"),sQuery(id+"F14.wireOp",EDGE,"E483"),sQuery(id+"F14.wireOp",EDGE,"E484"),sQuery(id+"F14.wireOp",EDGE,"E485"),sQuery(id+"F14.wireOp",EDGE,"E486"),sQuery(id+"F14.wireOp",EDGE,"E487"),sQuery(id+"F14.wireOp",EDGE,"E488"),sQuery(id+"F14.wireOp",EDGE,"E489"),sQuery(id+"F14.wireOp",EDGE,"E490"),sQuery(id+"F14.wireOp",EDGE,"E501"),sQuery(id+"F14.wireOp",EDGE,"E502"),sQuery(id+"F14.wireOp",EDGE,"E503"),sQuery(id+"F14.wireOp",EDGE,"E504"),sQuery(id+"F14.wireOp",EDGE,"E505"),sQuery(id+"F14.wireOp",EDGE,"E506"),sQuery(id+"F14.wireOp",EDGE,"E507"),sQuery(id+"F14.wireOp",EDGE,"E508"),sQuery(id+"F14.wireOp",EDGE,"E509"),sQuery(id+"F14.wireOp",EDGE,"E510"),sQuery(id+"F14.wireOp",EDGE,"E511"),sQuery(id+"F14.wireOp",EDGE,"E512"),sQuery(id+"F14.wireOp",EDGE,"E513"),sQuery(id+"F14.wireOp",EDGE,"E514"),sQuery(id+"F14.wireOp",EDGE,"E515"),sQuery(id+"F14.wireOp",EDGE,"E516"),sQuery(id+"F14.wireOp",EDGE,"E517"),sQuery(id+"F14.wireOp",EDGE,"E518"),sQuery(id+"F14.wireOp",EDGE,"E519"),sQuery(id+"F14.wireOp",EDGE,"E520"),sQuery(id+"F14.wireOp",EDGE,"E521"),sQuery(id+"F14.wireOp",EDGE,"E522")])]});
            var Q1;
            Q1=makeQuery(id+"F17.opPattern","COPY",BODY,{"derivedFrom":makeQuery(id+"F15.opExtrude","SWEPT_BODY",BODY,{"disambiguationData":[OSD([sQuery(id+"F14.wireOp",EDGE,"E397"),sQuery(id+"F14.wireOp",EDGE,"E398"),sQuery(id+"F14.wireOp",EDGE,"E399"),sQuery(id+"F14.wireOp",EDGE,"E400"),sQuery(id+"F14.wireOp",EDGE,"E401"),sQuery(id+"F14.wireOp",EDGE,"E402"),sQuery(id+"F14.wireOp",EDGE,"E403"),sQuery(id+"F14.wireOp",EDGE,"E404"),sQuery(id+"F14.wireOp",EDGE,"E405"),sQuery(id+"F14.wireOp",EDGE,"E422"),sQuery(id+"F14.wireOp",EDGE,"E423"),sQuery(id+"F14.wireOp",EDGE,"E424"),sQuery(id+"F14.wireOp",EDGE,"E425"),sQuery(id+"F14.wireOp",EDGE,"E426"),sQuery(id+"F14.wireOp",EDGE,"E427"),sQuery(id+"F14.wireOp",EDGE,"E428"),sQuery(id+"F14.wireOp",EDGE,"E429"),sQuery(id+"F14.wireOp",EDGE,"E430"),sQuery(id+"F14.wireOp",EDGE,"E431"),sQuery(id+"F14.wireOp",EDGE,"E432"),sQuery(id+"F14.wireOp",EDGE,"E433"),sQuery(id+"F14.wireOp",EDGE,"E434"),sQuery(id+"F14.wireOp",EDGE,"E435"),sQuery(id+"F14.wireOp",EDGE,"E436"),sQuery(id+"F14.wireOp",EDGE,"E437"),sQuery(id+"F14.wireOp",EDGE,"E438"),sQuery(id+"F14.wireOp",EDGE,"E439"),sQuery(id+"F14.wireOp",EDGE,"E440"),sQuery(id+"F14.wireOp",EDGE,"E441"),sQuery(id+"F14.wireOp",EDGE,"E442"),sQuery(id+"F14.wireOp",EDGE,"E443"),sQuery(id+"F14.wireOp",EDGE,"E444"),sQuery(id+"F14.wireOp",EDGE,"E445"),sQuery(id+"F14.wireOp",EDGE,"E447"),sQuery(id+"F14.wireOp",EDGE,"E448"),sQuery(id+"F14.wireOp",EDGE,"E449"),sQuery(id+"F14.wireOp",EDGE,"E450"),sQuery(id+"F14.wireOp",EDGE,"E451"),sQuery(id+"F14.wireOp",EDGE,"E452"),sQuery(id+"F14.wireOp",EDGE,"E453"),sQuery(id+"F14.wireOp",EDGE,"E454"),sQuery(id+"F14.wireOp",EDGE,"E455"),sQuery(id+"F14.wireOp",EDGE,"E456"),sQuery(id+"F14.wireOp",EDGE,"E457"),sQuery(id+"F14.wireOp",EDGE,"E458"),sQuery(id+"F14.wireOp",EDGE,"E459"),sQuery(id+"F14.wireOp",EDGE,"E460"),sQuery(id+"F14.wireOp",EDGE,"E461"),sQuery(id+"F14.wireOp",EDGE,"E462"),sQuery(id+"F14.wireOp",EDGE,"E463"),sQuery(id+"F14.wireOp",EDGE,"E464"),sQuery(id+"F14.wireOp",EDGE,"E465"),sQuery(id+"F14.wireOp",EDGE,"E466"),sQuery(id+"F14.wireOp",EDGE,"E478"),sQuery(id+"F14.wireOp",EDGE,"E479"),sQuery(id+"F14.wireOp",EDGE,"E480"),sQuery(id+"F14.wireOp",EDGE,"E481"),sQuery(id+"F14.wireOp",EDGE,"E482"),sQuery(id+"F14.wireOp",EDGE,"E483"),sQuery(id+"F14.wireOp",EDGE,"E484"),sQuery(id+"F14.wireOp",EDGE,"E485"),sQuery(id+"F14.wireOp",EDGE,"E486"),sQuery(id+"F14.wireOp",EDGE,"E487"),sQuery(id+"F14.wireOp",EDGE,"E488"),sQuery(id+"F14.wireOp",EDGE,"E489"),sQuery(id+"F14.wireOp",EDGE,"E490"),sQuery(id+"F14.wireOp",EDGE,"E501"),sQuery(id+"F14.wireOp",EDGE,"E502"),sQuery(id+"F14.wireOp",EDGE,"E503"),sQuery(id+"F14.wireOp",EDGE,"E504"),sQuery(id+"F14.wireOp",EDGE,"E505"),sQuery(id+"F14.wireOp",EDGE,"E506"),sQuery(id+"F14.wireOp",EDGE,"E507"),sQuery(id+"F14.wireOp",EDGE,"E508"),sQuery(id+"F14.wireOp",EDGE,"E509"),sQuery(id+"F14.wireOp",EDGE,"E510"),sQuery(id+"F14.wireOp",EDGE,"E511"),sQuery(id+"F14.wireOp",EDGE,"E512"),sQuery(id+"F14.wireOp",EDGE,"E513"),sQuery(id+"F14.wireOp",EDGE,"E514"),sQuery(id+"F14.wireOp",EDGE,"E515"),sQuery(id+"F14.wireOp",EDGE,"E516"),sQuery(id+"F14.wireOp",EDGE,"E517"),sQuery(id+"F14.wireOp",EDGE,"E518"),sQuery(id+"F14.wireOp",EDGE,"E519"),sQuery(id+"F14.wireOp",EDGE,"E520"),sQuery(id+"F14.wireOp",EDGE,"E521"),sQuery(id+"F14.wireOp",EDGE,"E522")])]}),"instanceName":"1"});
            transform(context, id + "F18", {"entities" : qUnion([Q0, Q1]), "transformType" : TransformType.TRANSLATION_3D, "dx" : -750 * mm, "dy" : 0 * mm, "dz" : 0 * mm, "makeCopy" : true});
        }
        {
            var Q0;
            Q0=makeQuery(id+"F17.opPattern","COPY",BODY,{"derivedFrom":makeQuery(id+"F15.opExtrude","SWEPT_BODY",BODY,{"disambiguationData":[OSD([sQuery(id+"F14.wireOp",EDGE,"E397"),sQuery(id+"F14.wireOp",EDGE,"E398"),sQuery(id+"F14.wireOp",EDGE,"E399"),sQuery(id+"F14.wireOp",EDGE,"E400"),sQuery(id+"F14.wireOp",EDGE,"E401"),sQuery(id+"F14.wireOp",EDGE,"E402"),sQuery(id+"F14.wireOp",EDGE,"E403"),sQuery(id+"F14.wireOp",EDGE,"E404"),sQuery(id+"F14.wireOp",EDGE,"E405"),sQuery(id+"F14.wireOp",EDGE,"E422"),sQuery(id+"F14.wireOp",EDGE,"E423"),sQuery(id+"F14.wireOp",EDGE,"E424"),sQuery(id+"F14.wireOp",EDGE,"E425"),sQuery(id+"F14.wireOp",EDGE,"E426"),sQuery(id+"F14.wireOp",EDGE,"E427"),sQuery(id+"F14.wireOp",EDGE,"E428"),sQuery(id+"F14.wireOp",EDGE,"E429"),sQuery(id+"F14.wireOp",EDGE,"E430"),sQuery(id+"F14.wireOp",EDGE,"E431"),sQuery(id+"F14.wireOp",EDGE,"E432"),sQuery(id+"F14.wireOp",EDGE,"E433"),sQuery(id+"F14.wireOp",EDGE,"E434"),sQuery(id+"F14.wireOp",EDGE,"E435"),sQuery(id+"F14.wireOp",EDGE,"E436"),sQuery(id+"F14.wireOp",EDGE,"E437"),sQuery(id+"F14.wireOp",EDGE,"E438"),sQuery(id+"F14.wireOp",EDGE,"E439"),sQuery(id+"F14.wireOp",EDGE,"E440"),sQuery(id+"F14.wireOp",EDGE,"E441"),sQuery(id+"F14.wireOp",EDGE,"E442"),sQuery(id+"F14.wireOp",EDGE,"E443"),sQuery(id+"F14.wireOp",EDGE,"E444"),sQuery(id+"F14.wireOp",EDGE,"E445"),sQuery(id+"F14.wireOp",EDGE,"E447"),sQuery(id+"F14.wireOp",EDGE,"E448"),sQuery(id+"F14.wireOp",EDGE,"E449"),sQuery(id+"F14.wireOp",EDGE,"E450"),sQuery(id+"F14.wireOp",EDGE,"E451"),sQuery(id+"F14.wireOp",EDGE,"E452"),sQuery(id+"F14.wireOp",EDGE,"E453"),sQuery(id+"F14.wireOp",EDGE,"E454"),sQuery(id+"F14.wireOp",EDGE,"E455"),sQuery(id+"F14.wireOp",EDGE,"E456"),sQuery(id+"F14.wireOp",EDGE,"E457"),sQuery(id+"F14.wireOp",EDGE,"E458"),sQuery(id+"F14.wireOp",EDGE,"E459"),sQuery(id+"F14.wireOp",EDGE,"E460"),sQuery(id+"F14.wireOp",EDGE,"E461"),sQuery(id+"F14.wireOp",EDGE,"E462"),sQuery(id+"F14.wireOp",EDGE,"E463"),sQuery(id+"F14.wireOp",EDGE,"E464"),sQuery(id+"F14.wireOp",EDGE,"E465"),sQuery(id+"F14.wireOp",EDGE,"E466"),sQuery(id+"F14.wireOp",EDGE,"E478"),sQuery(id+"F14.wireOp",EDGE,"E479"),sQuery(id+"F14.wireOp",EDGE,"E480"),sQuery(id+"F14.wireOp",EDGE,"E481"),sQuery(id+"F14.wireOp",EDGE,"E482"),sQuery(id+"F14.wireOp",EDGE,"E483"),sQuery(id+"F14.wireOp",EDGE,"E484"),sQuery(id+"F14.wireOp",EDGE,"E485"),sQuery(id+"F14.wireOp",EDGE,"E486"),sQuery(id+"F14.wireOp",EDGE,"E487"),sQuery(id+"F14.wireOp",EDGE,"E488"),sQuery(id+"F14.wireOp",EDGE,"E489"),sQuery(id+"F14.wireOp",EDGE,"E490"),sQuery(id+"F14.wireOp",EDGE,"E501"),sQuery(id+"F14.wireOp",EDGE,"E502"),sQuery(id+"F14.wireOp",EDGE,"E503"),sQuery(id+"F14.wireOp",EDGE,"E504"),sQuery(id+"F14.wireOp",EDGE,"E505"),sQuery(id+"F14.wireOp",EDGE,"E506"),sQuery(id+"F14.wireOp",EDGE,"E507"),sQuery(id+"F14.wireOp",EDGE,"E508"),sQuery(id+"F14.wireOp",EDGE,"E509"),sQuery(id+"F14.wireOp",EDGE,"E510"),sQuery(id+"F14.wireOp",EDGE,"E511"),sQuery(id+"F14.wireOp",EDGE,"E512"),sQuery(id+"F14.wireOp",EDGE,"E513"),sQuery(id+"F14.wireOp",EDGE,"E514"),sQuery(id+"F14.wireOp",EDGE,"E515"),sQuery(id+"F14.wireOp",EDGE,"E516"),sQuery(id+"F14.wireOp",EDGE,"E517"),sQuery(id+"F14.wireOp",EDGE,"E518"),sQuery(id+"F14.wireOp",EDGE,"E519"),sQuery(id+"F14.wireOp",EDGE,"E520"),sQuery(id+"F14.wireOp",EDGE,"E521"),sQuery(id+"F14.wireOp",EDGE,"E522")])]}),"instanceName":"1"});
            var Q1;
            Q1=makeQuery(id+"F15.opExtrude","SWEPT_BODY",BODY,{"disambiguationData":[OSD([sQuery(id+"F14.wireOp",EDGE,"E397"),sQuery(id+"F14.wireOp",EDGE,"E398"),sQuery(id+"F14.wireOp",EDGE,"E399"),sQuery(id+"F14.wireOp",EDGE,"E400"),sQuery(id+"F14.wireOp",EDGE,"E401"),sQuery(id+"F14.wireOp",EDGE,"E402"),sQuery(id+"F14.wireOp",EDGE,"E403"),sQuery(id+"F14.wireOp",EDGE,"E404"),sQuery(id+"F14.wireOp",EDGE,"E405"),sQuery(id+"F14.wireOp",EDGE,"E422"),sQuery(id+"F14.wireOp",EDGE,"E423"),sQuery(id+"F14.wireOp",EDGE,"E424"),sQuery(id+"F14.wireOp",EDGE,"E425"),sQuery(id+"F14.wireOp",EDGE,"E426"),sQuery(id+"F14.wireOp",EDGE,"E427"),sQuery(id+"F14.wireOp",EDGE,"E428"),sQuery(id+"F14.wireOp",EDGE,"E429"),sQuery(id+"F14.wireOp",EDGE,"E430"),sQuery(id+"F14.wireOp",EDGE,"E431"),sQuery(id+"F14.wireOp",EDGE,"E432"),sQuery(id+"F14.wireOp",EDGE,"E433"),sQuery(id+"F14.wireOp",EDGE,"E434"),sQuery(id+"F14.wireOp",EDGE,"E435"),sQuery(id+"F14.wireOp",EDGE,"E436"),sQuery(id+"F14.wireOp",EDGE,"E437"),sQuery(id+"F14.wireOp",EDGE,"E438"),sQuery(id+"F14.wireOp",EDGE,"E439"),sQuery(id+"F14.wireOp",EDGE,"E440"),sQuery(id+"F14.wireOp",EDGE,"E441"),sQuery(id+"F14.wireOp",EDGE,"E442"),sQuery(id+"F14.wireOp",EDGE,"E443"),sQuery(id+"F14.wireOp",EDGE,"E444"),sQuery(id+"F14.wireOp",EDGE,"E445"),sQuery(id+"F14.wireOp",EDGE,"E447"),sQuery(id+"F14.wireOp",EDGE,"E448"),sQuery(id+"F14.wireOp",EDGE,"E449"),sQuery(id+"F14.wireOp",EDGE,"E450"),sQuery(id+"F14.wireOp",EDGE,"E451"),sQuery(id+"F14.wireOp",EDGE,"E452"),sQuery(id+"F14.wireOp",EDGE,"E453"),sQuery(id+"F14.wireOp",EDGE,"E454"),sQuery(id+"F14.wireOp",EDGE,"E455"),sQuery(id+"F14.wireOp",EDGE,"E456"),sQuery(id+"F14.wireOp",EDGE,"E457"),sQuery(id+"F14.wireOp",EDGE,"E458"),sQuery(id+"F14.wireOp",EDGE,"E459"),sQuery(id+"F14.wireOp",EDGE,"E460"),sQuery(id+"F14.wireOp",EDGE,"E461"),sQuery(id+"F14.wireOp",EDGE,"E462"),sQuery(id+"F14.wireOp",EDGE,"E463"),sQuery(id+"F14.wireOp",EDGE,"E464"),sQuery(id+"F14.wireOp",EDGE,"E465"),sQuery(id+"F14.wireOp",EDGE,"E466"),sQuery(id+"F14.wireOp",EDGE,"E478"),sQuery(id+"F14.wireOp",EDGE,"E479"),sQuery(id+"F14.wireOp",EDGE,"E480"),sQuery(id+"F14.wireOp",EDGE,"E481"),sQuery(id+"F14.wireOp",EDGE,"E482"),sQuery(id+"F14.wireOp",EDGE,"E483"),sQuery(id+"F14.wireOp",EDGE,"E484"),sQuery(id+"F14.wireOp",EDGE,"E485"),sQuery(id+"F14.wireOp",EDGE,"E486"),sQuery(id+"F14.wireOp",EDGE,"E487"),sQuery(id+"F14.wireOp",EDGE,"E488"),sQuery(id+"F14.wireOp",EDGE,"E489"),sQuery(id+"F14.wireOp",EDGE,"E490"),sQuery(id+"F14.wireOp",EDGE,"E501"),sQuery(id+"F14.wireOp",EDGE,"E502"),sQuery(id+"F14.wireOp",EDGE,"E503"),sQuery(id+"F14.wireOp",EDGE,"E504"),sQuery(id+"F14.wireOp",EDGE,"E505"),sQuery(id+"F14.wireOp",EDGE,"E506"),sQuery(id+"F14.wireOp",EDGE,"E507"),sQuery(id+"F14.wireOp",EDGE,"E508"),sQuery(id+"F14.wireOp",EDGE,"E509"),sQuery(id+"F14.wireOp",EDGE,"E510"),sQuery(id+"F14.wireOp",EDGE,"E511"),sQuery(id+"F14.wireOp",EDGE,"E512"),sQuery(id+"F14.wireOp",EDGE,"E513"),sQuery(id+"F14.wireOp",EDGE,"E514"),sQuery(id+"F14.wireOp",EDGE,"E515"),sQuery(id+"F14.wireOp",EDGE,"E516"),sQuery(id+"F14.wireOp",EDGE,"E517"),sQuery(id+"F14.wireOp",EDGE,"E518"),sQuery(id+"F14.wireOp",EDGE,"E519"),sQuery(id+"F14.wireOp",EDGE,"E520"),sQuery(id+"F14.wireOp",EDGE,"E521"),sQuery(id+"F14.wireOp",EDGE,"E522")])]});
            transform(context, id + "F19", {"entities" : qUnion([Q0, Q1]), "transformType" : TransformType.TRANSLATION_3D, "dx" : -353 * mm, "dy" : 0 * mm, "dz" : 0 * mm, "makeCopy" : true});
        }
        {
            var Q0;
            Q0=qCreatedBy(makeId("Top.planeOp"),FACE);
            cPlane(context, id + "F20", {"entities" : qUnion([Q0]), "cplaneType" : CPlaneType.OFFSET, "offset" : 20 * mm, "width" : 150 * mm, "height" : 150 * mm});
        }
        {
            var Q0;
            Q0=qCreatedBy(id+"F20.planeOp",FACE);
            var sketch = newSketch(context, id + "F21", { "sketchPlane" : qUnion([Q0])});
            skLineSegment(sketch, "E524", {"start": v(25.7, -17.22) * mm, "end": v(25.7, -25.12) * mm});
            skLineSegment(sketch, "E525", {"start": v(22.1, -21.63) * mm, "end": v(30.9, -21.63) * mm});
            skLineSegment(sketch, "E526", {"start": v(25.7, -40.02) * mm, "end": v(25.7, -32.12) * mm});
            skLineSegment(sketch, "E527", {"start": v(22.1, -35.63) * mm, "end": v(30.9, -35.63) * mm});
            skLineSegment(sketch, "E528", {"start": v(28.7, -30.77) * mm, "end": v(27.2, -30.77) * mm});
            skLineSegment(sketch, "E529", {"start": v(27.2, -32.77) * mm, "end": v(23.2, -32.77) * mm});
            skLineSegment(sketch, "E530", {"start": v(27.2, -32.77) * mm, "end": v(27.2, -30.77) * mm});
            skLineSegment(sketch, "E531", {"start": v(28.7, -26.48) * mm, "end": v(27.2, -26.48) * mm});
            skLineSegment(sketch, "E532", {"start": v(27.2, -24.48) * mm, "end": v(23.2, -24.48) * mm});
            skLineSegment(sketch, "E533", {"start": v(27.2, -24.48) * mm, "end": v(27.2, -26.48) * mm});
            skLineSegment(sketch, "E534", {"start": v(23.2, -24.48) * mm, "end": v(23.2, -26.12) * mm});
            skLineSegment(sketch, "E535", {"start": v(23.2, -26.12) * mm, "end": v(21.9, -26.12) * mm});
            skLineSegment(sketch, "E536", {"start": v(23.2, -32.77) * mm, "end": v(21.9, -26.12) * mm});
            skLineSegment(sketch, "E537", {"start": v(27.34, -20.94) * mm, "end": v(26.38, -19.97) * mm});
            skLineSegment(sketch, "E538", {"start": v(26.38, -19.97) * mm, "end": v(25, -19.97) * mm});
            skLineSegment(sketch, "E539", {"start": v(25, -19.97) * mm, "end": v(24.04, -20.94) * mm});
            skLineSegment(sketch, "E540", {"start": v(24.04, -20.94) * mm, "end": v(24.04, -22.3) * mm});
            skLineSegment(sketch, "E541", {"start": v(24.04, -22.3) * mm, "end": v(25, -23.28) * mm});
            skLineSegment(sketch, "E542", {"start": v(25, -23.28) * mm, "end": v(26.38, -23.28) * mm});
            skLineSegment(sketch, "E543", {"start": v(26.38, -23.28) * mm, "end": v(27.34, -22.3) * mm});
            skLineSegment(sketch, "E544", {"start": v(27.34, -22.3) * mm, "end": v(27.34, -20.94) * mm});
            skLineSegment(sketch, "E545", {"start": v(27.34, -34.94) * mm, "end": v(26.38, -33.98) * mm});
            skLineSegment(sketch, "E546", {"start": v(26.38, -33.98) * mm, "end": v(25, -33.98) * mm});
            skLineSegment(sketch, "E547", {"start": v(25, -33.98) * mm, "end": v(24.04, -34.94) * mm});
            skLineSegment(sketch, "E548", {"start": v(24.04, -34.94) * mm, "end": v(24.04, -36.3) * mm});
            skLineSegment(sketch, "E549", {"start": v(24.04, -36.3) * mm, "end": v(25, -37.28) * mm});
            skLineSegment(sketch, "E550", {"start": v(25, -37.28) * mm, "end": v(26.38, -37.28) * mm});
            skLineSegment(sketch, "E551", {"start": v(26.38, -37.28) * mm, "end": v(27.34, -36.3) * mm});
            skLineSegment(sketch, "E552", {"start": v(27.34, -36.3) * mm, "end": v(27.34, -34.94) * mm});
            skLineSegment(sketch, "E553", {"start": v(27.7, -18.62) * mm, "end": v(28.7, -19.62) * mm});
            skLineSegment(sketch, "E554", {"start": v(28.7, -37.62) * mm, "end": v(27.7, -38.62) * mm});
            skLineSegment(sketch, "E555", {"start": v(25.7, -18.83) * mm, "end": v(26.44, -18.83) * mm});
            skLineSegment(sketch, "E556", {"start": v(26.44, -18.83) * mm, "end": v(26.44, -18.62) * mm});
            skLineSegment(sketch, "E557", {"start": v(25.7, -18.83) * mm, "end": v(24.94, -18.83) * mm});
            skLineSegment(sketch, "E558", {"start": v(24.94, -18.83) * mm, "end": v(24.94, -18.62) * mm});
            skLineSegment(sketch, "E559", {"start": v(27.7, -18.62) * mm, "end": v(26.44, -18.62) * mm});
            skLineSegment(sketch, "E560", {"start": v(28.5, -21.63) * mm, "end": v(28.5, -22.38) * mm});
            skLineSegment(sketch, "E561", {"start": v(28.5, -22.38) * mm, "end": v(28.7, -22.38) * mm});
            skLineSegment(sketch, "E562", {"start": v(28.5, -21.63) * mm, "end": v(28.5, -20.88) * mm});
            skLineSegment(sketch, "E563", {"start": v(28.5, -20.88) * mm, "end": v(28.7, -20.88) * mm});
            skLineSegment(sketch, "E564", {"start": v(28.5, -35.63) * mm, "end": v(28.5, -34.88) * mm});
            skLineSegment(sketch, "E565", {"start": v(28.5, -34.88) * mm, "end": v(28.7, -34.88) * mm});
            skLineSegment(sketch, "E566", {"start": v(28.5, -35.63) * mm, "end": v(28.5, -36.38) * mm});
            skLineSegment(sketch, "E567", {"start": v(28.5, -36.38) * mm, "end": v(28.7, -36.38) * mm});
            skLineSegment(sketch, "E568", {"start": v(25.7, -38.43) * mm, "end": v(26.44, -38.43) * mm});
            skLineSegment(sketch, "E569", {"start": v(26.44, -38.43) * mm, "end": v(26.44, -38.62) * mm});
            skLineSegment(sketch, "E570", {"start": v(25.7, -38.43) * mm, "end": v(24.94, -38.43) * mm});
            skLineSegment(sketch, "E571", {"start": v(24.94, -38.43) * mm, "end": v(24.94, -38.62) * mm});
            skLineSegment(sketch, "E572", {"start": v(28.7, -19.62) * mm, "end": v(28.7, -20.88) * mm});
            skLineSegment(sketch, "E573", {"start": v(28.7, -22.38) * mm, "end": v(28.7, -26.48) * mm});
            skLineSegment(sketch, "E574", {"start": v(27.7, -38.62) * mm, "end": v(26.44, -38.62) * mm});
            skLineSegment(sketch, "E575", {"start": v(28.7, -37.62) * mm, "end": v(28.7, -36.38) * mm});
            skLineSegment(sketch, "E576", {"start": v(28.7, -34.88) * mm, "end": v(28.7, -30.77) * mm});
            skLineSegment(sketch, "E577", {"start": v(18.7, -13.92) * mm, "end": v(18.7, -42.92) * mm});
            skLineSegment(sketch, "E578", {"start": v(20.84, -18.62) * mm, "end": v(20.84, -20.12) * mm});
            skLineSegment(sketch, "E579", {"start": v(22.84, -20.12) * mm, "end": v(22.84, -24.12) * mm});
            skLineSegment(sketch, "E580", {"start": v(22.84, -20.12) * mm, "end": v(20.84, -20.12) * mm});
            skLineSegment(sketch, "E581", {"start": v(16.54, -18.62) * mm, "end": v(16.54, -20.12) * mm});
            skLineSegment(sketch, "E582", {"start": v(14.54, -20.12) * mm, "end": v(14.54, -24.12) * mm});
            skLineSegment(sketch, "E583", {"start": v(14.54, -20.12) * mm, "end": v(16.54, -20.12) * mm});
            skLineSegment(sketch, "E584", {"start": v(14.54, -24.12) * mm, "end": v(16.2, -24.12) * mm});
            skLineSegment(sketch, "E585", {"start": v(16.2, -24.12) * mm, "end": v(16.2, -25.42) * mm});
            skLineSegment(sketch, "E586", {"start": v(22.84, -24.12) * mm, "end": v(16.2, -25.42) * mm});
            skLineSegment(sketch, "E587", {"start": v(16.54, -38.62) * mm, "end": v(16.54, -37.12) * mm});
            skLineSegment(sketch, "E588", {"start": v(14.54, -37.12) * mm, "end": v(14.54, -33.12) * mm});
            skLineSegment(sketch, "E589", {"start": v(14.54, -37.12) * mm, "end": v(16.54, -37.12) * mm});
            skLineSegment(sketch, "E590", {"start": v(20.84, -38.62) * mm, "end": v(20.84, -37.12) * mm});
            skLineSegment(sketch, "E591", {"start": v(22.84, -37.12) * mm, "end": v(22.84, -33.12) * mm});
            skLineSegment(sketch, "E592", {"start": v(22.84, -37.12) * mm, "end": v(20.84, -37.12) * mm});
            skLineSegment(sketch, "E593", {"start": v(22.84, -33.12) * mm, "end": v(21.2, -33.12) * mm});
            skLineSegment(sketch, "E594", {"start": v(21.2, -33.12) * mm, "end": v(21.2, -31.83) * mm});
            skLineSegment(sketch, "E595", {"start": v(14.54, -33.12) * mm, "end": v(21.2, -31.83) * mm});
            skLineSegment(sketch, "E596", {"start": v(24.94, -18.62) * mm, "end": v(20.84, -18.62) * mm});
            skLineSegment(sketch, "E597", {"start": v(24.94, -38.62) * mm, "end": v(20.84, -38.62) * mm});
            skLineSegment(sketch, "E598", {"start": v(6.1, -28.62) * mm, "end": v(31.6, -28.62) * mm});
            skLineSegment(sketch, "E599", {"start": v(11.7, -17.22) * mm, "end": v(11.7, -25.12) * mm});
            skLineSegment(sketch, "E600", {"start": v(15.3, -21.63) * mm, "end": v(6.5, -21.63) * mm});
            skLineSegment(sketch, "E601", {"start": v(10.04, -20.94) * mm, "end": v(11, -19.97) * mm});
            skLineSegment(sketch, "E602", {"start": v(11, -19.97) * mm, "end": v(12.38, -19.97) * mm});
            skLineSegment(sketch, "E603", {"start": v(12.38, -19.97) * mm, "end": v(13.34, -20.94) * mm});
            skLineSegment(sketch, "E604", {"start": v(13.34, -20.94) * mm, "end": v(13.34, -22.3) * mm});
            skLineSegment(sketch, "E605", {"start": v(13.34, -22.3) * mm, "end": v(12.38, -23.28) * mm});
            skLineSegment(sketch, "E606", {"start": v(12.38, -23.28) * mm, "end": v(11, -23.28) * mm});
            skLineSegment(sketch, "E607", {"start": v(11, -23.28) * mm, "end": v(10.04, -22.3) * mm});
            skLineSegment(sketch, "E608", {"start": v(10.04, -22.3) * mm, "end": v(10.04, -20.94) * mm});
            skLineSegment(sketch, "E609", {"start": v(9.7, -18.62) * mm, "end": v(8.7, -19.62) * mm});
            skLineSegment(sketch, "E610", {"start": v(11.7, -18.83) * mm, "end": v(10.94, -18.83) * mm});
            skLineSegment(sketch, "E611", {"start": v(10.94, -18.83) * mm, "end": v(10.94, -18.62) * mm});
            skLineSegment(sketch, "E612", {"start": v(11.7, -18.83) * mm, "end": v(12.44, -18.83) * mm});
            skLineSegment(sketch, "E613", {"start": v(12.44, -18.83) * mm, "end": v(12.44, -18.62) * mm});
            skLineSegment(sketch, "E614", {"start": v(9.7, -18.62) * mm, "end": v(10.94, -18.62) * mm});
            skLineSegment(sketch, "E615", {"start": v(8.9, -21.63) * mm, "end": v(8.9, -22.38) * mm});
            skLineSegment(sketch, "E616", {"start": v(8.9, -22.38) * mm, "end": v(8.7, -22.38) * mm});
            skLineSegment(sketch, "E617", {"start": v(8.9, -21.63) * mm, "end": v(8.9, -20.88) * mm});
            skLineSegment(sketch, "E618", {"start": v(8.9, -20.88) * mm, "end": v(8.7, -20.88) * mm});
            skLineSegment(sketch, "E619", {"start": v(8.7, -19.62) * mm, "end": v(8.7, -20.88) * mm});
            skLineSegment(sketch, "E620", {"start": v(8.7, -22.38) * mm, "end": v(8.7, -26.48) * mm});
            skLineSegment(sketch, "E621", {"start": v(12.44, -18.62) * mm, "end": v(16.54, -18.62) * mm});
            skLineSegment(sketch, "E622", {"start": v(11.7, -40.02) * mm, "end": v(11.7, -32.12) * mm});
            skLineSegment(sketch, "E623", {"start": v(15.3, -35.63) * mm, "end": v(6.5, -35.63) * mm});
            skLineSegment(sketch, "E624", {"start": v(10.04, -34.94) * mm, "end": v(11, -33.98) * mm});
            skLineSegment(sketch, "E625", {"start": v(11, -33.98) * mm, "end": v(12.38, -33.98) * mm});
            skLineSegment(sketch, "E626", {"start": v(12.38, -33.98) * mm, "end": v(13.34, -34.94) * mm});
            skLineSegment(sketch, "E627", {"start": v(13.34, -34.94) * mm, "end": v(13.34, -36.3) * mm});
            skLineSegment(sketch, "E628", {"start": v(13.34, -36.3) * mm, "end": v(12.38, -37.28) * mm});
            skLineSegment(sketch, "E629", {"start": v(12.38, -37.28) * mm, "end": v(11, -37.28) * mm});
            skLineSegment(sketch, "E630", {"start": v(11, -37.28) * mm, "end": v(10.04, -36.3) * mm});
            skLineSegment(sketch, "E631", {"start": v(10.04, -36.3) * mm, "end": v(10.04, -34.94) * mm});
            skLineSegment(sketch, "E632", {"start": v(8.7, -37.62) * mm, "end": v(9.7, -38.62) * mm});
            skLineSegment(sketch, "E633", {"start": v(8.9, -35.63) * mm, "end": v(8.9, -34.88) * mm});
            skLineSegment(sketch, "E634", {"start": v(8.9, -34.88) * mm, "end": v(8.7, -34.88) * mm});
            skLineSegment(sketch, "E635", {"start": v(8.9, -35.63) * mm, "end": v(8.9, -36.38) * mm});
            skLineSegment(sketch, "E636", {"start": v(8.9, -36.38) * mm, "end": v(8.7, -36.38) * mm});
            skLineSegment(sketch, "E637", {"start": v(11.7, -38.43) * mm, "end": v(10.94, -38.43) * mm});
            skLineSegment(sketch, "E638", {"start": v(10.94, -38.43) * mm, "end": v(10.94, -38.62) * mm});
            skLineSegment(sketch, "E639", {"start": v(11.7, -38.43) * mm, "end": v(12.44, -38.43) * mm});
            skLineSegment(sketch, "E640", {"start": v(12.44, -38.43) * mm, "end": v(12.44, -38.62) * mm});
            skLineSegment(sketch, "E641", {"start": v(9.7, -38.62) * mm, "end": v(10.94, -38.62) * mm});
            skLineSegment(sketch, "E642", {"start": v(8.7, -37.62) * mm, "end": v(8.7, -36.38) * mm});
            skLineSegment(sketch, "E643", {"start": v(8.7, -34.88) * mm, "end": v(8.7, -30.77) * mm});
            skLineSegment(sketch, "E644", {"start": v(12.44, -38.62) * mm, "end": v(16.54, -38.62) * mm});
            skLineSegment(sketch, "E645", {"start": v(8.7, -26.48) * mm, "end": v(10.2, -26.48) * mm});
            skLineSegment(sketch, "E646", {"start": v(10.2, -24.48) * mm, "end": v(14.2, -24.48) * mm});
            skLineSegment(sketch, "E647", {"start": v(10.2, -24.48) * mm, "end": v(10.2, -26.48) * mm});
            skLineSegment(sketch, "E648", {"start": v(8.7, -30.77) * mm, "end": v(10.2, -30.77) * mm});
            skLineSegment(sketch, "E649", {"start": v(10.2, -32.77) * mm, "end": v(14.2, -32.77) * mm});
            skLineSegment(sketch, "E650", {"start": v(10.2, -32.77) * mm, "end": v(10.2, -30.77) * mm});
            skLineSegment(sketch, "E651", {"start": v(14.2, -32.77) * mm, "end": v(14.2, -31.12) * mm});
            skLineSegment(sketch, "E652", {"start": v(14.2, -31.12) * mm, "end": v(15.5, -31.12) * mm});
            skLineSegment(sketch, "E653", {"start": v(14.2, -24.48) * mm, "end": v(15.5, -31.12) * mm});
            skCircle(sketch, "E654", {"center": v(18.7, -28.62) * mm, "radius": 1.6 * mm});
            skSolve(sketch);
        }
        {
            var Q0;
            {var subQ21=sQuery(id+"F21.wireOp",EDGE,"E584");Q0=makeQuery(id+"F21.imprint","IMPRINT",FACE,{"disambiguationData":[TD([[makeQuery(id+"F21.imprint","IMPRINT",EDGE,{"derivedFrom":subQ21}),-1.0]])]});}
            var Q1;
            Q1=makeQuery(id+"F21.imprint","IMPRINT",FACE,{"disambiguationData":[TD([[makeQuery(id+"F21.imprint","IMPRINT",EDGE,{"derivedFrom":sQuery(id+"F21.wireOp",EDGE,"E581")}),-1.0]])]});
            var Q2;
            {var subQ1=sQuery(id+"F21.wireOp",EDGE,"E626");Q2=makeQuery(id+"F21.imprint","IMPRINT",FACE,{"disambiguationData":[TD([[makeQuery(id+"F21.imprint","IMPRINT",EDGE,{"derivedFrom":subQ1}),1.0]])]});}
            var Q3;
            Q3=makeQuery(id+"F21.imprint","IMPRINT",FACE,{"disambiguationData":[TD([[makeQuery(id+"F21.imprint","IMPRINT",EDGE,{"derivedFrom":sQuery(id+"F21.wireOp",EDGE,"E587")}),1.0]])]});
            var Q4;
            {var subQ8=sQuery(id+"F21.wireOp",EDGE,"E601");Q4=makeQuery(id+"F21.imprint","IMPRINT",FACE,{"disambiguationData":[TD([[makeQuery(id+"F21.imprint","IMPRINT",EDGE,{"derivedFrom":subQ8}),1.0]])]});}
            var Q5;
            {var subQ0=sQuery(id+"F21.wireOp",EDGE,"E603");Q5=makeQuery(id+"F21.imprint","IMPRINT",FACE,{"disambiguationData":[TD([[makeQuery(id+"F21.imprint","IMPRINT",EDGE,{"derivedFrom":subQ0}),-1.0]])]});}
            var Q6;
            {var subQ0=sQuery(id+"F21.wireOp",EDGE,"E654");var subQ1=sQuery(id+"F21.wireOp",EDGE,"E577");var subQ2=makeQuery(id+"F21.imprint","INTERSECT",VERTEX,{"disambiguationData":[OD(0.0)],"derivedFrom":[subQ1,subQ0]});Q6=makeQuery(id+"F21.imprint","IMPRINT",FACE,{"disambiguationData":[TD([[makeQuery(id+"F21.imprint","IMPRINT",EDGE,{"disambiguationData":[TD([[subQ2,-1.0]])],"derivedFrom":subQ1}),1.0]])]});}
            var Q7;
            Q7=makeQuery(id+"F21.imprint","IMPRINT",FACE,{"disambiguationData":[TD([[makeQuery(id+"F21.imprint","IMPRINT",EDGE,{"derivedFrom":sQuery(id+"F21.wireOp",EDGE,"E528")}),1.0]])]});
            var Q8;
            {var subQ0=sQuery(id+"F21.wireOp",EDGE,"E654");var subQ1=sQuery(id+"F21.wireOp",EDGE,"E577");var subQ2=makeQuery(id+"F21.imprint","INTERSECT",VERTEX,{"disambiguationData":[OD(0.0)],"derivedFrom":[subQ1,subQ0]});Q8=makeQuery(id+"F21.imprint","IMPRINT",FACE,{"disambiguationData":[TD([[makeQuery(id+"F21.imprint","IMPRINT",EDGE,{"disambiguationData":[TD([[subQ2,-1.0]])],"derivedFrom":subQ1}),-1.0]])]});}
            var Q9;
            {var subQ3=sQuery(id+"F21.wireOp",EDGE,"E539");Q9=makeQuery(id+"F21.imprint","IMPRINT",FACE,{"disambiguationData":[TD([[makeQuery(id+"F21.imprint","IMPRINT",EDGE,{"derivedFrom":subQ3}),-1.0]])]});}
            var Q10;
            {var subQ2=sQuery(id+"F21.wireOp",EDGE,"E537");Q10=makeQuery(id+"F21.imprint","IMPRINT",FACE,{"disambiguationData":[TD([[makeQuery(id+"F21.imprint","IMPRINT",EDGE,{"derivedFrom":subQ2}),-1.0]])]});}
            var Q11;
            {var subQ0=sQuery(id+"F21.wireOp",EDGE,"E539");Q11=makeQuery(id+"F21.imprint","IMPRINT",FACE,{"disambiguationData":[TD([[makeQuery(id+"F21.imprint","IMPRINT",EDGE,{"derivedFrom":subQ0}),1.0]])]});}
            var Q12;
            {var subQ1=sQuery(id+"F21.wireOp",EDGE,"E537");Q12=makeQuery(id+"F21.imprint","IMPRINT",FACE,{"disambiguationData":[TD([[makeQuery(id+"F21.imprint","IMPRINT",EDGE,{"derivedFrom":subQ1}),1.0]])]});}
            var Q13;
            {var subQ0=sQuery(id+"F21.wireOp",EDGE,"E541");Q13=makeQuery(id+"F21.imprint","IMPRINT",FACE,{"disambiguationData":[TD([[makeQuery(id+"F21.imprint","IMPRINT",EDGE,{"derivedFrom":subQ0}),1.0]])]});}
            var Q14;
            {var subQ0=sQuery(id+"F21.wireOp",EDGE,"E543");Q14=makeQuery(id+"F21.imprint","IMPRINT",FACE,{"disambiguationData":[TD([[makeQuery(id+"F21.imprint","IMPRINT",EDGE,{"derivedFrom":subQ0}),1.0]])]});}
            var Q15;
            Q15=makeQuery(id+"F21.imprint","IMPRINT",FACE,{"disambiguationData":[TD([[makeQuery(id+"F21.imprint","IMPRINT",EDGE,{"derivedFrom":sQuery(id+"F21.wireOp",EDGE,"E531")}),-1.0]])]});
            var Q16;
            {var subQ5=sQuery(id+"F21.wireOp",EDGE,"E549");Q16=makeQuery(id+"F21.imprint","IMPRINT",FACE,{"disambiguationData":[TD([[makeQuery(id+"F21.imprint","IMPRINT",EDGE,{"derivedFrom":subQ5}),-1.0]])]});}
            var Q17;
            {var subQ3=sQuery(id+"F21.wireOp",EDGE,"E551");Q17=makeQuery(id+"F21.imprint","IMPRINT",FACE,{"disambiguationData":[TD([[makeQuery(id+"F21.imprint","IMPRINT",EDGE,{"derivedFrom":subQ3}),-1.0]])]});}
            var Q18;
            {var subQ0=sQuery(id+"F21.wireOp",EDGE,"E549");Q18=makeQuery(id+"F21.imprint","IMPRINT",FACE,{"disambiguationData":[TD([[makeQuery(id+"F21.imprint","IMPRINT",EDGE,{"derivedFrom":subQ0}),1.0]])]});}
            var Q19;
            {var subQ0=sQuery(id+"F21.wireOp",EDGE,"E551");Q19=makeQuery(id+"F21.imprint","IMPRINT",FACE,{"disambiguationData":[TD([[makeQuery(id+"F21.imprint","IMPRINT",EDGE,{"derivedFrom":subQ0}),1.0]])]});}
            var Q20;
            {var subQ0=sQuery(id+"F21.wireOp",EDGE,"E547");Q20=makeQuery(id+"F21.imprint","IMPRINT",FACE,{"disambiguationData":[TD([[makeQuery(id+"F21.imprint","IMPRINT",EDGE,{"derivedFrom":subQ0}),1.0]])]});}
            var Q21;
            {var subQ1=sQuery(id+"F21.wireOp",EDGE,"E545");Q21=makeQuery(id+"F21.imprint","IMPRINT",FACE,{"disambiguationData":[TD([[makeQuery(id+"F21.imprint","IMPRINT",EDGE,{"derivedFrom":subQ1}),1.0]])]});}
            var Q22;
            {var subQ1=sQuery(id+"F21.wireOp",EDGE,"E601");Q22=makeQuery(id+"F21.imprint","IMPRINT",FACE,{"disambiguationData":[TD([[makeQuery(id+"F21.imprint","IMPRINT",EDGE,{"derivedFrom":subQ1}),-1.0]])]});}
            var Q23;
            {var subQ0=sQuery(id+"F21.wireOp",EDGE,"E605");Q23=makeQuery(id+"F21.imprint","IMPRINT",FACE,{"disambiguationData":[TD([[makeQuery(id+"F21.imprint","IMPRINT",EDGE,{"derivedFrom":subQ0}),-1.0]])]});}
            var Q24;
            {var subQ0=sQuery(id+"F21.wireOp",EDGE,"E607");Q24=makeQuery(id+"F21.imprint","IMPRINT",FACE,{"disambiguationData":[TD([[makeQuery(id+"F21.imprint","IMPRINT",EDGE,{"derivedFrom":subQ0}),-1.0]])]});}
            var Q25;
            {var subQ8=sQuery(id+"F21.wireOp",EDGE,"E624");Q25=makeQuery(id+"F21.imprint","IMPRINT",FACE,{"disambiguationData":[TD([[makeQuery(id+"F21.imprint","IMPRINT",EDGE,{"derivedFrom":subQ8}),1.0]])]});}
            var Q26;
            {var subQ8=sQuery(id+"F21.wireOp",EDGE,"E607");Q26=makeQuery(id+"F21.imprint","IMPRINT",FACE,{"disambiguationData":[TD([[makeQuery(id+"F21.imprint","IMPRINT",EDGE,{"derivedFrom":subQ8}),1.0]])]});}
            var Q27;
            {var subQ6=sQuery(id+"F21.wireOp",EDGE,"E630");Q27=makeQuery(id+"F21.imprint","IMPRINT",FACE,{"disambiguationData":[TD([[makeQuery(id+"F21.imprint","IMPRINT",EDGE,{"derivedFrom":subQ6}),1.0]])]});}
            var Q28;
            {var subQ0=sQuery(id+"F21.wireOp",EDGE,"E628");Q28=makeQuery(id+"F21.imprint","IMPRINT",FACE,{"disambiguationData":[TD([[makeQuery(id+"F21.imprint","IMPRINT",EDGE,{"derivedFrom":subQ0}),-1.0]])]});}
            var Q29;
            {var subQ0=sQuery(id+"F21.wireOp",EDGE,"E626");Q29=makeQuery(id+"F21.imprint","IMPRINT",FACE,{"disambiguationData":[TD([[makeQuery(id+"F21.imprint","IMPRINT",EDGE,{"derivedFrom":subQ0}),-1.0]])]});}
            var Q30;
            {var subQ0=sQuery(id+"F21.wireOp",EDGE,"E630");Q30=makeQuery(id+"F21.imprint","IMPRINT",FACE,{"disambiguationData":[TD([[makeQuery(id+"F21.imprint","IMPRINT",EDGE,{"derivedFrom":subQ0}),-1.0]])]});}
            var Q31;
            {var subQ1=sQuery(id+"F21.wireOp",EDGE,"E624");Q31=makeQuery(id+"F21.imprint","IMPRINT",FACE,{"disambiguationData":[TD([[makeQuery(id+"F21.imprint","IMPRINT",EDGE,{"derivedFrom":subQ1}),-1.0]])]});}
            var Q32;
            {var subQ21=sQuery(id+"F21.wireOp",EDGE,"E534");Q32=makeQuery(id+"F21.imprint","IMPRINT",FACE,{"disambiguationData":[TD([[makeQuery(id+"F21.imprint","IMPRINT",EDGE,{"derivedFrom":subQ21}),-1.0]])]});}
            var Q33;
            {var subQ0=sQuery(id+"F21.wireOp",EDGE,"E598");var subQ1=sQuery(id+"F21.wireOp",EDGE,"E577");var subQ2=makeQuery(id+"F21.imprint","INTERSECT",VERTEX,{"derivedFrom":[subQ1,subQ0]});Q33=makeQuery(id+"F21.imprint","IMPRINT",FACE,{"disambiguationData":[TD([[makeQuery(id+"F21.imprint","IMPRINT",EDGE,{"disambiguationData":[TD([[subQ2,-1.0]])],"derivedFrom":subQ1}),-1.0]])]});}
            var Q34;
            {var subQ9=sQuery(id+"F21.wireOp",EDGE,"E547");Q34=makeQuery(id+"F21.imprint","IMPRINT",FACE,{"disambiguationData":[TD([[makeQuery(id+"F21.imprint","IMPRINT",EDGE,{"derivedFrom":subQ9}),-1.0]])]});}
            var Q35;
            {var subQ0=sQuery(id+"F21.wireOp",EDGE,"E598");var subQ1=sQuery(id+"F21.wireOp",EDGE,"E577");var subQ2=makeQuery(id+"F21.imprint","INTERSECT",VERTEX,{"derivedFrom":[subQ1,subQ0]});Q35=makeQuery(id+"F21.imprint","IMPRINT",FACE,{"disambiguationData":[TD([[makeQuery(id+"F21.imprint","IMPRINT",EDGE,{"disambiguationData":[TD([[subQ2,-1.0]])],"derivedFrom":subQ1}),1.0]])]});}
            extrude(context, id + "F22", {"entities" : qUnion([Q0, Q1, Q2, Q3, Q4, Q5, Q6, Q7, Q8, Q9, Q10, Q11, Q12, Q13, Q14, Q15, Q16, Q17, Q18, Q19, Q20, Q21, Q22, Q23, Q24, Q25, Q26, Q27, Q28, Q29, Q30, Q31, Q32, Q33, Q34, Q35]), "depth" : 460 * mm, "offsetDistance" : 25 * mm});
        }
        {
            var Q0;
            Q0=makeQuery(id+"F22.opExtrude","SWEPT_BODY",BODY,{"disambiguationData":[OSD([sQuery(id+"F21.wireOp",EDGE,"E528"),sQuery(id+"F21.wireOp",EDGE,"E529"),sQuery(id+"F21.wireOp",EDGE,"E530"),sQuery(id+"F21.wireOp",EDGE,"E531"),sQuery(id+"F21.wireOp",EDGE,"E532"),sQuery(id+"F21.wireOp",EDGE,"E533"),sQuery(id+"F21.wireOp",EDGE,"E534"),sQuery(id+"F21.wireOp",EDGE,"E535"),sQuery(id+"F21.wireOp",EDGE,"E536"),sQuery(id+"F21.wireOp",EDGE,"E553"),sQuery(id+"F21.wireOp",EDGE,"E554"),sQuery(id+"F21.wireOp",EDGE,"E555"),sQuery(id+"F21.wireOp",EDGE,"E556"),sQuery(id+"F21.wireOp",EDGE,"E557"),sQuery(id+"F21.wireOp",EDGE,"E558"),sQuery(id+"F21.wireOp",EDGE,"E559"),sQuery(id+"F21.wireOp",EDGE,"E560"),sQuery(id+"F21.wireOp",EDGE,"E561"),sQuery(id+"F21.wireOp",EDGE,"E562"),sQuery(id+"F21.wireOp",EDGE,"E563"),sQuery(id+"F21.wireOp",EDGE,"E564"),sQuery(id+"F21.wireOp",EDGE,"E565"),sQuery(id+"F21.wireOp",EDGE,"E566"),sQuery(id+"F21.wireOp",EDGE,"E567"),sQuery(id+"F21.wireOp",EDGE,"E568"),sQuery(id+"F21.wireOp",EDGE,"E569"),sQuery(id+"F21.wireOp",EDGE,"E570"),sQuery(id+"F21.wireOp",EDGE,"E571"),sQuery(id+"F21.wireOp",EDGE,"E572"),sQuery(id+"F21.wireOp",EDGE,"E573"),sQuery(id+"F21.wireOp",EDGE,"E574"),sQuery(id+"F21.wireOp",EDGE,"E575"),sQuery(id+"F21.wireOp",EDGE,"E576"),sQuery(id+"F21.wireOp",EDGE,"E578"),sQuery(id+"F21.wireOp",EDGE,"E579"),sQuery(id+"F21.wireOp",EDGE,"E580"),sQuery(id+"F21.wireOp",EDGE,"E581"),sQuery(id+"F21.wireOp",EDGE,"E582"),sQuery(id+"F21.wireOp",EDGE,"E583"),sQuery(id+"F21.wireOp",EDGE,"E584"),sQuery(id+"F21.wireOp",EDGE,"E585"),sQuery(id+"F21.wireOp",EDGE,"E586"),sQuery(id+"F21.wireOp",EDGE,"E587"),sQuery(id+"F21.wireOp",EDGE,"E588"),sQuery(id+"F21.wireOp",EDGE,"E589"),sQuery(id+"F21.wireOp",EDGE,"E590"),sQuery(id+"F21.wireOp",EDGE,"E591"),sQuery(id+"F21.wireOp",EDGE,"E592"),sQuery(id+"F21.wireOp",EDGE,"E593"),sQuery(id+"F21.wireOp",EDGE,"E594"),sQuery(id+"F21.wireOp",EDGE,"E595"),sQuery(id+"F21.wireOp",EDGE,"E596"),sQuery(id+"F21.wireOp",EDGE,"E597"),sQuery(id+"F21.wireOp",EDGE,"E609"),sQuery(id+"F21.wireOp",EDGE,"E610"),sQuery(id+"F21.wireOp",EDGE,"E611"),sQuery(id+"F21.wireOp",EDGE,"E612"),sQuery(id+"F21.wireOp",EDGE,"E613"),sQuery(id+"F21.wireOp",EDGE,"E614"),sQuery(id+"F21.wireOp",EDGE,"E615"),sQuery(id+"F21.wireOp",EDGE,"E616"),sQuery(id+"F21.wireOp",EDGE,"E617"),sQuery(id+"F21.wireOp",EDGE,"E618"),sQuery(id+"F21.wireOp",EDGE,"E619"),sQuery(id+"F21.wireOp",EDGE,"E620"),sQuery(id+"F21.wireOp",EDGE,"E621"),sQuery(id+"F21.wireOp",EDGE,"E632"),sQuery(id+"F21.wireOp",EDGE,"E633"),sQuery(id+"F21.wireOp",EDGE,"E634"),sQuery(id+"F21.wireOp",EDGE,"E635"),sQuery(id+"F21.wireOp",EDGE,"E636"),sQuery(id+"F21.wireOp",EDGE,"E637"),sQuery(id+"F21.wireOp",EDGE,"E638"),sQuery(id+"F21.wireOp",EDGE,"E639"),sQuery(id+"F21.wireOp",EDGE,"E640"),sQuery(id+"F21.wireOp",EDGE,"E641"),sQuery(id+"F21.wireOp",EDGE,"E642"),sQuery(id+"F21.wireOp",EDGE,"E643"),sQuery(id+"F21.wireOp",EDGE,"E644"),sQuery(id+"F21.wireOp",EDGE,"E645"),sQuery(id+"F21.wireOp",EDGE,"E646"),sQuery(id+"F21.wireOp",EDGE,"E647"),sQuery(id+"F21.wireOp",EDGE,"E648"),sQuery(id+"F21.wireOp",EDGE,"E649"),sQuery(id+"F21.wireOp",EDGE,"E650"),sQuery(id+"F21.wireOp",EDGE,"E651"),sQuery(id+"F21.wireOp",EDGE,"E652"),sQuery(id+"F21.wireOp",EDGE,"E653")])]});
            transform(context, id + "F23", {"entities" : qUnion([Q0]), "transformType" : TransformType.TRANSLATION_3D, "dx" : -353 * mm, "dy" : 0 * mm, "dz" : 0 * mm, "makeCopy" : false});
        }
        {
            var Q0;
            Q0=makeQuery(id+"F22.opExtrude","SWEPT_BODY",BODY,{"disambiguationData":[OSD([sQuery(id+"F21.wireOp",EDGE,"E528"),sQuery(id+"F21.wireOp",EDGE,"E529"),sQuery(id+"F21.wireOp",EDGE,"E530"),sQuery(id+"F21.wireOp",EDGE,"E531"),sQuery(id+"F21.wireOp",EDGE,"E532"),sQuery(id+"F21.wireOp",EDGE,"E533"),sQuery(id+"F21.wireOp",EDGE,"E534"),sQuery(id+"F21.wireOp",EDGE,"E535"),sQuery(id+"F21.wireOp",EDGE,"E536"),sQuery(id+"F21.wireOp",EDGE,"E553"),sQuery(id+"F21.wireOp",EDGE,"E554"),sQuery(id+"F21.wireOp",EDGE,"E555"),sQuery(id+"F21.wireOp",EDGE,"E556"),sQuery(id+"F21.wireOp",EDGE,"E557"),sQuery(id+"F21.wireOp",EDGE,"E558"),sQuery(id+"F21.wireOp",EDGE,"E559"),sQuery(id+"F21.wireOp",EDGE,"E560"),sQuery(id+"F21.wireOp",EDGE,"E561"),sQuery(id+"F21.wireOp",EDGE,"E562"),sQuery(id+"F21.wireOp",EDGE,"E563"),sQuery(id+"F21.wireOp",EDGE,"E564"),sQuery(id+"F21.wireOp",EDGE,"E565"),sQuery(id+"F21.wireOp",EDGE,"E566"),sQuery(id+"F21.wireOp",EDGE,"E567"),sQuery(id+"F21.wireOp",EDGE,"E568"),sQuery(id+"F21.wireOp",EDGE,"E569"),sQuery(id+"F21.wireOp",EDGE,"E570"),sQuery(id+"F21.wireOp",EDGE,"E571"),sQuery(id+"F21.wireOp",EDGE,"E572"),sQuery(id+"F21.wireOp",EDGE,"E573"),sQuery(id+"F21.wireOp",EDGE,"E574"),sQuery(id+"F21.wireOp",EDGE,"E575"),sQuery(id+"F21.wireOp",EDGE,"E576"),sQuery(id+"F21.wireOp",EDGE,"E578"),sQuery(id+"F21.wireOp",EDGE,"E579"),sQuery(id+"F21.wireOp",EDGE,"E580"),sQuery(id+"F21.wireOp",EDGE,"E581"),sQuery(id+"F21.wireOp",EDGE,"E582"),sQuery(id+"F21.wireOp",EDGE,"E583"),sQuery(id+"F21.wireOp",EDGE,"E584"),sQuery(id+"F21.wireOp",EDGE,"E585"),sQuery(id+"F21.wireOp",EDGE,"E586"),sQuery(id+"F21.wireOp",EDGE,"E587"),sQuery(id+"F21.wireOp",EDGE,"E588"),sQuery(id+"F21.wireOp",EDGE,"E589"),sQuery(id+"F21.wireOp",EDGE,"E590"),sQuery(id+"F21.wireOp",EDGE,"E591"),sQuery(id+"F21.wireOp",EDGE,"E592"),sQuery(id+"F21.wireOp",EDGE,"E593"),sQuery(id+"F21.wireOp",EDGE,"E594"),sQuery(id+"F21.wireOp",EDGE,"E595"),sQuery(id+"F21.wireOp",EDGE,"E596"),sQuery(id+"F21.wireOp",EDGE,"E597"),sQuery(id+"F21.wireOp",EDGE,"E609"),sQuery(id+"F21.wireOp",EDGE,"E610"),sQuery(id+"F21.wireOp",EDGE,"E611"),sQuery(id+"F21.wireOp",EDGE,"E612"),sQuery(id+"F21.wireOp",EDGE,"E613"),sQuery(id+"F21.wireOp",EDGE,"E614"),sQuery(id+"F21.wireOp",EDGE,"E615"),sQuery(id+"F21.wireOp",EDGE,"E616"),sQuery(id+"F21.wireOp",EDGE,"E617"),sQuery(id+"F21.wireOp",EDGE,"E618"),sQuery(id+"F21.wireOp",EDGE,"E619"),sQuery(id+"F21.wireOp",EDGE,"E620"),sQuery(id+"F21.wireOp",EDGE,"E621"),sQuery(id+"F21.wireOp",EDGE,"E632"),sQuery(id+"F21.wireOp",EDGE,"E633"),sQuery(id+"F21.wireOp",EDGE,"E634"),sQuery(id+"F21.wireOp",EDGE,"E635"),sQuery(id+"F21.wireOp",EDGE,"E636"),sQuery(id+"F21.wireOp",EDGE,"E637"),sQuery(id+"F21.wireOp",EDGE,"E638"),sQuery(id+"F21.wireOp",EDGE,"E639"),sQuery(id+"F21.wireOp",EDGE,"E640"),sQuery(id+"F21.wireOp",EDGE,"E641"),sQuery(id+"F21.wireOp",EDGE,"E642"),sQuery(id+"F21.wireOp",EDGE,"E643"),sQuery(id+"F21.wireOp",EDGE,"E644"),sQuery(id+"F21.wireOp",EDGE,"E645"),sQuery(id+"F21.wireOp",EDGE,"E646"),sQuery(id+"F21.wireOp",EDGE,"E647"),sQuery(id+"F21.wireOp",EDGE,"E648"),sQuery(id+"F21.wireOp",EDGE,"E649"),sQuery(id+"F21.wireOp",EDGE,"E650"),sQuery(id+"F21.wireOp",EDGE,"E651"),sQuery(id+"F21.wireOp",EDGE,"E652"),sQuery(id+"F21.wireOp",EDGE,"E653")])]});
            transform(context, id + "F24", {"entities" : qUnion([Q0]), "transformType" : TransformType.TRANSLATION_3D, "dx" : 0 * mm, "dy" : 650 * mm, "dz" : 0 * mm, "makeCopy" : true});
        }
    });
